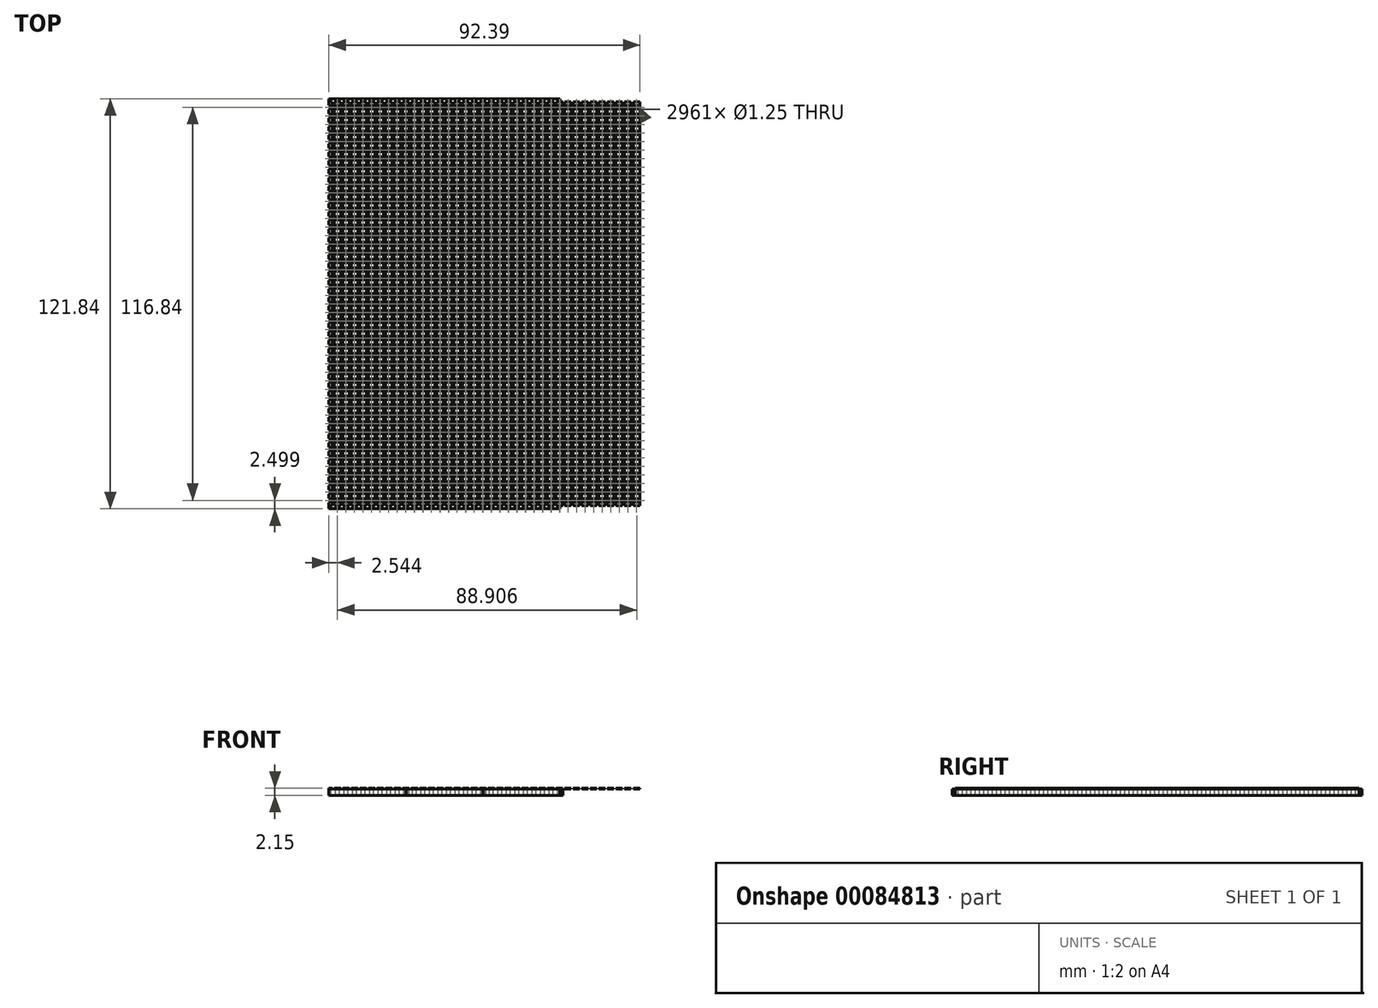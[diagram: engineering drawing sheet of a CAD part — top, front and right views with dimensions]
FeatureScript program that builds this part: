
annotation { "Feature Type Name" : "Feature", "Feature Type Description" : "" }
export const myFeature = defineFeature(function(context is Context, id is Id, definition is map)
    precondition{}
    {
        {
            var Q0;
            Q0=qCreatedBy(makeId("Top.planeOp"),FACE);
            var sketch = newSketch(context, id + "F0", { "sketchPlane" : qUnion([Q0])});
            skCircle(sketch, "E0", {"center": v(-51.8, -35.65) * mm, "radius": 0.63 * mm});
            skCircle(sketch, "E1.1.0.0", {"center": v(-49.26, -35.65) * mm, "radius": 0.63 * mm});
            skCircle(sketch, "E1.2.0.0", {"center": v(-46.72, -35.65) * mm, "radius": 0.63 * mm});
            skCircle(sketch, "E1.3.0.0", {"center": v(-44.18, -35.65) * mm, "radius": 0.63 * mm});
            skCircle(sketch, "E1.4.0.0", {"center": v(-41.64, -35.65) * mm, "radius": 0.63 * mm});
            skCircle(sketch, "E1.5.0.0", {"center": v(-39.1, -35.65) * mm, "radius": 0.63 * mm});
            skCircle(sketch, "E1.6.0.0", {"center": v(-36.56, -35.65) * mm, "radius": 0.63 * mm});
            skCircle(sketch, "E1.7.0.0", {"center": v(-34.02, -35.65) * mm, "radius": 0.63 * mm});
            skCircle(sketch, "E1.8.0.0", {"center": v(-31.48, -35.65) * mm, "radius": 0.63 * mm});
            skCircle(sketch, "E1.9.0.0", {"center": v(-28.94, -35.65) * mm, "radius": 0.63 * mm});
            skLineSegment(sketch, "E1.direction1", {"start": v(-51.8, -35.65) * mm, "end": v(-49.26, -35.65) * mm, "construction": true});
            skLineSegment(sketch, "E2.1.0.0", {"start": v(-51.8, -38.2) * mm, "end": v(-49.26, -38.2) * mm, "construction": true});
            skCircle(sketch, "E2.1.0.1", {"center": v(-28.94, -38.2) * mm, "radius": 0.63 * mm});
            skCircle(sketch, "E2.1.0.2", {"center": v(-31.48, -38.2) * mm, "radius": 0.63 * mm});
            skCircle(sketch, "E2.1.0.3", {"center": v(-34.02, -38.2) * mm, "radius": 0.63 * mm});
            skCircle(sketch, "E2.1.0.4", {"center": v(-36.56, -38.2) * mm, "radius": 0.63 * mm});
            skCircle(sketch, "E2.1.0.5", {"center": v(-39.1, -38.2) * mm, "radius": 0.63 * mm});
            skCircle(sketch, "E2.1.0.6", {"center": v(-41.64, -38.2) * mm, "radius": 0.63 * mm});
            skCircle(sketch, "E2.1.0.7", {"center": v(-44.18, -38.2) * mm, "radius": 0.63 * mm});
            skCircle(sketch, "E2.1.0.8", {"center": v(-46.72, -38.2) * mm, "radius": 0.63 * mm});
            skCircle(sketch, "E2.1.0.9", {"center": v(-49.26, -38.2) * mm, "radius": 0.63 * mm});
            skCircle(sketch, "E2.1.0.10", {"center": v(-51.8, -38.2) * mm, "radius": 0.63 * mm});
            skLineSegment(sketch, "E2.2.0.0", {"start": v(-51.8, -40.73) * mm, "end": v(-49.26, -40.73) * mm, "construction": true});
            skCircle(sketch, "E2.2.0.1", {"center": v(-28.94, -40.73) * mm, "radius": 0.63 * mm});
            skCircle(sketch, "E2.2.0.2", {"center": v(-31.48, -40.73) * mm, "radius": 0.63 * mm});
            skCircle(sketch, "E2.2.0.3", {"center": v(-34.02, -40.73) * mm, "radius": 0.63 * mm});
            skCircle(sketch, "E2.2.0.4", {"center": v(-36.56, -40.73) * mm, "radius": 0.63 * mm});
            skCircle(sketch, "E2.2.0.5", {"center": v(-39.1, -40.73) * mm, "radius": 0.63 * mm});
            skCircle(sketch, "E2.2.0.6", {"center": v(-41.64, -40.73) * mm, "radius": 0.63 * mm});
            skCircle(sketch, "E2.2.0.7", {"center": v(-44.18, -40.73) * mm, "radius": 0.63 * mm});
            skCircle(sketch, "E2.2.0.8", {"center": v(-46.72, -40.73) * mm, "radius": 0.63 * mm});
            skCircle(sketch, "E2.2.0.9", {"center": v(-49.26, -40.73) * mm, "radius": 0.63 * mm});
            skCircle(sketch, "E2.2.0.10", {"center": v(-51.8, -40.73) * mm, "radius": 0.63 * mm});
            skLineSegment(sketch, "E2.3.0.0", {"start": v(-51.8, -43.27) * mm, "end": v(-49.26, -43.27) * mm, "construction": true});
            skCircle(sketch, "E2.3.0.1", {"center": v(-28.94, -43.27) * mm, "radius": 0.63 * mm});
            skCircle(sketch, "E2.3.0.2", {"center": v(-31.48, -43.27) * mm, "radius": 0.63 * mm});
            skCircle(sketch, "E2.3.0.3", {"center": v(-34.02, -43.27) * mm, "radius": 0.63 * mm});
            skCircle(sketch, "E2.3.0.4", {"center": v(-36.56, -43.27) * mm, "radius": 0.63 * mm});
            skCircle(sketch, "E2.3.0.5", {"center": v(-39.1, -43.27) * mm, "radius": 0.63 * mm});
            skCircle(sketch, "E2.3.0.6", {"center": v(-41.64, -43.27) * mm, "radius": 0.63 * mm});
            skCircle(sketch, "E2.3.0.7", {"center": v(-44.18, -43.27) * mm, "radius": 0.63 * mm});
            skCircle(sketch, "E2.3.0.8", {"center": v(-46.72, -43.27) * mm, "radius": 0.63 * mm});
            skCircle(sketch, "E2.3.0.9", {"center": v(-49.26, -43.27) * mm, "radius": 0.63 * mm});
            skCircle(sketch, "E2.3.0.10", {"center": v(-51.8, -43.27) * mm, "radius": 0.63 * mm});
            skLineSegment(sketch, "E2.4.0.0", {"start": v(-51.8, -45.81) * mm, "end": v(-49.26, -45.81) * mm, "construction": true});
            skCircle(sketch, "E2.4.0.1", {"center": v(-28.94, -45.81) * mm, "radius": 0.63 * mm});
            skCircle(sketch, "E2.4.0.2", {"center": v(-31.48, -45.81) * mm, "radius": 0.63 * mm});
            skCircle(sketch, "E2.4.0.3", {"center": v(-34.02, -45.81) * mm, "radius": 0.63 * mm});
            skCircle(sketch, "E2.4.0.4", {"center": v(-36.56, -45.81) * mm, "radius": 0.63 * mm});
            skCircle(sketch, "E2.4.0.5", {"center": v(-39.1, -45.81) * mm, "radius": 0.63 * mm});
            skCircle(sketch, "E2.4.0.6", {"center": v(-41.64, -45.81) * mm, "radius": 0.63 * mm});
            skCircle(sketch, "E2.4.0.7", {"center": v(-44.18, -45.81) * mm, "radius": 0.63 * mm});
            skCircle(sketch, "E2.4.0.8", {"center": v(-46.72, -45.81) * mm, "radius": 0.63 * mm});
            skCircle(sketch, "E2.4.0.9", {"center": v(-49.26, -45.81) * mm, "radius": 0.63 * mm});
            skCircle(sketch, "E2.4.0.10", {"center": v(-51.8, -45.81) * mm, "radius": 0.63 * mm});
            skLineSegment(sketch, "E2.5.0.0", {"start": v(-51.8, -48.35) * mm, "end": v(-49.26, -48.35) * mm, "construction": true});
            skCircle(sketch, "E2.5.0.1", {"center": v(-28.94, -48.35) * mm, "radius": 0.63 * mm});
            skCircle(sketch, "E2.5.0.2", {"center": v(-31.48, -48.35) * mm, "radius": 0.63 * mm});
            skCircle(sketch, "E2.5.0.3", {"center": v(-34.02, -48.35) * mm, "radius": 0.63 * mm});
            skCircle(sketch, "E2.5.0.4", {"center": v(-36.56, -48.35) * mm, "radius": 0.63 * mm});
            skCircle(sketch, "E2.5.0.5", {"center": v(-39.1, -48.35) * mm, "radius": 0.63 * mm});
            skCircle(sketch, "E2.5.0.6", {"center": v(-41.64, -48.35) * mm, "radius": 0.63 * mm});
            skCircle(sketch, "E2.5.0.7", {"center": v(-44.18, -48.35) * mm, "radius": 0.63 * mm});
            skCircle(sketch, "E2.5.0.8", {"center": v(-46.72, -48.35) * mm, "radius": 0.63 * mm});
            skCircle(sketch, "E2.5.0.9", {"center": v(-49.26, -48.35) * mm, "radius": 0.63 * mm});
            skCircle(sketch, "E2.5.0.10", {"center": v(-51.8, -48.35) * mm, "radius": 0.63 * mm});
            skLineSegment(sketch, "E2.6.0.0", {"start": v(-51.8, -50.9) * mm, "end": v(-49.26, -50.9) * mm, "construction": true});
            skCircle(sketch, "E2.6.0.1", {"center": v(-28.94, -50.9) * mm, "radius": 0.63 * mm});
            skCircle(sketch, "E2.6.0.2", {"center": v(-31.48, -50.9) * mm, "radius": 0.63 * mm});
            skCircle(sketch, "E2.6.0.3", {"center": v(-34.02, -50.9) * mm, "radius": 0.63 * mm});
            skCircle(sketch, "E2.6.0.4", {"center": v(-36.56, -50.9) * mm, "radius": 0.63 * mm});
            skCircle(sketch, "E2.6.0.5", {"center": v(-39.1, -50.9) * mm, "radius": 0.63 * mm});
            skCircle(sketch, "E2.6.0.6", {"center": v(-41.64, -50.9) * mm, "radius": 0.63 * mm});
            skCircle(sketch, "E2.6.0.7", {"center": v(-44.18, -50.9) * mm, "radius": 0.63 * mm});
            skCircle(sketch, "E2.6.0.8", {"center": v(-46.72, -50.9) * mm, "radius": 0.63 * mm});
            skCircle(sketch, "E2.6.0.9", {"center": v(-49.26, -50.9) * mm, "radius": 0.63 * mm});
            skCircle(sketch, "E2.6.0.10", {"center": v(-51.8, -50.9) * mm, "radius": 0.63 * mm});
            skLineSegment(sketch, "E2.7.0.0", {"start": v(-51.8, -53.43) * mm, "end": v(-49.26, -53.43) * mm, "construction": true});
            skCircle(sketch, "E2.7.0.1", {"center": v(-28.94, -53.43) * mm, "radius": 0.63 * mm});
            skCircle(sketch, "E2.7.0.2", {"center": v(-31.48, -53.43) * mm, "radius": 0.63 * mm});
            skCircle(sketch, "E2.7.0.3", {"center": v(-34.02, -53.43) * mm, "radius": 0.63 * mm});
            skCircle(sketch, "E2.7.0.4", {"center": v(-36.56, -53.43) * mm, "radius": 0.63 * mm});
            skCircle(sketch, "E2.7.0.5", {"center": v(-39.1, -53.43) * mm, "radius": 0.63 * mm});
            skCircle(sketch, "E2.7.0.6", {"center": v(-41.64, -53.43) * mm, "radius": 0.63 * mm});
            skCircle(sketch, "E2.7.0.7", {"center": v(-44.18, -53.43) * mm, "radius": 0.63 * mm});
            skCircle(sketch, "E2.7.0.8", {"center": v(-46.72, -53.43) * mm, "radius": 0.63 * mm});
            skCircle(sketch, "E2.7.0.9", {"center": v(-49.26, -53.43) * mm, "radius": 0.63 * mm});
            skCircle(sketch, "E2.7.0.10", {"center": v(-51.8, -53.43) * mm, "radius": 0.63 * mm});
            skLineSegment(sketch, "E2.8.0.0", {"start": v(-51.8, -55.97) * mm, "end": v(-49.26, -55.97) * mm, "construction": true});
            skCircle(sketch, "E2.8.0.1", {"center": v(-28.94, -55.97) * mm, "radius": 0.63 * mm});
            skCircle(sketch, "E2.8.0.2", {"center": v(-31.48, -55.97) * mm, "radius": 0.63 * mm});
            skCircle(sketch, "E2.8.0.3", {"center": v(-34.02, -55.97) * mm, "radius": 0.63 * mm});
            skCircle(sketch, "E2.8.0.4", {"center": v(-36.56, -55.97) * mm, "radius": 0.63 * mm});
            skCircle(sketch, "E2.8.0.5", {"center": v(-39.1, -55.97) * mm, "radius": 0.63 * mm});
            skCircle(sketch, "E2.8.0.6", {"center": v(-41.64, -55.97) * mm, "radius": 0.63 * mm});
            skCircle(sketch, "E2.8.0.7", {"center": v(-44.18, -55.97) * mm, "radius": 0.63 * mm});
            skCircle(sketch, "E2.8.0.8", {"center": v(-46.72, -55.97) * mm, "radius": 0.63 * mm});
            skCircle(sketch, "E2.8.0.9", {"center": v(-49.26, -55.97) * mm, "radius": 0.63 * mm});
            skCircle(sketch, "E2.8.0.10", {"center": v(-51.8, -55.97) * mm, "radius": 0.63 * mm});
            skLineSegment(sketch, "E2.9.0.0", {"start": v(-51.8, -58.51) * mm, "end": v(-49.26, -58.51) * mm, "construction": true});
            skCircle(sketch, "E2.9.0.1", {"center": v(-28.94, -58.51) * mm, "radius": 0.63 * mm});
            skCircle(sketch, "E2.9.0.2", {"center": v(-31.48, -58.51) * mm, "radius": 0.63 * mm});
            skCircle(sketch, "E2.9.0.3", {"center": v(-34.02, -58.51) * mm, "radius": 0.63 * mm});
            skCircle(sketch, "E2.9.0.4", {"center": v(-36.56, -58.51) * mm, "radius": 0.63 * mm});
            skCircle(sketch, "E2.9.0.5", {"center": v(-39.1, -58.51) * mm, "radius": 0.63 * mm});
            skCircle(sketch, "E2.9.0.6", {"center": v(-41.64, -58.51) * mm, "radius": 0.63 * mm});
            skCircle(sketch, "E2.9.0.7", {"center": v(-44.18, -58.51) * mm, "radius": 0.63 * mm});
            skCircle(sketch, "E2.9.0.8", {"center": v(-46.72, -58.51) * mm, "radius": 0.63 * mm});
            skCircle(sketch, "E2.9.0.9", {"center": v(-49.26, -58.51) * mm, "radius": 0.63 * mm});
            skCircle(sketch, "E2.9.0.10", {"center": v(-51.8, -58.51) * mm, "radius": 0.63 * mm});
            skLineSegment(sketch, "E2.10.0.0", {"start": v(-51.8, -61.05) * mm, "end": v(-49.26, -61.05) * mm, "construction": true});
            skCircle(sketch, "E2.10.0.1", {"center": v(-28.94, -61.05) * mm, "radius": 0.63 * mm});
            skCircle(sketch, "E2.10.0.2", {"center": v(-31.48, -61.05) * mm, "radius": 0.63 * mm});
            skCircle(sketch, "E2.10.0.3", {"center": v(-34.02, -61.05) * mm, "radius": 0.63 * mm});
            skCircle(sketch, "E2.10.0.4", {"center": v(-36.56, -61.05) * mm, "radius": 0.63 * mm});
            skCircle(sketch, "E2.10.0.5", {"center": v(-39.1, -61.05) * mm, "radius": 0.63 * mm});
            skCircle(sketch, "E2.10.0.6", {"center": v(-41.64, -61.05) * mm, "radius": 0.63 * mm});
            skCircle(sketch, "E2.10.0.7", {"center": v(-44.18, -61.05) * mm, "radius": 0.63 * mm});
            skCircle(sketch, "E2.10.0.8", {"center": v(-46.72, -61.05) * mm, "radius": 0.63 * mm});
            skCircle(sketch, "E2.10.0.9", {"center": v(-49.26, -61.05) * mm, "radius": 0.63 * mm});
            skCircle(sketch, "E2.10.0.10", {"center": v(-51.8, -61.05) * mm, "radius": 0.63 * mm});
            skLineSegment(sketch, "E2.11.0.0", {"start": v(-51.8, -63.6) * mm, "end": v(-49.26, -63.6) * mm, "construction": true});
            skCircle(sketch, "E2.11.0.1", {"center": v(-28.94, -63.6) * mm, "radius": 0.63 * mm});
            skCircle(sketch, "E2.11.0.2", {"center": v(-31.48, -63.6) * mm, "radius": 0.63 * mm});
            skCircle(sketch, "E2.11.0.3", {"center": v(-34.02, -63.6) * mm, "radius": 0.63 * mm});
            skCircle(sketch, "E2.11.0.4", {"center": v(-36.56, -63.6) * mm, "radius": 0.63 * mm});
            skCircle(sketch, "E2.11.0.5", {"center": v(-39.1, -63.6) * mm, "radius": 0.63 * mm});
            skCircle(sketch, "E2.11.0.6", {"center": v(-41.64, -63.6) * mm, "radius": 0.63 * mm});
            skCircle(sketch, "E2.11.0.7", {"center": v(-44.18, -63.6) * mm, "radius": 0.63 * mm});
            skCircle(sketch, "E2.11.0.8", {"center": v(-46.72, -63.6) * mm, "radius": 0.63 * mm});
            skCircle(sketch, "E2.11.0.9", {"center": v(-49.26, -63.6) * mm, "radius": 0.63 * mm});
            skCircle(sketch, "E2.11.0.10", {"center": v(-51.8, -63.6) * mm, "radius": 0.63 * mm});
            skLineSegment(sketch, "E2.12.0.0", {"start": v(-51.8, -66.13) * mm, "end": v(-49.26, -66.13) * mm, "construction": true});
            skCircle(sketch, "E2.12.0.1", {"center": v(-28.94, -66.13) * mm, "radius": 0.63 * mm});
            skCircle(sketch, "E2.12.0.2", {"center": v(-31.48, -66.13) * mm, "radius": 0.63 * mm});
            skCircle(sketch, "E2.12.0.3", {"center": v(-34.02, -66.13) * mm, "radius": 0.63 * mm});
            skCircle(sketch, "E2.12.0.4", {"center": v(-36.56, -66.13) * mm, "radius": 0.63 * mm});
            skCircle(sketch, "E2.12.0.5", {"center": v(-39.1, -66.13) * mm, "radius": 0.63 * mm});
            skCircle(sketch, "E2.12.0.6", {"center": v(-41.64, -66.13) * mm, "radius": 0.63 * mm});
            skCircle(sketch, "E2.12.0.7", {"center": v(-44.18, -66.13) * mm, "radius": 0.63 * mm});
            skCircle(sketch, "E2.12.0.8", {"center": v(-46.72, -66.13) * mm, "radius": 0.63 * mm});
            skCircle(sketch, "E2.12.0.9", {"center": v(-49.26, -66.13) * mm, "radius": 0.63 * mm});
            skCircle(sketch, "E2.12.0.10", {"center": v(-51.8, -66.13) * mm, "radius": 0.63 * mm});
            skLineSegment(sketch, "E2.13.0.0", {"start": v(-51.8, -68.67) * mm, "end": v(-49.26, -68.67) * mm, "construction": true});
            skCircle(sketch, "E2.13.0.1", {"center": v(-28.94, -68.67) * mm, "radius": 0.63 * mm});
            skCircle(sketch, "E2.13.0.2", {"center": v(-31.48, -68.67) * mm, "radius": 0.63 * mm});
            skCircle(sketch, "E2.13.0.3", {"center": v(-34.02, -68.67) * mm, "radius": 0.63 * mm});
            skCircle(sketch, "E2.13.0.4", {"center": v(-36.56, -68.67) * mm, "radius": 0.63 * mm});
            skCircle(sketch, "E2.13.0.5", {"center": v(-39.1, -68.67) * mm, "radius": 0.63 * mm});
            skCircle(sketch, "E2.13.0.6", {"center": v(-41.64, -68.67) * mm, "radius": 0.63 * mm});
            skCircle(sketch, "E2.13.0.7", {"center": v(-44.18, -68.67) * mm, "radius": 0.63 * mm});
            skCircle(sketch, "E2.13.0.8", {"center": v(-46.72, -68.67) * mm, "radius": 0.63 * mm});
            skCircle(sketch, "E2.13.0.9", {"center": v(-49.26, -68.67) * mm, "radius": 0.63 * mm});
            skCircle(sketch, "E2.13.0.10", {"center": v(-51.8, -68.67) * mm, "radius": 0.63 * mm});
            skLineSegment(sketch, "E2.14.0.0", {"start": v(-51.8, -71.21) * mm, "end": v(-49.26, -71.21) * mm, "construction": true});
            skCircle(sketch, "E2.14.0.1", {"center": v(-28.94, -71.21) * mm, "radius": 0.63 * mm});
            skCircle(sketch, "E2.14.0.2", {"center": v(-31.48, -71.21) * mm, "radius": 0.63 * mm});
            skCircle(sketch, "E2.14.0.3", {"center": v(-34.02, -71.21) * mm, "radius": 0.63 * mm});
            skCircle(sketch, "E2.14.0.4", {"center": v(-36.56, -71.21) * mm, "radius": 0.63 * mm});
            skCircle(sketch, "E2.14.0.5", {"center": v(-39.1, -71.21) * mm, "radius": 0.63 * mm});
            skCircle(sketch, "E2.14.0.6", {"center": v(-41.64, -71.21) * mm, "radius": 0.63 * mm});
            skCircle(sketch, "E2.14.0.7", {"center": v(-44.18, -71.21) * mm, "radius": 0.63 * mm});
            skCircle(sketch, "E2.14.0.8", {"center": v(-46.72, -71.21) * mm, "radius": 0.63 * mm});
            skCircle(sketch, "E2.14.0.9", {"center": v(-49.26, -71.21) * mm, "radius": 0.63 * mm});
            skCircle(sketch, "E2.14.0.10", {"center": v(-51.8, -71.21) * mm, "radius": 0.63 * mm});
            skLineSegment(sketch, "E2.15.0.0", {"start": v(-51.8, -73.75) * mm, "end": v(-49.26, -73.75) * mm, "construction": true});
            skCircle(sketch, "E2.15.0.1", {"center": v(-28.94, -73.75) * mm, "radius": 0.63 * mm});
            skCircle(sketch, "E2.15.0.2", {"center": v(-31.48, -73.75) * mm, "radius": 0.63 * mm});
            skCircle(sketch, "E2.15.0.3", {"center": v(-34.02, -73.75) * mm, "radius": 0.63 * mm});
            skCircle(sketch, "E2.15.0.4", {"center": v(-36.56, -73.75) * mm, "radius": 0.63 * mm});
            skCircle(sketch, "E2.15.0.5", {"center": v(-39.1, -73.75) * mm, "radius": 0.63 * mm});
            skCircle(sketch, "E2.15.0.6", {"center": v(-41.64, -73.75) * mm, "radius": 0.63 * mm});
            skCircle(sketch, "E2.15.0.7", {"center": v(-44.18, -73.75) * mm, "radius": 0.63 * mm});
            skCircle(sketch, "E2.15.0.8", {"center": v(-46.72, -73.75) * mm, "radius": 0.63 * mm});
            skCircle(sketch, "E2.15.0.9", {"center": v(-49.26, -73.75) * mm, "radius": 0.63 * mm});
            skCircle(sketch, "E2.15.0.10", {"center": v(-51.8, -73.75) * mm, "radius": 0.63 * mm});
            skLineSegment(sketch, "E2.16.0.0", {"start": v(-51.8, -76.3) * mm, "end": v(-49.26, -76.3) * mm, "construction": true});
            skCircle(sketch, "E2.16.0.1", {"center": v(-28.94, -76.3) * mm, "radius": 0.63 * mm});
            skCircle(sketch, "E2.16.0.2", {"center": v(-31.48, -76.3) * mm, "radius": 0.63 * mm});
            skCircle(sketch, "E2.16.0.3", {"center": v(-34.02, -76.3) * mm, "radius": 0.63 * mm});
            skCircle(sketch, "E2.16.0.4", {"center": v(-36.56, -76.3) * mm, "radius": 0.63 * mm});
            skCircle(sketch, "E2.16.0.5", {"center": v(-39.1, -76.3) * mm, "radius": 0.63 * mm});
            skCircle(sketch, "E2.16.0.6", {"center": v(-41.64, -76.3) * mm, "radius": 0.63 * mm});
            skCircle(sketch, "E2.16.0.7", {"center": v(-44.18, -76.3) * mm, "radius": 0.63 * mm});
            skCircle(sketch, "E2.16.0.8", {"center": v(-46.72, -76.3) * mm, "radius": 0.63 * mm});
            skCircle(sketch, "E2.16.0.9", {"center": v(-49.26, -76.3) * mm, "radius": 0.63 * mm});
            skCircle(sketch, "E2.16.0.10", {"center": v(-51.8, -76.3) * mm, "radius": 0.63 * mm});
            skLineSegment(sketch, "E2.17.0.0", {"start": v(-51.8, -78.83) * mm, "end": v(-49.26, -78.83) * mm, "construction": true});
            skCircle(sketch, "E2.17.0.1", {"center": v(-28.94, -78.83) * mm, "radius": 0.63 * mm});
            skCircle(sketch, "E2.17.0.2", {"center": v(-31.48, -78.83) * mm, "radius": 0.63 * mm});
            skCircle(sketch, "E2.17.0.3", {"center": v(-34.02, -78.83) * mm, "radius": 0.63 * mm});
            skCircle(sketch, "E2.17.0.4", {"center": v(-36.56, -78.83) * mm, "radius": 0.63 * mm});
            skCircle(sketch, "E2.17.0.5", {"center": v(-39.1, -78.83) * mm, "radius": 0.63 * mm});
            skCircle(sketch, "E2.17.0.6", {"center": v(-41.64, -78.83) * mm, "radius": 0.63 * mm});
            skCircle(sketch, "E2.17.0.7", {"center": v(-44.18, -78.83) * mm, "radius": 0.63 * mm});
            skCircle(sketch, "E2.17.0.8", {"center": v(-46.72, -78.83) * mm, "radius": 0.63 * mm});
            skCircle(sketch, "E2.17.0.9", {"center": v(-49.26, -78.83) * mm, "radius": 0.63 * mm});
            skCircle(sketch, "E2.17.0.10", {"center": v(-51.8, -78.83) * mm, "radius": 0.63 * mm});
            skLineSegment(sketch, "E2.18.0.0", {"start": v(-51.8, -81.37) * mm, "end": v(-49.26, -81.37) * mm, "construction": true});
            skCircle(sketch, "E2.18.0.1", {"center": v(-28.94, -81.37) * mm, "radius": 0.63 * mm});
            skCircle(sketch, "E2.18.0.2", {"center": v(-31.48, -81.37) * mm, "radius": 0.63 * mm});
            skCircle(sketch, "E2.18.0.3", {"center": v(-34.02, -81.37) * mm, "radius": 0.63 * mm});
            skCircle(sketch, "E2.18.0.4", {"center": v(-36.56, -81.37) * mm, "radius": 0.63 * mm});
            skCircle(sketch, "E2.18.0.5", {"center": v(-39.1, -81.37) * mm, "radius": 0.63 * mm});
            skCircle(sketch, "E2.18.0.6", {"center": v(-41.64, -81.37) * mm, "radius": 0.63 * mm});
            skCircle(sketch, "E2.18.0.7", {"center": v(-44.18, -81.37) * mm, "radius": 0.63 * mm});
            skCircle(sketch, "E2.18.0.8", {"center": v(-46.72, -81.37) * mm, "radius": 0.63 * mm});
            skCircle(sketch, "E2.18.0.9", {"center": v(-49.26, -81.37) * mm, "radius": 0.63 * mm});
            skCircle(sketch, "E2.18.0.10", {"center": v(-51.8, -81.37) * mm, "radius": 0.63 * mm});
            skLineSegment(sketch, "E2.19.0.0", {"start": v(-51.8, -83.91) * mm, "end": v(-49.26, -83.91) * mm, "construction": true});
            skCircle(sketch, "E2.19.0.1", {"center": v(-28.94, -83.91) * mm, "radius": 0.63 * mm});
            skCircle(sketch, "E2.19.0.2", {"center": v(-31.48, -83.91) * mm, "radius": 0.63 * mm});
            skCircle(sketch, "E2.19.0.3", {"center": v(-34.02, -83.91) * mm, "radius": 0.63 * mm});
            skCircle(sketch, "E2.19.0.4", {"center": v(-36.56, -83.91) * mm, "radius": 0.63 * mm});
            skCircle(sketch, "E2.19.0.5", {"center": v(-39.1, -83.91) * mm, "radius": 0.63 * mm});
            skCircle(sketch, "E2.19.0.6", {"center": v(-41.64, -83.91) * mm, "radius": 0.63 * mm});
            skCircle(sketch, "E2.19.0.7", {"center": v(-44.18, -83.91) * mm, "radius": 0.63 * mm});
            skCircle(sketch, "E2.19.0.8", {"center": v(-46.72, -83.91) * mm, "radius": 0.63 * mm});
            skCircle(sketch, "E2.19.0.9", {"center": v(-49.26, -83.91) * mm, "radius": 0.63 * mm});
            skCircle(sketch, "E2.19.0.10", {"center": v(-51.8, -83.91) * mm, "radius": 0.63 * mm});
            skLineSegment(sketch, "E2.20.0.0", {"start": v(-51.8, -86.45) * mm, "end": v(-49.26, -86.45) * mm, "construction": true});
            skCircle(sketch, "E2.20.0.1", {"center": v(-28.94, -86.45) * mm, "radius": 0.63 * mm});
            skCircle(sketch, "E2.20.0.2", {"center": v(-31.48, -86.45) * mm, "radius": 0.63 * mm});
            skCircle(sketch, "E2.20.0.3", {"center": v(-34.02, -86.45) * mm, "radius": 0.63 * mm});
            skCircle(sketch, "E2.20.0.4", {"center": v(-36.56, -86.45) * mm, "radius": 0.63 * mm});
            skCircle(sketch, "E2.20.0.5", {"center": v(-39.1, -86.45) * mm, "radius": 0.63 * mm});
            skCircle(sketch, "E2.20.0.6", {"center": v(-41.64, -86.45) * mm, "radius": 0.63 * mm});
            skCircle(sketch, "E2.20.0.7", {"center": v(-44.18, -86.45) * mm, "radius": 0.63 * mm});
            skCircle(sketch, "E2.20.0.8", {"center": v(-46.72, -86.45) * mm, "radius": 0.63 * mm});
            skCircle(sketch, "E2.20.0.9", {"center": v(-49.26, -86.45) * mm, "radius": 0.63 * mm});
            skCircle(sketch, "E2.20.0.10", {"center": v(-51.8, -86.45) * mm, "radius": 0.63 * mm});
            skLineSegment(sketch, "E2.21.0.0", {"start": v(-51.8, -89) * mm, "end": v(-49.26, -89) * mm, "construction": true});
            skCircle(sketch, "E2.21.0.1", {"center": v(-28.94, -89) * mm, "radius": 0.63 * mm});
            skCircle(sketch, "E2.21.0.2", {"center": v(-31.48, -89) * mm, "radius": 0.63 * mm});
            skCircle(sketch, "E2.21.0.3", {"center": v(-34.02, -89) * mm, "radius": 0.63 * mm});
            skCircle(sketch, "E2.21.0.4", {"center": v(-36.56, -89) * mm, "radius": 0.63 * mm});
            skCircle(sketch, "E2.21.0.5", {"center": v(-39.1, -89) * mm, "radius": 0.63 * mm});
            skCircle(sketch, "E2.21.0.6", {"center": v(-41.64, -89) * mm, "radius": 0.63 * mm});
            skCircle(sketch, "E2.21.0.7", {"center": v(-44.18, -89) * mm, "radius": 0.63 * mm});
            skCircle(sketch, "E2.21.0.8", {"center": v(-46.72, -89) * mm, "radius": 0.63 * mm});
            skCircle(sketch, "E2.21.0.9", {"center": v(-49.26, -89) * mm, "radius": 0.63 * mm});
            skCircle(sketch, "E2.21.0.10", {"center": v(-51.8, -89) * mm, "radius": 0.63 * mm});
            skLineSegment(sketch, "E2.22.0.0", {"start": v(-51.8, -91.53) * mm, "end": v(-49.26, -91.53) * mm, "construction": true});
            skCircle(sketch, "E2.22.0.1", {"center": v(-28.94, -91.53) * mm, "radius": 0.63 * mm});
            skCircle(sketch, "E2.22.0.2", {"center": v(-31.48, -91.53) * mm, "radius": 0.63 * mm});
            skCircle(sketch, "E2.22.0.3", {"center": v(-34.02, -91.53) * mm, "radius": 0.63 * mm});
            skCircle(sketch, "E2.22.0.4", {"center": v(-36.56, -91.53) * mm, "radius": 0.63 * mm});
            skCircle(sketch, "E2.22.0.5", {"center": v(-39.1, -91.53) * mm, "radius": 0.63 * mm});
            skCircle(sketch, "E2.22.0.6", {"center": v(-41.64, -91.53) * mm, "radius": 0.63 * mm});
            skCircle(sketch, "E2.22.0.7", {"center": v(-44.18, -91.53) * mm, "radius": 0.63 * mm});
            skCircle(sketch, "E2.22.0.8", {"center": v(-46.72, -91.53) * mm, "radius": 0.63 * mm});
            skCircle(sketch, "E2.22.0.9", {"center": v(-49.26, -91.53) * mm, "radius": 0.63 * mm});
            skCircle(sketch, "E2.22.0.10", {"center": v(-51.8, -91.53) * mm, "radius": 0.63 * mm});
            skLineSegment(sketch, "E2.23.0.0", {"start": v(-51.8, -94.07) * mm, "end": v(-49.26, -94.07) * mm, "construction": true});
            skCircle(sketch, "E2.23.0.1", {"center": v(-28.94, -94.07) * mm, "radius": 0.63 * mm});
            skCircle(sketch, "E2.23.0.2", {"center": v(-31.48, -94.07) * mm, "radius": 0.63 * mm});
            skCircle(sketch, "E2.23.0.3", {"center": v(-34.02, -94.07) * mm, "radius": 0.63 * mm});
            skCircle(sketch, "E2.23.0.4", {"center": v(-36.56, -94.07) * mm, "radius": 0.63 * mm});
            skCircle(sketch, "E2.23.0.5", {"center": v(-39.1, -94.07) * mm, "radius": 0.63 * mm});
            skCircle(sketch, "E2.23.0.6", {"center": v(-41.64, -94.07) * mm, "radius": 0.63 * mm});
            skCircle(sketch, "E2.23.0.7", {"center": v(-44.18, -94.07) * mm, "radius": 0.63 * mm});
            skCircle(sketch, "E2.23.0.8", {"center": v(-46.72, -94.07) * mm, "radius": 0.63 * mm});
            skCircle(sketch, "E2.23.0.9", {"center": v(-49.26, -94.07) * mm, "radius": 0.63 * mm});
            skCircle(sketch, "E2.23.0.10", {"center": v(-51.8, -94.07) * mm, "radius": 0.63 * mm});
            skLineSegment(sketch, "E2.24.0.0", {"start": v(-51.8, -96.61) * mm, "end": v(-49.26, -96.61) * mm, "construction": true});
            skCircle(sketch, "E2.24.0.1", {"center": v(-28.94, -96.61) * mm, "radius": 0.63 * mm});
            skCircle(sketch, "E2.24.0.2", {"center": v(-31.48, -96.61) * mm, "radius": 0.63 * mm});
            skCircle(sketch, "E2.24.0.3", {"center": v(-34.02, -96.61) * mm, "radius": 0.63 * mm});
            skCircle(sketch, "E2.24.0.4", {"center": v(-36.56, -96.61) * mm, "radius": 0.63 * mm});
            skCircle(sketch, "E2.24.0.5", {"center": v(-39.1, -96.61) * mm, "radius": 0.63 * mm});
            skCircle(sketch, "E2.24.0.6", {"center": v(-41.64, -96.61) * mm, "radius": 0.63 * mm});
            skCircle(sketch, "E2.24.0.7", {"center": v(-44.18, -96.61) * mm, "radius": 0.63 * mm});
            skCircle(sketch, "E2.24.0.8", {"center": v(-46.72, -96.61) * mm, "radius": 0.63 * mm});
            skCircle(sketch, "E2.24.0.9", {"center": v(-49.26, -96.61) * mm, "radius": 0.63 * mm});
            skCircle(sketch, "E2.24.0.10", {"center": v(-51.8, -96.61) * mm, "radius": 0.63 * mm});
            skLineSegment(sketch, "E2.25.0.0", {"start": v(-51.8, -99.15) * mm, "end": v(-49.26, -99.15) * mm, "construction": true});
            skCircle(sketch, "E2.25.0.1", {"center": v(-28.94, -99.15) * mm, "radius": 0.63 * mm});
            skCircle(sketch, "E2.25.0.2", {"center": v(-31.48, -99.15) * mm, "radius": 0.63 * mm});
            skCircle(sketch, "E2.25.0.3", {"center": v(-34.02, -99.15) * mm, "radius": 0.63 * mm});
            skCircle(sketch, "E2.25.0.4", {"center": v(-36.56, -99.15) * mm, "radius": 0.63 * mm});
            skCircle(sketch, "E2.25.0.5", {"center": v(-39.1, -99.15) * mm, "radius": 0.63 * mm});
            skCircle(sketch, "E2.25.0.6", {"center": v(-41.64, -99.15) * mm, "radius": 0.63 * mm});
            skCircle(sketch, "E2.25.0.7", {"center": v(-44.18, -99.15) * mm, "radius": 0.63 * mm});
            skCircle(sketch, "E2.25.0.8", {"center": v(-46.72, -99.15) * mm, "radius": 0.63 * mm});
            skCircle(sketch, "E2.25.0.9", {"center": v(-49.26, -99.15) * mm, "radius": 0.63 * mm});
            skCircle(sketch, "E2.25.0.10", {"center": v(-51.8, -99.15) * mm, "radius": 0.63 * mm});
            skLineSegment(sketch, "E2.26.0.0", {"start": v(-51.8, -101.7) * mm, "end": v(-49.26, -101.7) * mm, "construction": true});
            skCircle(sketch, "E2.26.0.1", {"center": v(-28.94, -101.7) * mm, "radius": 0.63 * mm});
            skCircle(sketch, "E2.26.0.2", {"center": v(-31.48, -101.7) * mm, "radius": 0.63 * mm});
            skCircle(sketch, "E2.26.0.3", {"center": v(-34.02, -101.7) * mm, "radius": 0.63 * mm});
            skCircle(sketch, "E2.26.0.4", {"center": v(-36.56, -101.7) * mm, "radius": 0.63 * mm});
            skCircle(sketch, "E2.26.0.5", {"center": v(-39.1, -101.7) * mm, "radius": 0.63 * mm});
            skCircle(sketch, "E2.26.0.6", {"center": v(-41.64, -101.7) * mm, "radius": 0.63 * mm});
            skCircle(sketch, "E2.26.0.7", {"center": v(-44.18, -101.7) * mm, "radius": 0.63 * mm});
            skCircle(sketch, "E2.26.0.8", {"center": v(-46.72, -101.7) * mm, "radius": 0.63 * mm});
            skCircle(sketch, "E2.26.0.9", {"center": v(-49.26, -101.7) * mm, "radius": 0.63 * mm});
            skCircle(sketch, "E2.26.0.10", {"center": v(-51.8, -101.7) * mm, "radius": 0.63 * mm});
            skLineSegment(sketch, "E2.27.0.0", {"start": v(-51.8, -104.23) * mm, "end": v(-49.26, -104.23) * mm, "construction": true});
            skCircle(sketch, "E2.27.0.1", {"center": v(-28.94, -104.23) * mm, "radius": 0.63 * mm});
            skCircle(sketch, "E2.27.0.2", {"center": v(-31.48, -104.23) * mm, "radius": 0.63 * mm});
            skCircle(sketch, "E2.27.0.3", {"center": v(-34.02, -104.23) * mm, "radius": 0.63 * mm});
            skCircle(sketch, "E2.27.0.4", {"center": v(-36.56, -104.23) * mm, "radius": 0.63 * mm});
            skCircle(sketch, "E2.27.0.5", {"center": v(-39.1, -104.23) * mm, "radius": 0.63 * mm});
            skCircle(sketch, "E2.27.0.6", {"center": v(-41.64, -104.23) * mm, "radius": 0.63 * mm});
            skCircle(sketch, "E2.27.0.7", {"center": v(-44.18, -104.23) * mm, "radius": 0.63 * mm});
            skCircle(sketch, "E2.27.0.8", {"center": v(-46.72, -104.23) * mm, "radius": 0.63 * mm});
            skCircle(sketch, "E2.27.0.9", {"center": v(-49.26, -104.23) * mm, "radius": 0.63 * mm});
            skCircle(sketch, "E2.27.0.10", {"center": v(-51.8, -104.23) * mm, "radius": 0.63 * mm});
            skLineSegment(sketch, "E2.28.0.0", {"start": v(-51.8, -106.77) * mm, "end": v(-49.26, -106.77) * mm, "construction": true});
            skCircle(sketch, "E2.28.0.1", {"center": v(-28.94, -106.77) * mm, "radius": 0.63 * mm});
            skCircle(sketch, "E2.28.0.2", {"center": v(-31.48, -106.77) * mm, "radius": 0.63 * mm});
            skCircle(sketch, "E2.28.0.3", {"center": v(-34.02, -106.77) * mm, "radius": 0.63 * mm});
            skCircle(sketch, "E2.28.0.4", {"center": v(-36.56, -106.77) * mm, "radius": 0.63 * mm});
            skCircle(sketch, "E2.28.0.5", {"center": v(-39.1, -106.77) * mm, "radius": 0.63 * mm});
            skCircle(sketch, "E2.28.0.6", {"center": v(-41.64, -106.77) * mm, "radius": 0.63 * mm});
            skCircle(sketch, "E2.28.0.7", {"center": v(-44.18, -106.77) * mm, "radius": 0.63 * mm});
            skCircle(sketch, "E2.28.0.8", {"center": v(-46.72, -106.77) * mm, "radius": 0.63 * mm});
            skCircle(sketch, "E2.28.0.9", {"center": v(-49.26, -106.77) * mm, "radius": 0.63 * mm});
            skCircle(sketch, "E2.28.0.10", {"center": v(-51.8, -106.77) * mm, "radius": 0.63 * mm});
            skLineSegment(sketch, "E2.29.0.0", {"start": v(-51.8, -109.31) * mm, "end": v(-49.26, -109.31) * mm, "construction": true});
            skCircle(sketch, "E2.29.0.1", {"center": v(-28.94, -109.31) * mm, "radius": 0.63 * mm});
            skCircle(sketch, "E2.29.0.2", {"center": v(-31.48, -109.31) * mm, "radius": 0.63 * mm});
            skCircle(sketch, "E2.29.0.3", {"center": v(-34.02, -109.31) * mm, "radius": 0.63 * mm});
            skCircle(sketch, "E2.29.0.4", {"center": v(-36.56, -109.31) * mm, "radius": 0.63 * mm});
            skCircle(sketch, "E2.29.0.5", {"center": v(-39.1, -109.31) * mm, "radius": 0.63 * mm});
            skCircle(sketch, "E2.29.0.6", {"center": v(-41.64, -109.31) * mm, "radius": 0.63 * mm});
            skCircle(sketch, "E2.29.0.7", {"center": v(-44.18, -109.31) * mm, "radius": 0.63 * mm});
            skCircle(sketch, "E2.29.0.8", {"center": v(-46.72, -109.31) * mm, "radius": 0.63 * mm});
            skCircle(sketch, "E2.29.0.9", {"center": v(-49.26, -109.31) * mm, "radius": 0.63 * mm});
            skCircle(sketch, "E2.29.0.10", {"center": v(-51.8, -109.31) * mm, "radius": 0.63 * mm});
            skLineSegment(sketch, "E2.direction1", {"start": v(-51.8, -35.65) * mm, "end": v(-51.8, -38.2) * mm, "construction": true});
            skLineSegment(sketch, "E3", {"start": v(-51.8, -35.65) * mm, "end": v(-51.8, -61.4) * mm});
            skLineSegment(sketch, "E4", {"start": v(-28.93, -33.15) * mm, "end": v(-51.8, -33.15) * mm});
            skLineSegment(sketch, "E5", {"start": v(-28.93, -61.4) * mm, "end": v(-28.93, -152.5) * mm});
            skLineSegment(sketch, "E6", {"start": v(-28.93, -152.5) * mm, "end": v(-51.8, -152.5) * mm});
            skLineSegment(sketch, "E7", {"start": v(-51.8, -152.5) * mm, "end": v(-51.8, -61.4) * mm});
            skLineSegment(sketch, "E8", {"start": v(-51.8, -35.65) * mm, "end": v(-51.8, -33.15) * mm});
            skCircle(sketch, "E9.5.30.0", {"center": v(-31.48, -111.85) * mm, "radius": 0.63 * mm});
            skCircle(sketch, "E9.7.30.0", {"center": v(-34.02, -111.85) * mm, "radius": 0.63 * mm});
            skCircle(sketch, "E9.9.30.0", {"center": v(-36.56, -111.85) * mm, "radius": 0.63 * mm});
            skCircle(sketch, "E9.11.30.0", {"center": v(-39.1, -111.85) * mm, "radius": 0.63 * mm});
            skCircle(sketch, "E9.13.30.0", {"center": v(-41.64, -111.85) * mm, "radius": 0.63 * mm});
            skCircle(sketch, "E9.15.30.0", {"center": v(-44.18, -111.85) * mm, "radius": 0.63 * mm});
            skCircle(sketch, "E9.17.30.0", {"center": v(-46.72, -111.85) * mm, "radius": 0.63 * mm});
            skCircle(sketch, "E9.19.30.0", {"center": v(-49.26, -111.85) * mm, "radius": 0.63 * mm});
            skCircle(sketch, "E9.21.30.0", {"center": v(-51.8, -111.85) * mm, "radius": 0.63 * mm});
            skLineSegment(sketch, "E9.0.31.0", {"start": v(-51.8, -114.4) * mm, "end": v(-49.26, -114.4) * mm, "construction": true});
            skCircle(sketch, "E9.3.31.0", {"center": v(-28.94, -114.4) * mm, "radius": 0.63 * mm});
            skCircle(sketch, "E9.5.31.0", {"center": v(-31.48, -114.4) * mm, "radius": 0.63 * mm});
            skCircle(sketch, "E9.7.31.0", {"center": v(-34.02, -114.4) * mm, "radius": 0.63 * mm});
            skCircle(sketch, "E9.9.31.0", {"center": v(-36.56, -114.4) * mm, "radius": 0.63 * mm});
            skCircle(sketch, "E9.11.31.0", {"center": v(-39.1, -114.4) * mm, "radius": 0.63 * mm});
            skCircle(sketch, "E9.13.31.0", {"center": v(-41.64, -114.4) * mm, "radius": 0.63 * mm});
            skCircle(sketch, "E9.15.31.0", {"center": v(-44.18, -114.4) * mm, "radius": 0.63 * mm});
            skCircle(sketch, "E9.17.31.0", {"center": v(-46.72, -114.4) * mm, "radius": 0.63 * mm});
            skCircle(sketch, "E9.19.31.0", {"center": v(-49.26, -114.4) * mm, "radius": 0.63 * mm});
            skCircle(sketch, "E9.21.31.0", {"center": v(-51.8, -114.4) * mm, "radius": 0.63 * mm});
            skLineSegment(sketch, "E9.0.32.0", {"start": v(-51.8, -116.93) * mm, "end": v(-49.26, -116.93) * mm, "construction": true});
            skCircle(sketch, "E9.3.32.0", {"center": v(-28.94, -116.93) * mm, "radius": 0.63 * mm});
            skCircle(sketch, "E9.5.32.0", {"center": v(-31.48, -116.93) * mm, "radius": 0.63 * mm});
            skCircle(sketch, "E9.7.32.0", {"center": v(-34.02, -116.93) * mm, "radius": 0.63 * mm});
            skCircle(sketch, "E9.9.32.0", {"center": v(-36.56, -116.93) * mm, "radius": 0.63 * mm});
            skCircle(sketch, "E9.11.32.0", {"center": v(-39.1, -116.93) * mm, "radius": 0.63 * mm});
            skCircle(sketch, "E9.13.32.0", {"center": v(-41.64, -116.93) * mm, "radius": 0.63 * mm});
            skCircle(sketch, "E9.15.32.0", {"center": v(-44.18, -116.93) * mm, "radius": 0.63 * mm});
            skCircle(sketch, "E9.17.32.0", {"center": v(-46.72, -116.93) * mm, "radius": 0.63 * mm});
            skCircle(sketch, "E9.19.32.0", {"center": v(-49.26, -116.93) * mm, "radius": 0.63 * mm});
            skCircle(sketch, "E9.21.32.0", {"center": v(-51.8, -116.93) * mm, "radius": 0.63 * mm});
            skLineSegment(sketch, "E9.0.33.0", {"start": v(-51.8, -119.47) * mm, "end": v(-49.26, -119.47) * mm, "construction": true});
            skCircle(sketch, "E9.3.33.0", {"center": v(-28.94, -119.47) * mm, "radius": 0.63 * mm});
            skCircle(sketch, "E9.5.33.0", {"center": v(-31.48, -119.47) * mm, "radius": 0.63 * mm});
            skCircle(sketch, "E9.7.33.0", {"center": v(-34.02, -119.47) * mm, "radius": 0.63 * mm});
            skCircle(sketch, "E9.9.33.0", {"center": v(-36.56, -119.47) * mm, "radius": 0.63 * mm});
            skCircle(sketch, "E9.11.33.0", {"center": v(-39.1, -119.47) * mm, "radius": 0.63 * mm});
            skCircle(sketch, "E9.13.33.0", {"center": v(-41.64, -119.47) * mm, "radius": 0.63 * mm});
            skCircle(sketch, "E9.15.33.0", {"center": v(-44.18, -119.47) * mm, "radius": 0.63 * mm});
            skCircle(sketch, "E9.17.33.0", {"center": v(-46.72, -119.47) * mm, "radius": 0.63 * mm});
            skCircle(sketch, "E9.19.33.0", {"center": v(-49.26, -119.47) * mm, "radius": 0.63 * mm});
            skCircle(sketch, "E9.21.33.0", {"center": v(-51.8, -119.47) * mm, "radius": 0.63 * mm});
            skLineSegment(sketch, "E9.0.34.0", {"start": v(-51.8, -122.01) * mm, "end": v(-49.26, -122.01) * mm, "construction": true});
            skCircle(sketch, "E9.3.34.0", {"center": v(-28.94, -122.01) * mm, "radius": 0.63 * mm});
            skCircle(sketch, "E9.5.34.0", {"center": v(-31.48, -122.01) * mm, "radius": 0.63 * mm});
            skCircle(sketch, "E9.7.34.0", {"center": v(-34.02, -122.01) * mm, "radius": 0.63 * mm});
            skCircle(sketch, "E9.9.34.0", {"center": v(-36.56, -122.01) * mm, "radius": 0.63 * mm});
            skCircle(sketch, "E9.11.34.0", {"center": v(-39.1, -122.01) * mm, "radius": 0.63 * mm});
            skCircle(sketch, "E9.13.34.0", {"center": v(-41.64, -122.01) * mm, "radius": 0.63 * mm});
            skCircle(sketch, "E9.15.34.0", {"center": v(-44.18, -122.01) * mm, "radius": 0.63 * mm});
            skCircle(sketch, "E9.17.34.0", {"center": v(-46.72, -122.01) * mm, "radius": 0.63 * mm});
            skCircle(sketch, "E9.19.34.0", {"center": v(-49.26, -122.01) * mm, "radius": 0.63 * mm});
            skCircle(sketch, "E9.21.34.0", {"center": v(-51.8, -122.01) * mm, "radius": 0.63 * mm});
            skLineSegment(sketch, "E9.0.35.0", {"start": v(-51.8, -124.55) * mm, "end": v(-49.26, -124.55) * mm, "construction": true});
            skCircle(sketch, "E9.3.35.0", {"center": v(-28.94, -124.55) * mm, "radius": 0.63 * mm});
            skCircle(sketch, "E9.5.35.0", {"center": v(-31.48, -124.55) * mm, "radius": 0.63 * mm});
            skCircle(sketch, "E9.7.35.0", {"center": v(-34.02, -124.55) * mm, "radius": 0.63 * mm});
            skCircle(sketch, "E9.9.35.0", {"center": v(-36.56, -124.55) * mm, "radius": 0.63 * mm});
            skCircle(sketch, "E9.11.35.0", {"center": v(-39.1, -124.55) * mm, "radius": 0.63 * mm});
            skCircle(sketch, "E9.13.35.0", {"center": v(-41.64, -124.55) * mm, "radius": 0.63 * mm});
            skCircle(sketch, "E9.15.35.0", {"center": v(-44.18, -124.55) * mm, "radius": 0.63 * mm});
            skCircle(sketch, "E9.17.35.0", {"center": v(-46.72, -124.55) * mm, "radius": 0.63 * mm});
            skCircle(sketch, "E9.19.35.0", {"center": v(-49.26, -124.55) * mm, "radius": 0.63 * mm});
            skCircle(sketch, "E9.21.35.0", {"center": v(-51.8, -124.55) * mm, "radius": 0.63 * mm});
            skLineSegment(sketch, "E9.0.36.0", {"start": v(-51.8, -127.1) * mm, "end": v(-49.26, -127.1) * mm, "construction": true});
            skCircle(sketch, "E9.3.36.0", {"center": v(-28.94, -127.1) * mm, "radius": 0.63 * mm});
            skCircle(sketch, "E9.5.36.0", {"center": v(-31.48, -127.1) * mm, "radius": 0.63 * mm});
            skCircle(sketch, "E9.7.36.0", {"center": v(-34.02, -127.1) * mm, "radius": 0.63 * mm});
            skCircle(sketch, "E9.9.36.0", {"center": v(-36.56, -127.1) * mm, "radius": 0.63 * mm});
            skCircle(sketch, "E9.11.36.0", {"center": v(-39.1, -127.1) * mm, "radius": 0.63 * mm});
            skCircle(sketch, "E9.13.36.0", {"center": v(-41.64, -127.1) * mm, "radius": 0.63 * mm});
            skCircle(sketch, "E9.15.36.0", {"center": v(-44.18, -127.1) * mm, "radius": 0.63 * mm});
            skCircle(sketch, "E9.17.36.0", {"center": v(-46.72, -127.1) * mm, "radius": 0.63 * mm});
            skCircle(sketch, "E9.19.36.0", {"center": v(-49.26, -127.1) * mm, "radius": 0.63 * mm});
            skCircle(sketch, "E9.21.36.0", {"center": v(-51.8, -127.1) * mm, "radius": 0.63 * mm});
            skLineSegment(sketch, "E9.0.37.0", {"start": v(-51.8, -129.63) * mm, "end": v(-49.26, -129.63) * mm, "construction": true});
            skCircle(sketch, "E9.3.37.0", {"center": v(-28.94, -129.63) * mm, "radius": 0.63 * mm});
            skCircle(sketch, "E9.5.37.0", {"center": v(-31.48, -129.63) * mm, "radius": 0.63 * mm});
            skCircle(sketch, "E9.7.37.0", {"center": v(-34.02, -129.63) * mm, "radius": 0.63 * mm});
            skCircle(sketch, "E9.9.37.0", {"center": v(-36.56, -129.63) * mm, "radius": 0.63 * mm});
            skCircle(sketch, "E9.11.37.0", {"center": v(-39.1, -129.63) * mm, "radius": 0.63 * mm});
            skCircle(sketch, "E9.13.37.0", {"center": v(-41.64, -129.63) * mm, "radius": 0.63 * mm});
            skCircle(sketch, "E9.15.37.0", {"center": v(-44.18, -129.63) * mm, "radius": 0.63 * mm});
            skCircle(sketch, "E9.17.37.0", {"center": v(-46.72, -129.63) * mm, "radius": 0.63 * mm});
            skCircle(sketch, "E9.19.37.0", {"center": v(-49.26, -129.63) * mm, "radius": 0.63 * mm});
            skCircle(sketch, "E9.21.37.0", {"center": v(-51.8, -129.63) * mm, "radius": 0.63 * mm});
            skLineSegment(sketch, "E9.0.38.0", {"start": v(-51.8, -132.17) * mm, "end": v(-49.26, -132.17) * mm, "construction": true});
            skCircle(sketch, "E9.3.38.0", {"center": v(-28.94, -132.17) * mm, "radius": 0.63 * mm});
            skCircle(sketch, "E9.5.38.0", {"center": v(-31.48, -132.17) * mm, "radius": 0.63 * mm});
            skCircle(sketch, "E9.7.38.0", {"center": v(-34.02, -132.17) * mm, "radius": 0.63 * mm});
            skCircle(sketch, "E9.9.38.0", {"center": v(-36.56, -132.17) * mm, "radius": 0.63 * mm});
            skCircle(sketch, "E9.11.38.0", {"center": v(-39.1, -132.17) * mm, "radius": 0.63 * mm});
            skCircle(sketch, "E9.13.38.0", {"center": v(-41.64, -132.17) * mm, "radius": 0.63 * mm});
            skCircle(sketch, "E9.15.38.0", {"center": v(-44.18, -132.17) * mm, "radius": 0.63 * mm});
            skCircle(sketch, "E9.17.38.0", {"center": v(-46.72, -132.17) * mm, "radius": 0.63 * mm});
            skCircle(sketch, "E9.19.38.0", {"center": v(-49.26, -132.17) * mm, "radius": 0.63 * mm});
            skCircle(sketch, "E9.21.38.0", {"center": v(-51.8, -132.17) * mm, "radius": 0.63 * mm});
            skLineSegment(sketch, "E9.0.39.0", {"start": v(-51.8, -134.71) * mm, "end": v(-49.26, -134.71) * mm, "construction": true});
            skCircle(sketch, "E9.3.39.0", {"center": v(-28.94, -134.71) * mm, "radius": 0.63 * mm});
            skCircle(sketch, "E9.5.39.0", {"center": v(-31.48, -134.71) * mm, "radius": 0.63 * mm});
            skCircle(sketch, "E9.7.39.0", {"center": v(-34.02, -134.71) * mm, "radius": 0.63 * mm});
            skCircle(sketch, "E9.9.39.0", {"center": v(-36.56, -134.71) * mm, "radius": 0.63 * mm});
            skCircle(sketch, "E9.11.39.0", {"center": v(-39.1, -134.71) * mm, "radius": 0.63 * mm});
            skCircle(sketch, "E9.13.39.0", {"center": v(-41.64, -134.71) * mm, "radius": 0.63 * mm});
            skCircle(sketch, "E9.15.39.0", {"center": v(-44.18, -134.71) * mm, "radius": 0.63 * mm});
            skCircle(sketch, "E9.17.39.0", {"center": v(-46.72, -134.71) * mm, "radius": 0.63 * mm});
            skCircle(sketch, "E9.19.39.0", {"center": v(-49.26, -134.71) * mm, "radius": 0.63 * mm});
            skCircle(sketch, "E9.21.39.0", {"center": v(-51.8, -134.71) * mm, "radius": 0.63 * mm});
            skLineSegment(sketch, "E9.0.40.0", {"start": v(-51.8, -137.25) * mm, "end": v(-49.26, -137.25) * mm, "construction": true});
            skCircle(sketch, "E9.3.40.0", {"center": v(-28.94, -137.25) * mm, "radius": 0.63 * mm});
            skCircle(sketch, "E9.5.40.0", {"center": v(-31.48, -137.25) * mm, "radius": 0.63 * mm});
            skCircle(sketch, "E9.7.40.0", {"center": v(-34.02, -137.25) * mm, "radius": 0.63 * mm});
            skCircle(sketch, "E9.9.40.0", {"center": v(-36.56, -137.25) * mm, "radius": 0.63 * mm});
            skCircle(sketch, "E9.11.40.0", {"center": v(-39.1, -137.25) * mm, "radius": 0.63 * mm});
            skCircle(sketch, "E9.13.40.0", {"center": v(-41.64, -137.25) * mm, "radius": 0.63 * mm});
            skCircle(sketch, "E9.15.40.0", {"center": v(-44.18, -137.25) * mm, "radius": 0.63 * mm});
            skCircle(sketch, "E9.17.40.0", {"center": v(-46.72, -137.25) * mm, "radius": 0.63 * mm});
            skCircle(sketch, "E9.19.40.0", {"center": v(-49.26, -137.25) * mm, "radius": 0.63 * mm});
            skCircle(sketch, "E9.21.40.0", {"center": v(-51.8, -137.25) * mm, "radius": 0.63 * mm});
            skLineSegment(sketch, "E9.0.41.0", {"start": v(-51.8, -139.8) * mm, "end": v(-49.26, -139.8) * mm, "construction": true});
            skCircle(sketch, "E9.3.41.0", {"center": v(-28.94, -139.8) * mm, "radius": 0.63 * mm});
            skCircle(sketch, "E9.5.41.0", {"center": v(-31.48, -139.8) * mm, "radius": 0.63 * mm});
            skCircle(sketch, "E9.7.41.0", {"center": v(-34.02, -139.8) * mm, "radius": 0.63 * mm});
            skCircle(sketch, "E9.9.41.0", {"center": v(-36.56, -139.8) * mm, "radius": 0.63 * mm});
            skCircle(sketch, "E9.11.41.0", {"center": v(-39.1, -139.8) * mm, "radius": 0.63 * mm});
            skCircle(sketch, "E9.13.41.0", {"center": v(-41.64, -139.8) * mm, "radius": 0.63 * mm});
            skCircle(sketch, "E9.15.41.0", {"center": v(-44.18, -139.8) * mm, "radius": 0.63 * mm});
            skCircle(sketch, "E9.17.41.0", {"center": v(-46.72, -139.8) * mm, "radius": 0.63 * mm});
            skCircle(sketch, "E9.19.41.0", {"center": v(-49.26, -139.8) * mm, "radius": 0.63 * mm});
            skCircle(sketch, "E9.21.41.0", {"center": v(-51.8, -139.8) * mm, "radius": 0.63 * mm});
            skLineSegment(sketch, "E9.0.42.0", {"start": v(-51.8, -142.33) * mm, "end": v(-49.26, -142.33) * mm, "construction": true});
            skCircle(sketch, "E9.3.42.0", {"center": v(-28.94, -142.33) * mm, "radius": 0.63 * mm});
            skCircle(sketch, "E9.5.42.0", {"center": v(-31.48, -142.33) * mm, "radius": 0.63 * mm});
            skCircle(sketch, "E9.7.42.0", {"center": v(-34.02, -142.33) * mm, "radius": 0.63 * mm});
            skCircle(sketch, "E9.9.42.0", {"center": v(-36.56, -142.33) * mm, "radius": 0.63 * mm});
            skCircle(sketch, "E9.11.42.0", {"center": v(-39.1, -142.33) * mm, "radius": 0.63 * mm});
            skCircle(sketch, "E9.13.42.0", {"center": v(-41.64, -142.33) * mm, "radius": 0.63 * mm});
            skCircle(sketch, "E9.15.42.0", {"center": v(-44.18, -142.33) * mm, "radius": 0.63 * mm});
            skCircle(sketch, "E9.17.42.0", {"center": v(-46.72, -142.33) * mm, "radius": 0.63 * mm});
            skCircle(sketch, "E9.19.42.0", {"center": v(-49.26, -142.33) * mm, "radius": 0.63 * mm});
            skCircle(sketch, "E9.21.42.0", {"center": v(-51.8, -142.33) * mm, "radius": 0.63 * mm});
            skLineSegment(sketch, "E9.0.43.0", {"start": v(-51.8, -144.87) * mm, "end": v(-49.26, -144.87) * mm, "construction": true});
            skCircle(sketch, "E9.3.43.0", {"center": v(-28.94, -144.87) * mm, "radius": 0.63 * mm});
            skCircle(sketch, "E9.5.43.0", {"center": v(-31.48, -144.87) * mm, "radius": 0.63 * mm});
            skCircle(sketch, "E9.7.43.0", {"center": v(-34.02, -144.87) * mm, "radius": 0.63 * mm});
            skCircle(sketch, "E9.9.43.0", {"center": v(-36.56, -144.87) * mm, "radius": 0.63 * mm});
            skCircle(sketch, "E9.11.43.0", {"center": v(-39.1, -144.87) * mm, "radius": 0.63 * mm});
            skCircle(sketch, "E9.13.43.0", {"center": v(-41.64, -144.87) * mm, "radius": 0.63 * mm});
            skCircle(sketch, "E9.15.43.0", {"center": v(-44.18, -144.87) * mm, "radius": 0.63 * mm});
            skCircle(sketch, "E9.17.43.0", {"center": v(-46.72, -144.87) * mm, "radius": 0.63 * mm});
            skCircle(sketch, "E9.19.43.0", {"center": v(-49.26, -144.87) * mm, "radius": 0.63 * mm});
            skCircle(sketch, "E9.21.43.0", {"center": v(-51.8, -144.87) * mm, "radius": 0.63 * mm});
            skLineSegment(sketch, "E9.0.44.0", {"start": v(-51.8, -147.41) * mm, "end": v(-49.26, -147.41) * mm, "construction": true});
            skCircle(sketch, "E9.3.44.0", {"center": v(-28.94, -147.41) * mm, "radius": 0.63 * mm});
            skCircle(sketch, "E9.5.44.0", {"center": v(-31.48, -147.41) * mm, "radius": 0.63 * mm});
            skCircle(sketch, "E9.7.44.0", {"center": v(-34.02, -147.41) * mm, "radius": 0.63 * mm});
            skCircle(sketch, "E9.9.44.0", {"center": v(-36.56, -147.41) * mm, "radius": 0.63 * mm});
            skCircle(sketch, "E9.11.44.0", {"center": v(-39.1, -147.41) * mm, "radius": 0.63 * mm});
            skCircle(sketch, "E9.13.44.0", {"center": v(-41.64, -147.41) * mm, "radius": 0.63 * mm});
            skCircle(sketch, "E9.15.44.0", {"center": v(-44.18, -147.41) * mm, "radius": 0.63 * mm});
            skCircle(sketch, "E9.17.44.0", {"center": v(-46.72, -147.41) * mm, "radius": 0.63 * mm});
            skCircle(sketch, "E9.19.44.0", {"center": v(-49.26, -147.41) * mm, "radius": 0.63 * mm});
            skCircle(sketch, "E9.21.44.0", {"center": v(-51.8, -147.41) * mm, "radius": 0.63 * mm});
            skLineSegment(sketch, "E9.0.45.0", {"start": v(-51.8, -149.95) * mm, "end": v(-49.26, -149.95) * mm, "construction": true});
            skCircle(sketch, "E9.3.45.0", {"center": v(-28.94, -149.95) * mm, "radius": 0.63 * mm});
            skCircle(sketch, "E9.5.45.0", {"center": v(-31.48, -149.95) * mm, "radius": 0.63 * mm});
            skCircle(sketch, "E9.7.45.0", {"center": v(-34.02, -149.95) * mm, "radius": 0.63 * mm});
            skCircle(sketch, "E9.9.45.0", {"center": v(-36.56, -149.95) * mm, "radius": 0.63 * mm});
            skCircle(sketch, "E9.11.45.0", {"center": v(-39.1, -149.95) * mm, "radius": 0.63 * mm});
            skCircle(sketch, "E9.13.45.0", {"center": v(-41.64, -149.95) * mm, "radius": 0.63 * mm});
            skCircle(sketch, "E9.15.45.0", {"center": v(-44.18, -149.95) * mm, "radius": 0.63 * mm});
            skCircle(sketch, "E9.17.45.0", {"center": v(-46.72, -149.95) * mm, "radius": 0.63 * mm});
            skCircle(sketch, "E9.19.45.0", {"center": v(-49.26, -149.95) * mm, "radius": 0.63 * mm});
            skCircle(sketch, "E9.21.45.0", {"center": v(-51.8, -149.95) * mm, "radius": 0.63 * mm});
            skLineSegment(sketch, "E9.0.46.0", {"start": v(-51.8, -152.5) * mm, "end": v(-49.26, -152.5) * mm, "construction": true});
            skCircle(sketch, "E9.3.46.0", {"center": v(-28.94, -152.5) * mm, "radius": 0.63 * mm});
            skCircle(sketch, "E9.5.46.0", {"center": v(-31.48, -152.5) * mm, "radius": 0.63 * mm});
            skCircle(sketch, "E9.7.46.0", {"center": v(-34.02, -152.5) * mm, "radius": 0.63 * mm});
            skCircle(sketch, "E9.9.46.0", {"center": v(-36.56, -152.5) * mm, "radius": 0.63 * mm});
            skCircle(sketch, "E9.11.46.0", {"center": v(-39.1, -152.5) * mm, "radius": 0.63 * mm});
            skCircle(sketch, "E9.13.46.0", {"center": v(-41.64, -152.5) * mm, "radius": 0.63 * mm});
            skCircle(sketch, "E9.15.46.0", {"center": v(-44.18, -152.5) * mm, "radius": 0.63 * mm});
            skCircle(sketch, "E9.17.46.0", {"center": v(-46.72, -152.5) * mm, "radius": 0.63 * mm});
            skCircle(sketch, "E9.19.46.0", {"center": v(-49.26, -152.5) * mm, "radius": 0.63 * mm});
            skCircle(sketch, "E9.21.46.0", {"center": v(-51.8, -152.5) * mm, "radius": 0.63 * mm});
            skLineSegment(sketch, "E10", {"start": v(-41.64, -94.07) * mm, "end": v(-58.57, -94.07) * mm, "construction": true});
            skLineSegment(sketch, "E11.rect.bottom", {"start": v(-52.75, -154.07) * mm, "end": v(-50.85, -154.07) * mm});
            skLineSegment(sketch, "E11.rect.top", {"start": v(-52.75, -34.07) * mm, "end": v(-50.85, -34.07) * mm});
            skLineSegment(sketch, "E11.rect.left", {"start": v(-52.75, -154.07) * mm, "end": v(-52.75, -34.07) * mm});
            skLineSegment(sketch, "E11.rect.right", {"start": v(-50.85, -154.07) * mm, "end": v(-50.85, -34.07) * mm});
            skLineSegment(sketch, "E12.rect.bottom", {"start": v(-50.2, -154.07) * mm, "end": v(-48.3, -154.07) * mm});
            skLineSegment(sketch, "E12.rect.top", {"start": v(-50.2, -34.07) * mm, "end": v(-48.3, -34.07) * mm});
            skLineSegment(sketch, "E12.rect.left", {"start": v(-50.2, -154.07) * mm, "end": v(-50.2, -34.07) * mm});
            skLineSegment(sketch, "E12.rect.right", {"start": v(-48.3, -154.07) * mm, "end": v(-48.3, -34.07) * mm});
            skLineSegment(sketch, "E13.rect.bottom", {"start": v(-47.67, -154.07) * mm, "end": v(-45.77, -154.07) * mm});
            skLineSegment(sketch, "E13.rect.top", {"start": v(-47.67, -34.07) * mm, "end": v(-45.77, -34.07) * mm});
            skLineSegment(sketch, "E13.rect.left", {"start": v(-47.67, -154.07) * mm, "end": v(-47.67, -34.07) * mm});
            skLineSegment(sketch, "E13.rect.right", {"start": v(-45.77, -154.07) * mm, "end": v(-45.77, -34.07) * mm});
            skLineSegment(sketch, "E14.rect.bottom", {"start": v(-45.13, -154.07) * mm, "end": v(-43.23, -154.07) * mm});
            skLineSegment(sketch, "E14.rect.top", {"start": v(-45.13, -34.07) * mm, "end": v(-43.23, -34.07) * mm});
            skLineSegment(sketch, "E14.rect.left", {"start": v(-45.13, -154.07) * mm, "end": v(-45.13, -34.07) * mm});
            skLineSegment(sketch, "E14.rect.right", {"start": v(-43.23, -154.07) * mm, "end": v(-43.23, -34.07) * mm});
            skLineSegment(sketch, "E15.rect.bottom", {"start": v(-42.59, -154.07) * mm, "end": v(-40.69, -154.07) * mm});
            skLineSegment(sketch, "E15.rect.top", {"start": v(-42.59, -34.07) * mm, "end": v(-40.69, -34.07) * mm});
            skLineSegment(sketch, "E15.rect.left", {"start": v(-42.59, -154.07) * mm, "end": v(-42.59, -34.07) * mm});
            skLineSegment(sketch, "E15.rect.right", {"start": v(-40.69, -154.07) * mm, "end": v(-40.69, -34.07) * mm});
            skLineSegment(sketch, "E16.rect.bottom", {"start": v(-40.05, -154.07) * mm, "end": v(-38.15, -154.07) * mm});
            skLineSegment(sketch, "E16.rect.top", {"start": v(-40.05, -34.07) * mm, "end": v(-38.15, -34.07) * mm});
            skLineSegment(sketch, "E16.rect.left", {"start": v(-40.05, -154.07) * mm, "end": v(-40.05, -34.07) * mm});
            skLineSegment(sketch, "E16.rect.right", {"start": v(-38.15, -154.07) * mm, "end": v(-38.15, -34.07) * mm});
            skLineSegment(sketch, "E17.rect.bottom", {"start": v(-37.5, -154.07) * mm, "end": v(-35.6, -154.07) * mm});
            skLineSegment(sketch, "E17.rect.top", {"start": v(-37.5, -34.07) * mm, "end": v(-35.6, -34.07) * mm});
            skLineSegment(sketch, "E17.rect.left", {"start": v(-37.5, -154.07) * mm, "end": v(-37.5, -34.07) * mm});
            skLineSegment(sketch, "E17.rect.right", {"start": v(-35.6, -154.07) * mm, "end": v(-35.6, -34.07) * mm});
            skLineSegment(sketch, "E18.rect.bottom", {"start": v(-34.97, -154.07) * mm, "end": v(-33.07, -154.07) * mm});
            skLineSegment(sketch, "E18.rect.top", {"start": v(-34.97, -34.07) * mm, "end": v(-33.07, -34.07) * mm});
            skLineSegment(sketch, "E18.rect.left", {"start": v(-34.97, -154.07) * mm, "end": v(-34.97, -34.07) * mm});
            skLineSegment(sketch, "E18.rect.right", {"start": v(-33.07, -154.07) * mm, "end": v(-33.07, -34.07) * mm});
            skLineSegment(sketch, "E19.rect.bottom", {"start": v(-32.43, -154.07) * mm, "end": v(-30.53, -154.07) * mm});
            skLineSegment(sketch, "E19.rect.top", {"start": v(-32.43, -34.07) * mm, "end": v(-30.53, -34.07) * mm});
            skLineSegment(sketch, "E19.rect.left", {"start": v(-32.43, -154.07) * mm, "end": v(-32.43, -34.07) * mm});
            skLineSegment(sketch, "E19.rect.right", {"start": v(-30.53, -154.07) * mm, "end": v(-30.53, -34.07) * mm});
            skLineSegment(sketch, "E20.rect.bottom", {"start": v(-29.89, -154.07) * mm, "end": v(-27.99, -154.07) * mm});
            skLineSegment(sketch, "E20.rect.top", {"start": v(-29.89, -34.07) * mm, "end": v(-27.99, -34.07) * mm});
            skLineSegment(sketch, "E20.rect.left", {"start": v(-29.89, -154.07) * mm, "end": v(-29.89, -34.07) * mm});
            skLineSegment(sketch, "E20.rect.right", {"start": v(-27.99, -154.07) * mm, "end": v(-27.99, -34.07) * mm});
            skCircle(sketch, "E21.5.30.0", {"center": v(-28.93, -111.85) * mm, "radius": 0.63 * mm});
            skLineSegment(sketch, "E22", {"start": v(-52.75, -154.07) * mm, "end": v(-27.99, -154.07) * mm});
            skLineSegment(sketch, "E23", {"start": v(-51.8, -152.5) * mm, "end": v(-51.8, -155) * mm});
            skLineSegment(sketch, "E24", {"start": v(-51.8, -155) * mm, "end": v(-28.93, -155) * mm});
            skLineSegment(sketch, "E25", {"start": v(-28.93, -155) * mm, "end": v(-28.93, -152.5) * mm});
            skLineSegment(sketch, "E26", {"start": v(-28.93, -61.4) * mm, "end": v(-28.93, -33.15) * mm});
            skSolve(sketch);
        }
        {
            var Q0;
            {var subQ14=sQuery(id+"F0.wireOp",EDGE,"E24");Q0=makeQuery(id+"F0.imprint","IMPRINT",FACE,{"disambiguationData":[TD([[makeQuery(id+"F0.imprint","IMPRINT",EDGE,{"derivedFrom":subQ14}),1.0]])]});}
            var Q1;
            {var subQ1=sQuery(id+"F0.wireOp",EDGE,"E11.rect.right");var subQ5=sQuery(id+"F0.wireOp",EDGE,"E6");var subQ6=makeQuery(id+"F0.imprint","INTERSECT",VERTEX,{"derivedFrom":[subQ5,subQ1]});Q1=makeQuery(id+"F0.imprint","IMPRINT",FACE,{"disambiguationData":[TD([[makeQuery(id+"F0.imprint","IMPRINT",EDGE,{"disambiguationData":[TD([[subQ6,-1.0]])],"derivedFrom":subQ5}),1.0]])]});}
            var Q2;
            {var subQ33=sQuery(id+"F0.wireOp",EDGE,"E0");var subQ39=sQuery(id+"F0.wireOp",EDGE,"E3");var subQ77=makeQuery(id+"F0.imprint","INTERSECT",VERTEX,{"derivedFrom":[subQ33,subQ39]});Q2=makeQuery(id+"F0.imprint","IMPRINT",FACE,{"disambiguationData":[TD([[makeQuery(id+"F0.imprint","IMPRINT",EDGE,{"disambiguationData":[TD([[subQ77,-1.0]])],"derivedFrom":subQ33}),-1.0]])]});}
            var Q3;
            {var subQ0=sQuery(id+"F0.wireOp",EDGE,"E12.rect.left");var subQ1=sQuery(id+"F0.wireOp",EDGE,"E6");var subQ2=makeQuery(id+"F0.imprint","INTERSECT",VERTEX,{"derivedFrom":[subQ1,subQ0]});Q3=makeQuery(id+"F0.imprint","IMPRINT",FACE,{"disambiguationData":[TD([[makeQuery(id+"F0.imprint","IMPRINT",EDGE,{"disambiguationData":[TD([[subQ2,-1.0]])],"derivedFrom":subQ1}),1.0]])]});}
            var Q4;
            {var subQ20=sQuery(id+"F0.wireOp",EDGE,"E4");Q4=makeQuery(id+"F0.imprint","IMPRINT",FACE,{"disambiguationData":[TD([[makeQuery(id+"F0.imprint","IMPRINT",EDGE,{"derivedFrom":subQ20}),1.0]])]});}
            var Q5;
            {var subQ3=sQuery(id+"F0.wireOp",EDGE,"E6");var subQ5=sQuery(id+"F0.wireOp",EDGE,"E12.rect.right");var subQ10=makeQuery(id+"F0.imprint","INTERSECT",VERTEX,{"derivedFrom":[subQ3,subQ5]});Q5=makeQuery(id+"F0.imprint","IMPRINT",FACE,{"disambiguationData":[TD([[makeQuery(id+"F0.imprint","IMPRINT",EDGE,{"disambiguationData":[TD([[subQ10,-1.0]])],"derivedFrom":subQ3}),1.0]])]});}
            var Q6;
            Q6=makeQuery(id+"F0.imprint","IMPRINT",FACE,{"disambiguationData":[TD([[makeQuery(id+"F0.imprint","IMPRINT",EDGE,{"derivedFrom":sQuery(id+"F0.wireOp",EDGE,"E1.1.0.0")}),-1.0]])]});
            var Q7;
            {var subQ0=sQuery(id+"F0.wireOp",EDGE,"E13.rect.left");var subQ1=sQuery(id+"F0.wireOp",EDGE,"E6");var subQ2=makeQuery(id+"F0.imprint","INTERSECT",VERTEX,{"derivedFrom":[subQ1,subQ0]});Q7=makeQuery(id+"F0.imprint","IMPRINT",FACE,{"disambiguationData":[TD([[makeQuery(id+"F0.imprint","IMPRINT",EDGE,{"disambiguationData":[TD([[subQ2,-1.0]])],"derivedFrom":subQ1}),1.0]])]});}
            var Q8;
            {var subQ3=sQuery(id+"F0.wireOp",EDGE,"E6");var subQ8=sQuery(id+"F0.wireOp",EDGE,"E13.rect.right");var subQ10=makeQuery(id+"F0.imprint","INTERSECT",VERTEX,{"derivedFrom":[subQ3,subQ8]});Q8=makeQuery(id+"F0.imprint","IMPRINT",FACE,{"disambiguationData":[TD([[makeQuery(id+"F0.imprint","IMPRINT",EDGE,{"disambiguationData":[TD([[subQ10,-1.0]])],"derivedFrom":subQ3}),1.0]])]});}
            var Q9;
            Q9=makeQuery(id+"F0.imprint","IMPRINT",FACE,{"disambiguationData":[TD([[makeQuery(id+"F0.imprint","IMPRINT",EDGE,{"derivedFrom":sQuery(id+"F0.wireOp",EDGE,"E1.2.0.0")}),-1.0]])]});
            var Q10;
            {var subQ0=sQuery(id+"F0.wireOp",EDGE,"E14.rect.left");var subQ1=sQuery(id+"F0.wireOp",EDGE,"E6");var subQ2=makeQuery(id+"F0.imprint","INTERSECT",VERTEX,{"derivedFrom":[subQ1,subQ0]});Q10=makeQuery(id+"F0.imprint","IMPRINT",FACE,{"disambiguationData":[TD([[makeQuery(id+"F0.imprint","IMPRINT",EDGE,{"disambiguationData":[TD([[subQ2,-1.0]])],"derivedFrom":subQ1}),1.0]])]});}
            var Q11;
            {var subQ3=sQuery(id+"F0.wireOp",EDGE,"E6");var subQ8=sQuery(id+"F0.wireOp",EDGE,"E14.rect.right");var subQ9=makeQuery(id+"F0.imprint","INTERSECT",VERTEX,{"derivedFrom":[subQ3,subQ8]});Q11=makeQuery(id+"F0.imprint","IMPRINT",FACE,{"disambiguationData":[TD([[makeQuery(id+"F0.imprint","IMPRINT",EDGE,{"disambiguationData":[TD([[subQ9,-1.0]])],"derivedFrom":subQ3}),1.0]])]});}
            var Q12;
            Q12=makeQuery(id+"F0.imprint","IMPRINT",FACE,{"disambiguationData":[TD([[makeQuery(id+"F0.imprint","IMPRINT",EDGE,{"derivedFrom":sQuery(id+"F0.wireOp",EDGE,"E1.3.0.0")}),-1.0]])]});
            var Q13;
            {var subQ0=sQuery(id+"F0.wireOp",EDGE,"E15.rect.left");var subQ1=sQuery(id+"F0.wireOp",EDGE,"E6");var subQ2=makeQuery(id+"F0.imprint","INTERSECT",VERTEX,{"derivedFrom":[subQ1,subQ0]});Q13=makeQuery(id+"F0.imprint","IMPRINT",FACE,{"disambiguationData":[TD([[makeQuery(id+"F0.imprint","IMPRINT",EDGE,{"disambiguationData":[TD([[subQ2,-1.0]])],"derivedFrom":subQ1}),1.0]])]});}
            var Q14;
            {var subQ3=sQuery(id+"F0.wireOp",EDGE,"E6");var subQ8=sQuery(id+"F0.wireOp",EDGE,"E15.rect.right");var subQ9=makeQuery(id+"F0.imprint","INTERSECT",VERTEX,{"derivedFrom":[subQ3,subQ8]});Q14=makeQuery(id+"F0.imprint","IMPRINT",FACE,{"disambiguationData":[TD([[makeQuery(id+"F0.imprint","IMPRINT",EDGE,{"disambiguationData":[TD([[subQ9,-1.0]])],"derivedFrom":subQ3}),1.0]])]});}
            var Q15;
            Q15=makeQuery(id+"F0.imprint","IMPRINT",FACE,{"disambiguationData":[TD([[makeQuery(id+"F0.imprint","IMPRINT",EDGE,{"derivedFrom":sQuery(id+"F0.wireOp",EDGE,"E1.4.0.0")}),-1.0]])]});
            var Q16;
            {var subQ0=sQuery(id+"F0.wireOp",EDGE,"E16.rect.left");var subQ1=sQuery(id+"F0.wireOp",EDGE,"E6");var subQ2=makeQuery(id+"F0.imprint","INTERSECT",VERTEX,{"derivedFrom":[subQ1,subQ0]});Q16=makeQuery(id+"F0.imprint","IMPRINT",FACE,{"disambiguationData":[TD([[makeQuery(id+"F0.imprint","IMPRINT",EDGE,{"disambiguationData":[TD([[subQ2,-1.0]])],"derivedFrom":subQ1}),1.0]])]});}
            var Q17;
            {var subQ0=sQuery(id+"F0.wireOp",EDGE,"E17.rect.left");var subQ1=sQuery(id+"F0.wireOp",EDGE,"E6");var subQ2=makeQuery(id+"F0.imprint","INTERSECT",VERTEX,{"derivedFrom":[subQ1,subQ0]});Q17=makeQuery(id+"F0.imprint","IMPRINT",FACE,{"disambiguationData":[TD([[makeQuery(id+"F0.imprint","IMPRINT",EDGE,{"disambiguationData":[TD([[subQ2,-1.0]])],"derivedFrom":subQ1}),1.0]])]});}
            var Q18;
            {var subQ3=sQuery(id+"F0.wireOp",EDGE,"E6");var subQ8=sQuery(id+"F0.wireOp",EDGE,"E16.rect.right");var subQ9=makeQuery(id+"F0.imprint","INTERSECT",VERTEX,{"derivedFrom":[subQ3,subQ8]});Q18=makeQuery(id+"F0.imprint","IMPRINT",FACE,{"disambiguationData":[TD([[makeQuery(id+"F0.imprint","IMPRINT",EDGE,{"disambiguationData":[TD([[subQ9,-1.0]])],"derivedFrom":subQ3}),1.0]])]});}
            var Q19;
            Q19=makeQuery(id+"F0.imprint","IMPRINT",FACE,{"disambiguationData":[TD([[makeQuery(id+"F0.imprint","IMPRINT",EDGE,{"derivedFrom":sQuery(id+"F0.wireOp",EDGE,"E1.5.0.0")}),-1.0]])]});
            var Q20;
            {var subQ3=sQuery(id+"F0.wireOp",EDGE,"E6");var subQ8=sQuery(id+"F0.wireOp",EDGE,"E17.rect.right");var subQ9=makeQuery(id+"F0.imprint","INTERSECT",VERTEX,{"derivedFrom":[subQ3,subQ8]});Q20=makeQuery(id+"F0.imprint","IMPRINT",FACE,{"disambiguationData":[TD([[makeQuery(id+"F0.imprint","IMPRINT",EDGE,{"disambiguationData":[TD([[subQ9,-1.0]])],"derivedFrom":subQ3}),1.0]])]});}
            var Q21;
            Q21=makeQuery(id+"F0.imprint","IMPRINT",FACE,{"disambiguationData":[TD([[makeQuery(id+"F0.imprint","IMPRINT",EDGE,{"derivedFrom":sQuery(id+"F0.wireOp",EDGE,"E1.6.0.0")}),-1.0]])]});
            var Q22;
            {var subQ0=sQuery(id+"F0.wireOp",EDGE,"E18.rect.left");var subQ1=sQuery(id+"F0.wireOp",EDGE,"E6");var subQ2=makeQuery(id+"F0.imprint","INTERSECT",VERTEX,{"derivedFrom":[subQ1,subQ0]});Q22=makeQuery(id+"F0.imprint","IMPRINT",FACE,{"disambiguationData":[TD([[makeQuery(id+"F0.imprint","IMPRINT",EDGE,{"disambiguationData":[TD([[subQ2,-1.0]])],"derivedFrom":subQ1}),1.0]])]});}
            var Q23;
            {var subQ3=sQuery(id+"F0.wireOp",EDGE,"E6");var subQ8=sQuery(id+"F0.wireOp",EDGE,"E18.rect.right");var subQ10=makeQuery(id+"F0.imprint","INTERSECT",VERTEX,{"derivedFrom":[subQ3,subQ8]});Q23=makeQuery(id+"F0.imprint","IMPRINT",FACE,{"disambiguationData":[TD([[makeQuery(id+"F0.imprint","IMPRINT",EDGE,{"disambiguationData":[TD([[subQ10,-1.0]])],"derivedFrom":subQ3}),1.0]])]});}
            var Q24;
            Q24=makeQuery(id+"F0.imprint","IMPRINT",FACE,{"disambiguationData":[TD([[makeQuery(id+"F0.imprint","IMPRINT",EDGE,{"derivedFrom":sQuery(id+"F0.wireOp",EDGE,"E1.7.0.0")}),-1.0]])]});
            var Q25;
            {var subQ3=sQuery(id+"F0.wireOp",EDGE,"E6");var subQ8=sQuery(id+"F0.wireOp",EDGE,"E19.rect.right");var subQ9=makeQuery(id+"F0.imprint","INTERSECT",VERTEX,{"derivedFrom":[subQ3,subQ8]});Q25=makeQuery(id+"F0.imprint","IMPRINT",FACE,{"disambiguationData":[TD([[makeQuery(id+"F0.imprint","IMPRINT",EDGE,{"disambiguationData":[TD([[subQ9,-1.0]])],"derivedFrom":subQ3}),1.0]])]});}
            var Q26;
            Q26=makeQuery(id+"F0.imprint","IMPRINT",FACE,{"disambiguationData":[TD([[makeQuery(id+"F0.imprint","IMPRINT",EDGE,{"derivedFrom":sQuery(id+"F0.wireOp",EDGE,"E1.8.0.0")}),-1.0]])]});
            var Q27;
            {var subQ0=sQuery(id+"F0.wireOp",EDGE,"E20.rect.left");var subQ1=sQuery(id+"F0.wireOp",EDGE,"E6");var subQ2=makeQuery(id+"F0.imprint","INTERSECT",VERTEX,{"derivedFrom":[subQ1,subQ0]});Q27=makeQuery(id+"F0.imprint","IMPRINT",FACE,{"disambiguationData":[TD([[makeQuery(id+"F0.imprint","IMPRINT",EDGE,{"disambiguationData":[TD([[subQ2,-1.0]])],"derivedFrom":subQ1}),1.0]])]});}
            var Q28;
            {var subQ5=sQuery(id+"F0.wireOp",EDGE,"E6");var subQ7=sQuery(id+"F0.wireOp",EDGE,"E9.3.46.0");var subQ9=makeQuery(id+"F0.imprint","INTERSECT",VERTEX,{"derivedFrom":[subQ5,subQ7]});Q28=makeQuery(id+"F0.imprint","IMPRINT",FACE,{"disambiguationData":[TD([[makeQuery(id+"F0.imprint","IMPRINT",EDGE,{"disambiguationData":[TD([[subQ9,-1.0]])],"derivedFrom":subQ5}),1.0]])]});}
            var Q29;
            {var subQ39=sQuery(id+"F0.wireOp",EDGE,"JgwjaH20-m7XH-zVhQ-8Puc-2S3nrI6lC1iW");var subQ53=sQuery(id+"F0.wireOp",EDGE,"E1.9.0.0");var subQ54=makeQuery(id+"F0.imprint","INTERSECT",VERTEX,{"derivedFrom":[subQ53,subQ39]});Q29=makeQuery(id+"F0.imprint","IMPRINT",FACE,{"disambiguationData":[TD([[makeQuery(id+"F0.imprint","IMPRINT",EDGE,{"disambiguationData":[TD([[subQ54,1.0]])],"derivedFrom":subQ53}),-1.0]])]});}
            var Q30;
            {var subQ0=sQuery(id+"F0.wireOp",EDGE,"E19.rect.left");var subQ1=sQuery(id+"F0.wireOp",EDGE,"E6");var subQ2=makeQuery(id+"F0.imprint","INTERSECT",VERTEX,{"derivedFrom":[subQ1,subQ0]});Q30=makeQuery(id+"F0.imprint","IMPRINT",FACE,{"disambiguationData":[TD([[makeQuery(id+"F0.imprint","IMPRINT",EDGE,{"disambiguationData":[TD([[subQ2,-1.0]])],"derivedFrom":subQ1}),1.0]])]});}
            extrude(context, id + "F1", {"entities" : qUnion([Q0, Q1, Q2, Q3, Q4, Q5, Q6, Q7, Q8, Q9, Q10, Q11, Q12, Q13, Q14, Q15, Q16, Q17, Q18, Q19, Q20, Q21, Q22, Q23, Q24, Q25, Q26, Q27, Q28, Q29, Q30]), "oppositeDirection" : true, "depth" : 1.9 * mm});
        }
        {
            var Q0;
            Q0=makeQuery(id+"F0.imprint","IMPRINT",FACE,{"disambiguationData":[TD([[makeQuery(id+"F0.imprint","IMPRINT",EDGE,{"derivedFrom":sQuery(id+"F0.wireOp",EDGE,"E1.1.0.0")}),-1.0]])]});
            var Q1;
            {var subQ33=sQuery(id+"F0.wireOp",EDGE,"E0");var subQ39=sQuery(id+"F0.wireOp",EDGE,"E3");var subQ77=makeQuery(id+"F0.imprint","INTERSECT",VERTEX,{"derivedFrom":[subQ33,subQ39]});Q1=makeQuery(id+"F0.imprint","IMPRINT",FACE,{"disambiguationData":[TD([[makeQuery(id+"F0.imprint","IMPRINT",EDGE,{"disambiguationData":[TD([[subQ77,-1.0]])],"derivedFrom":subQ33}),-1.0]])]});}
            var Q2;
            Q2=makeQuery(id+"F0.imprint","IMPRINT",FACE,{"disambiguationData":[TD([[makeQuery(id+"F0.imprint","IMPRINT",EDGE,{"derivedFrom":sQuery(id+"F0.wireOp",EDGE,"E1.2.0.0")}),-1.0]])]});
            var Q3;
            Q3=makeQuery(id+"F0.imprint","IMPRINT",FACE,{"disambiguationData":[TD([[makeQuery(id+"F0.imprint","IMPRINT",EDGE,{"derivedFrom":sQuery(id+"F0.wireOp",EDGE,"E1.3.0.0")}),-1.0]])]});
            var Q4;
            Q4=makeQuery(id+"F0.imprint","IMPRINT",FACE,{"disambiguationData":[TD([[makeQuery(id+"F0.imprint","IMPRINT",EDGE,{"derivedFrom":sQuery(id+"F0.wireOp",EDGE,"E1.4.0.0")}),-1.0]])]});
            var Q5;
            Q5=makeQuery(id+"F0.imprint","IMPRINT",FACE,{"disambiguationData":[TD([[makeQuery(id+"F0.imprint","IMPRINT",EDGE,{"derivedFrom":sQuery(id+"F0.wireOp",EDGE,"E1.5.0.0")}),-1.0]])]});
            var Q6;
            Q6=makeQuery(id+"F0.imprint","IMPRINT",FACE,{"disambiguationData":[TD([[makeQuery(id+"F0.imprint","IMPRINT",EDGE,{"derivedFrom":sQuery(id+"F0.wireOp",EDGE,"E1.6.0.0")}),-1.0]])]});
            var Q7;
            Q7=makeQuery(id+"F0.imprint","IMPRINT",FACE,{"disambiguationData":[TD([[makeQuery(id+"F0.imprint","IMPRINT",EDGE,{"derivedFrom":sQuery(id+"F0.wireOp",EDGE,"E1.7.0.0")}),-1.0]])]});
            var Q8;
            Q8=makeQuery(id+"F0.imprint","IMPRINT",FACE,{"disambiguationData":[TD([[makeQuery(id+"F0.imprint","IMPRINT",EDGE,{"derivedFrom":sQuery(id+"F0.wireOp",EDGE,"E1.8.0.0")}),-1.0]])]});
            var Q9;
            {var subQ39=sQuery(id+"F0.wireOp",EDGE,"JgwjaH20-m7XH-zVhQ-8Puc-2S3nrI6lC1iW");var subQ53=sQuery(id+"F0.wireOp",EDGE,"E1.9.0.0");var subQ54=makeQuery(id+"F0.imprint","INTERSECT",VERTEX,{"derivedFrom":[subQ53,subQ39]});Q9=makeQuery(id+"F0.imprint","IMPRINT",FACE,{"disambiguationData":[TD([[makeQuery(id+"F0.imprint","IMPRINT",EDGE,{"disambiguationData":[TD([[subQ54,1.0]])],"derivedFrom":subQ53}),-1.0]])]});}
            var Q10;
            {var subQ1=sQuery(id+"F0.wireOp",EDGE,"E11.rect.right");var subQ5=sQuery(id+"F0.wireOp",EDGE,"E6");var subQ6=makeQuery(id+"F0.imprint","INTERSECT",VERTEX,{"derivedFrom":[subQ5,subQ1]});Q10=makeQuery(id+"F0.imprint","IMPRINT",FACE,{"disambiguationData":[TD([[makeQuery(id+"F0.imprint","IMPRINT",EDGE,{"disambiguationData":[TD([[subQ6,-1.0]])],"derivedFrom":subQ5}),1.0]])]});}
            var Q11;
            {var subQ3=sQuery(id+"F0.wireOp",EDGE,"E6");var subQ5=sQuery(id+"F0.wireOp",EDGE,"E12.rect.right");var subQ10=makeQuery(id+"F0.imprint","INTERSECT",VERTEX,{"derivedFrom":[subQ3,subQ5]});Q11=makeQuery(id+"F0.imprint","IMPRINT",FACE,{"disambiguationData":[TD([[makeQuery(id+"F0.imprint","IMPRINT",EDGE,{"disambiguationData":[TD([[subQ10,-1.0]])],"derivedFrom":subQ3}),1.0]])]});}
            var Q12;
            {var subQ3=sQuery(id+"F0.wireOp",EDGE,"E6");var subQ8=sQuery(id+"F0.wireOp",EDGE,"E13.rect.right");var subQ10=makeQuery(id+"F0.imprint","INTERSECT",VERTEX,{"derivedFrom":[subQ3,subQ8]});Q12=makeQuery(id+"F0.imprint","IMPRINT",FACE,{"disambiguationData":[TD([[makeQuery(id+"F0.imprint","IMPRINT",EDGE,{"disambiguationData":[TD([[subQ10,-1.0]])],"derivedFrom":subQ3}),1.0]])]});}
            var Q13;
            {var subQ3=sQuery(id+"F0.wireOp",EDGE,"E6");var subQ8=sQuery(id+"F0.wireOp",EDGE,"E14.rect.right");var subQ9=makeQuery(id+"F0.imprint","INTERSECT",VERTEX,{"derivedFrom":[subQ3,subQ8]});Q13=makeQuery(id+"F0.imprint","IMPRINT",FACE,{"disambiguationData":[TD([[makeQuery(id+"F0.imprint","IMPRINT",EDGE,{"disambiguationData":[TD([[subQ9,-1.0]])],"derivedFrom":subQ3}),1.0]])]});}
            var Q14;
            {var subQ3=sQuery(id+"F0.wireOp",EDGE,"E6");var subQ8=sQuery(id+"F0.wireOp",EDGE,"E15.rect.right");var subQ9=makeQuery(id+"F0.imprint","INTERSECT",VERTEX,{"derivedFrom":[subQ3,subQ8]});Q14=makeQuery(id+"F0.imprint","IMPRINT",FACE,{"disambiguationData":[TD([[makeQuery(id+"F0.imprint","IMPRINT",EDGE,{"disambiguationData":[TD([[subQ9,-1.0]])],"derivedFrom":subQ3}),1.0]])]});}
            var Q15;
            {var subQ3=sQuery(id+"F0.wireOp",EDGE,"E6");var subQ8=sQuery(id+"F0.wireOp",EDGE,"E16.rect.right");var subQ9=makeQuery(id+"F0.imprint","INTERSECT",VERTEX,{"derivedFrom":[subQ3,subQ8]});Q15=makeQuery(id+"F0.imprint","IMPRINT",FACE,{"disambiguationData":[TD([[makeQuery(id+"F0.imprint","IMPRINT",EDGE,{"disambiguationData":[TD([[subQ9,-1.0]])],"derivedFrom":subQ3}),1.0]])]});}
            var Q16;
            {var subQ3=sQuery(id+"F0.wireOp",EDGE,"E6");var subQ8=sQuery(id+"F0.wireOp",EDGE,"E17.rect.right");var subQ9=makeQuery(id+"F0.imprint","INTERSECT",VERTEX,{"derivedFrom":[subQ3,subQ8]});Q16=makeQuery(id+"F0.imprint","IMPRINT",FACE,{"disambiguationData":[TD([[makeQuery(id+"F0.imprint","IMPRINT",EDGE,{"disambiguationData":[TD([[subQ9,-1.0]])],"derivedFrom":subQ3}),1.0]])]});}
            var Q17;
            {var subQ3=sQuery(id+"F0.wireOp",EDGE,"E6");var subQ8=sQuery(id+"F0.wireOp",EDGE,"E18.rect.right");var subQ10=makeQuery(id+"F0.imprint","INTERSECT",VERTEX,{"derivedFrom":[subQ3,subQ8]});Q17=makeQuery(id+"F0.imprint","IMPRINT",FACE,{"disambiguationData":[TD([[makeQuery(id+"F0.imprint","IMPRINT",EDGE,{"disambiguationData":[TD([[subQ10,-1.0]])],"derivedFrom":subQ3}),1.0]])]});}
            var Q18;
            {var subQ3=sQuery(id+"F0.wireOp",EDGE,"E6");var subQ8=sQuery(id+"F0.wireOp",EDGE,"E19.rect.right");var subQ9=makeQuery(id+"F0.imprint","INTERSECT",VERTEX,{"derivedFrom":[subQ3,subQ8]});Q18=makeQuery(id+"F0.imprint","IMPRINT",FACE,{"disambiguationData":[TD([[makeQuery(id+"F0.imprint","IMPRINT",EDGE,{"disambiguationData":[TD([[subQ9,-1.0]])],"derivedFrom":subQ3}),1.0]])]});}
            var Q19;
            {var subQ5=sQuery(id+"F0.wireOp",EDGE,"E6");var subQ7=sQuery(id+"F0.wireOp",EDGE,"E9.3.46.0");var subQ9=makeQuery(id+"F0.imprint","INTERSECT",VERTEX,{"derivedFrom":[subQ5,subQ7]});Q19=makeQuery(id+"F0.imprint","IMPRINT",FACE,{"disambiguationData":[TD([[makeQuery(id+"F0.imprint","IMPRINT",EDGE,{"disambiguationData":[TD([[subQ9,-1.0]])],"derivedFrom":subQ5}),1.0]])]});}
            extrude(context, id + "F2", {"entities" : qUnion([Q0, Q1, Q2, Q3, Q4, Q5, Q6, Q7, Q8, Q9, Q10, Q11, Q12, Q13, Q14, Q15, Q16, Q17, Q18, Q19]), "depth" : 0.25 * mm});
        }
        {
            var Q0;
            Q0=makeQuery(id+"F1.opExtrude","SWEPT_BODY",BODY,{"disambiguationData":[OSD([sQuery(id+"F0.wireOp",EDGE,"E0"),sQuery(id+"F0.wireOp",EDGE,"E1.1.0.0"),sQuery(id+"F0.wireOp",EDGE,"E1.2.0.0"),sQuery(id+"F0.wireOp",EDGE,"E1.3.0.0"),sQuery(id+"F0.wireOp",EDGE,"E1.4.0.0"),sQuery(id+"F0.wireOp",EDGE,"E1.5.0.0"),sQuery(id+"F0.wireOp",EDGE,"E1.6.0.0"),sQuery(id+"F0.wireOp",EDGE,"E1.7.0.0"),sQuery(id+"F0.wireOp",EDGE,"E1.8.0.0"),sQuery(id+"F0.wireOp",EDGE,"E1.9.0.0"),sQuery(id+"F0.wireOp",EDGE,"E2.1.0.1"),sQuery(id+"F0.wireOp",EDGE,"E2.1.0.2"),sQuery(id+"F0.wireOp",EDGE,"E2.1.0.3"),sQuery(id+"F0.wireOp",EDGE,"E2.1.0.4"),sQuery(id+"F0.wireOp",EDGE,"E2.1.0.5"),sQuery(id+"F0.wireOp",EDGE,"E2.1.0.6"),sQuery(id+"F0.wireOp",EDGE,"E2.1.0.7"),sQuery(id+"F0.wireOp",EDGE,"E2.1.0.8"),sQuery(id+"F0.wireOp",EDGE,"E2.1.0.9"),sQuery(id+"F0.wireOp",EDGE,"E2.1.0.10"),sQuery(id+"F0.wireOp",EDGE,"E2.2.0.1"),sQuery(id+"F0.wireOp",EDGE,"E2.2.0.2"),sQuery(id+"F0.wireOp",EDGE,"E2.2.0.3"),sQuery(id+"F0.wireOp",EDGE,"E2.2.0.4"),sQuery(id+"F0.wireOp",EDGE,"E2.2.0.5"),sQuery(id+"F0.wireOp",EDGE,"E2.2.0.6"),sQuery(id+"F0.wireOp",EDGE,"E2.2.0.7"),sQuery(id+"F0.wireOp",EDGE,"E2.2.0.8"),sQuery(id+"F0.wireOp",EDGE,"E2.2.0.9"),sQuery(id+"F0.wireOp",EDGE,"E2.2.0.10"),sQuery(id+"F0.wireOp",EDGE,"E2.3.0.1"),sQuery(id+"F0.wireOp",EDGE,"E2.3.0.2"),sQuery(id+"F0.wireOp",EDGE,"E2.3.0.3"),sQuery(id+"F0.wireOp",EDGE,"E2.3.0.4"),sQuery(id+"F0.wireOp",EDGE,"E2.3.0.5"),sQuery(id+"F0.wireOp",EDGE,"E2.3.0.6"),sQuery(id+"F0.wireOp",EDGE,"E2.3.0.7"),sQuery(id+"F0.wireOp",EDGE,"E2.3.0.8"),sQuery(id+"F0.wireOp",EDGE,"E2.3.0.9"),sQuery(id+"F0.wireOp",EDGE,"E2.3.0.10"),sQuery(id+"F0.wireOp",EDGE,"E2.4.0.1"),sQuery(id+"F0.wireOp",EDGE,"E2.4.0.2"),sQuery(id+"F0.wireOp",EDGE,"E2.4.0.3"),sQuery(id+"F0.wireOp",EDGE,"E2.4.0.4"),sQuery(id+"F0.wireOp",EDGE,"E2.4.0.5"),sQuery(id+"F0.wireOp",EDGE,"E2.4.0.6"),sQuery(id+"F0.wireOp",EDGE,"E2.4.0.7"),sQuery(id+"F0.wireOp",EDGE,"E2.4.0.8"),sQuery(id+"F0.wireOp",EDGE,"E2.4.0.9"),sQuery(id+"F0.wireOp",EDGE,"E2.4.0.10"),sQuery(id+"F0.wireOp",EDGE,"E2.5.0.1"),sQuery(id+"F0.wireOp",EDGE,"E2.5.0.2"),sQuery(id+"F0.wireOp",EDGE,"E2.5.0.3"),sQuery(id+"F0.wireOp",EDGE,"E2.5.0.4"),sQuery(id+"F0.wireOp",EDGE,"E2.5.0.5"),sQuery(id+"F0.wireOp",EDGE,"E2.5.0.6"),sQuery(id+"F0.wireOp",EDGE,"E2.5.0.7"),sQuery(id+"F0.wireOp",EDGE,"E2.5.0.8"),sQuery(id+"F0.wireOp",EDGE,"E2.5.0.9"),sQuery(id+"F0.wireOp",EDGE,"E2.5.0.10"),sQuery(id+"F0.wireOp",EDGE,"E2.6.0.1"),sQuery(id+"F0.wireOp",EDGE,"E2.6.0.2"),sQuery(id+"F0.wireOp",EDGE,"E2.6.0.3"),sQuery(id+"F0.wireOp",EDGE,"E2.6.0.4"),sQuery(id+"F0.wireOp",EDGE,"E2.6.0.5"),sQuery(id+"F0.wireOp",EDGE,"E2.6.0.6"),sQuery(id+"F0.wireOp",EDGE,"E2.6.0.7"),sQuery(id+"F0.wireOp",EDGE,"E2.6.0.8"),sQuery(id+"F0.wireOp",EDGE,"E2.6.0.9"),sQuery(id+"F0.wireOp",EDGE,"E2.6.0.10"),sQuery(id+"F0.wireOp",EDGE,"E2.7.0.1"),sQuery(id+"F0.wireOp",EDGE,"E2.7.0.2"),sQuery(id+"F0.wireOp",EDGE,"E2.7.0.3"),sQuery(id+"F0.wireOp",EDGE,"E2.7.0.4"),sQuery(id+"F0.wireOp",EDGE,"E2.7.0.5"),sQuery(id+"F0.wireOp",EDGE,"E2.7.0.6"),sQuery(id+"F0.wireOp",EDGE,"E2.7.0.7"),sQuery(id+"F0.wireOp",EDGE,"E2.7.0.8"),sQuery(id+"F0.wireOp",EDGE,"E2.7.0.9"),sQuery(id+"F0.wireOp",EDGE,"E2.7.0.10"),sQuery(id+"F0.wireOp",EDGE,"E2.8.0.1"),sQuery(id+"F0.wireOp",EDGE,"E2.8.0.2"),sQuery(id+"F0.wireOp",EDGE,"E2.8.0.3"),sQuery(id+"F0.wireOp",EDGE,"E2.8.0.4"),sQuery(id+"F0.wireOp",EDGE,"E2.8.0.5"),sQuery(id+"F0.wireOp",EDGE,"E2.8.0.6"),sQuery(id+"F0.wireOp",EDGE,"E2.8.0.7"),sQuery(id+"F0.wireOp",EDGE,"E2.8.0.8"),sQuery(id+"F0.wireOp",EDGE,"E2.8.0.9"),sQuery(id+"F0.wireOp",EDGE,"E2.8.0.10"),sQuery(id+"F0.wireOp",EDGE,"E2.9.0.1"),sQuery(id+"F0.wireOp",EDGE,"E2.9.0.2"),sQuery(id+"F0.wireOp",EDGE,"E2.9.0.3"),sQuery(id+"F0.wireOp",EDGE,"E2.9.0.4"),sQuery(id+"F0.wireOp",EDGE,"E2.9.0.5"),sQuery(id+"F0.wireOp",EDGE,"E2.9.0.6"),sQuery(id+"F0.wireOp",EDGE,"E2.9.0.7"),sQuery(id+"F0.wireOp",EDGE,"E2.9.0.8"),sQuery(id+"F0.wireOp",EDGE,"E2.9.0.9"),sQuery(id+"F0.wireOp",EDGE,"E2.9.0.10"),sQuery(id+"F0.wireOp",EDGE,"E2.10.0.1"),sQuery(id+"F0.wireOp",EDGE,"E2.10.0.2"),sQuery(id+"F0.wireOp",EDGE,"E2.10.0.3"),sQuery(id+"F0.wireOp",EDGE,"E2.10.0.4"),sQuery(id+"F0.wireOp",EDGE,"E2.10.0.5"),sQuery(id+"F0.wireOp",EDGE,"E2.10.0.6"),sQuery(id+"F0.wireOp",EDGE,"E2.10.0.7"),sQuery(id+"F0.wireOp",EDGE,"E2.10.0.8"),sQuery(id+"F0.wireOp",EDGE,"E2.10.0.9"),sQuery(id+"F0.wireOp",EDGE,"E2.10.0.10"),sQuery(id+"F0.wireOp",EDGE,"E2.11.0.1"),sQuery(id+"F0.wireOp",EDGE,"E2.11.0.2"),sQuery(id+"F0.wireOp",EDGE,"E2.11.0.3"),sQuery(id+"F0.wireOp",EDGE,"E2.11.0.4"),sQuery(id+"F0.wireOp",EDGE,"E2.11.0.5"),sQuery(id+"F0.wireOp",EDGE,"E2.11.0.6"),sQuery(id+"F0.wireOp",EDGE,"E2.11.0.7"),sQuery(id+"F0.wireOp",EDGE,"E2.11.0.8"),sQuery(id+"F0.wireOp",EDGE,"E2.11.0.9"),sQuery(id+"F0.wireOp",EDGE,"E2.11.0.10"),sQuery(id+"F0.wireOp",EDGE,"E2.12.0.1"),sQuery(id+"F0.wireOp",EDGE,"E2.12.0.2"),sQuery(id+"F0.wireOp",EDGE,"E2.12.0.3"),sQuery(id+"F0.wireOp",EDGE,"E2.12.0.4"),sQuery(id+"F0.wireOp",EDGE,"E2.12.0.5"),sQuery(id+"F0.wireOp",EDGE,"E2.12.0.6"),sQuery(id+"F0.wireOp",EDGE,"E2.12.0.7"),sQuery(id+"F0.wireOp",EDGE,"E2.12.0.8"),sQuery(id+"F0.wireOp",EDGE,"E2.12.0.9"),sQuery(id+"F0.wireOp",EDGE,"E2.12.0.10"),sQuery(id+"F0.wireOp",EDGE,"E2.13.0.1"),sQuery(id+"F0.wireOp",EDGE,"E2.13.0.2"),sQuery(id+"F0.wireOp",EDGE,"E2.13.0.3"),sQuery(id+"F0.wireOp",EDGE,"E2.13.0.4"),sQuery(id+"F0.wireOp",EDGE,"E2.13.0.5"),sQuery(id+"F0.wireOp",EDGE,"E2.13.0.6"),sQuery(id+"F0.wireOp",EDGE,"E2.13.0.7"),sQuery(id+"F0.wireOp",EDGE,"E2.13.0.8"),sQuery(id+"F0.wireOp",EDGE,"E2.13.0.9"),sQuery(id+"F0.wireOp",EDGE,"E2.13.0.10"),sQuery(id+"F0.wireOp",EDGE,"E2.14.0.1"),sQuery(id+"F0.wireOp",EDGE,"E2.14.0.2"),sQuery(id+"F0.wireOp",EDGE,"E2.14.0.3"),sQuery(id+"F0.wireOp",EDGE,"E2.14.0.4"),sQuery(id+"F0.wireOp",EDGE,"E2.14.0.5"),sQuery(id+"F0.wireOp",EDGE,"E2.14.0.6"),sQuery(id+"F0.wireOp",EDGE,"E2.14.0.7"),sQuery(id+"F0.wireOp",EDGE,"E2.14.0.8"),sQuery(id+"F0.wireOp",EDGE,"E2.14.0.9"),sQuery(id+"F0.wireOp",EDGE,"E2.14.0.10"),sQuery(id+"F0.wireOp",EDGE,"E2.15.0.1"),sQuery(id+"F0.wireOp",EDGE,"E2.15.0.2"),sQuery(id+"F0.wireOp",EDGE,"E2.15.0.3"),sQuery(id+"F0.wireOp",EDGE,"E2.15.0.4"),sQuery(id+"F0.wireOp",EDGE,"E2.15.0.5"),sQuery(id+"F0.wireOp",EDGE,"E2.15.0.6"),sQuery(id+"F0.wireOp",EDGE,"E2.15.0.7"),sQuery(id+"F0.wireOp",EDGE,"E2.15.0.8"),sQuery(id+"F0.wireOp",EDGE,"E2.15.0.9"),sQuery(id+"F0.wireOp",EDGE,"E2.15.0.10"),sQuery(id+"F0.wireOp",EDGE,"E2.16.0.1"),sQuery(id+"F0.wireOp",EDGE,"E2.16.0.2"),sQuery(id+"F0.wireOp",EDGE,"E2.16.0.3"),sQuery(id+"F0.wireOp",EDGE,"E2.16.0.4"),sQuery(id+"F0.wireOp",EDGE,"E2.16.0.5"),sQuery(id+"F0.wireOp",EDGE,"E2.16.0.6"),sQuery(id+"F0.wireOp",EDGE,"E2.16.0.7"),sQuery(id+"F0.wireOp",EDGE,"E2.16.0.8"),sQuery(id+"F0.wireOp",EDGE,"E2.16.0.9"),sQuery(id+"F0.wireOp",EDGE,"E2.16.0.10"),sQuery(id+"F0.wireOp",EDGE,"E2.17.0.1"),sQuery(id+"F0.wireOp",EDGE,"E2.17.0.2"),sQuery(id+"F0.wireOp",EDGE,"E2.17.0.3"),sQuery(id+"F0.wireOp",EDGE,"E2.17.0.4"),sQuery(id+"F0.wireOp",EDGE,"E2.17.0.5"),sQuery(id+"F0.wireOp",EDGE,"E2.17.0.6"),sQuery(id+"F0.wireOp",EDGE,"E2.17.0.7"),sQuery(id+"F0.wireOp",EDGE,"E2.17.0.8"),sQuery(id+"F0.wireOp",EDGE,"E2.17.0.9"),sQuery(id+"F0.wireOp",EDGE,"E2.17.0.10"),sQuery(id+"F0.wireOp",EDGE,"E2.18.0.1"),sQuery(id+"F0.wireOp",EDGE,"E2.18.0.2"),sQuery(id+"F0.wireOp",EDGE,"E2.18.0.3"),sQuery(id+"F0.wireOp",EDGE,"E2.18.0.4"),sQuery(id+"F0.wireOp",EDGE,"E2.18.0.5"),sQuery(id+"F0.wireOp",EDGE,"E2.18.0.6"),sQuery(id+"F0.wireOp",EDGE,"E2.18.0.7"),sQuery(id+"F0.wireOp",EDGE,"E2.18.0.8"),sQuery(id+"F0.wireOp",EDGE,"E2.18.0.9"),sQuery(id+"F0.wireOp",EDGE,"E2.18.0.10"),sQuery(id+"F0.wireOp",EDGE,"E2.19.0.1"),sQuery(id+"F0.wireOp",EDGE,"E2.19.0.2"),sQuery(id+"F0.wireOp",EDGE,"E2.19.0.3"),sQuery(id+"F0.wireOp",EDGE,"E2.19.0.4"),sQuery(id+"F0.wireOp",EDGE,"E2.19.0.5"),sQuery(id+"F0.wireOp",EDGE,"E2.19.0.6"),sQuery(id+"F0.wireOp",EDGE,"E2.19.0.7"),sQuery(id+"F0.wireOp",EDGE,"E2.19.0.8"),sQuery(id+"F0.wireOp",EDGE,"E2.19.0.9"),sQuery(id+"F0.wireOp",EDGE,"E2.19.0.10"),sQuery(id+"F0.wireOp",EDGE,"E2.20.0.1"),sQuery(id+"F0.wireOp",EDGE,"E2.20.0.2"),sQuery(id+"F0.wireOp",EDGE,"E2.20.0.3"),sQuery(id+"F0.wireOp",EDGE,"E2.20.0.4"),sQuery(id+"F0.wireOp",EDGE,"E2.20.0.5"),sQuery(id+"F0.wireOp",EDGE,"E2.20.0.6"),sQuery(id+"F0.wireOp",EDGE,"E2.20.0.7"),sQuery(id+"F0.wireOp",EDGE,"E2.20.0.8"),sQuery(id+"F0.wireOp",EDGE,"E2.20.0.9"),sQuery(id+"F0.wireOp",EDGE,"E2.20.0.10"),sQuery(id+"F0.wireOp",EDGE,"E2.21.0.1"),sQuery(id+"F0.wireOp",EDGE,"E2.21.0.2"),sQuery(id+"F0.wireOp",EDGE,"E2.21.0.3"),sQuery(id+"F0.wireOp",EDGE,"E2.21.0.4"),sQuery(id+"F0.wireOp",EDGE,"E2.21.0.5"),sQuery(id+"F0.wireOp",EDGE,"E2.21.0.6"),sQuery(id+"F0.wireOp",EDGE,"E2.21.0.7"),sQuery(id+"F0.wireOp",EDGE,"E2.21.0.8"),sQuery(id+"F0.wireOp",EDGE,"E2.21.0.9"),sQuery(id+"F0.wireOp",EDGE,"E2.21.0.10"),sQuery(id+"F0.wireOp",EDGE,"E2.22.0.1"),sQuery(id+"F0.wireOp",EDGE,"E2.22.0.2"),sQuery(id+"F0.wireOp",EDGE,"E2.22.0.3"),sQuery(id+"F0.wireOp",EDGE,"E2.22.0.4"),sQuery(id+"F0.wireOp",EDGE,"E2.22.0.5"),sQuery(id+"F0.wireOp",EDGE,"E2.22.0.6"),sQuery(id+"F0.wireOp",EDGE,"E2.22.0.7"),sQuery(id+"F0.wireOp",EDGE,"E2.22.0.8"),sQuery(id+"F0.wireOp",EDGE,"E2.22.0.9"),sQuery(id+"F0.wireOp",EDGE,"E2.22.0.10"),sQuery(id+"F0.wireOp",EDGE,"E2.23.0.1"),sQuery(id+"F0.wireOp",EDGE,"E2.23.0.2"),sQuery(id+"F0.wireOp",EDGE,"E2.23.0.3"),sQuery(id+"F0.wireOp",EDGE,"E2.23.0.4"),sQuery(id+"F0.wireOp",EDGE,"E2.23.0.5"),sQuery(id+"F0.wireOp",EDGE,"E2.23.0.6"),sQuery(id+"F0.wireOp",EDGE,"E2.23.0.7"),sQuery(id+"F0.wireOp",EDGE,"E2.23.0.8"),sQuery(id+"F0.wireOp",EDGE,"E2.23.0.9"),sQuery(id+"F0.wireOp",EDGE,"E2.23.0.10"),sQuery(id+"F0.wireOp",EDGE,"E2.24.0.1"),sQuery(id+"F0.wireOp",EDGE,"E2.24.0.2"),sQuery(id+"F0.wireOp",EDGE,"E2.24.0.3"),sQuery(id+"F0.wireOp",EDGE,"E2.24.0.4"),sQuery(id+"F0.wireOp",EDGE,"E2.24.0.5"),sQuery(id+"F0.wireOp",EDGE,"E2.24.0.6"),sQuery(id+"F0.wireOp",EDGE,"E2.24.0.7"),sQuery(id+"F0.wireOp",EDGE,"E2.24.0.8"),sQuery(id+"F0.wireOp",EDGE,"E2.24.0.9"),sQuery(id+"F0.wireOp",EDGE,"E2.24.0.10"),sQuery(id+"F0.wireOp",EDGE,"E2.25.0.1"),sQuery(id+"F0.wireOp",EDGE,"E2.25.0.2"),sQuery(id+"F0.wireOp",EDGE,"E2.25.0.3"),sQuery(id+"F0.wireOp",EDGE,"E2.25.0.4"),sQuery(id+"F0.wireOp",EDGE,"E2.25.0.5"),sQuery(id+"F0.wireOp",EDGE,"E2.25.0.6"),sQuery(id+"F0.wireOp",EDGE,"E2.25.0.7"),sQuery(id+"F0.wireOp",EDGE,"E2.25.0.8"),sQuery(id+"F0.wireOp",EDGE,"E2.25.0.9"),sQuery(id+"F0.wireOp",EDGE,"E2.25.0.10"),sQuery(id+"F0.wireOp",EDGE,"E2.26.0.1"),sQuery(id+"F0.wireOp",EDGE,"E2.26.0.2"),sQuery(id+"F0.wireOp",EDGE,"E2.26.0.3"),sQuery(id+"F0.wireOp",EDGE,"E2.26.0.4"),sQuery(id+"F0.wireOp",EDGE,"E2.26.0.5"),sQuery(id+"F0.wireOp",EDGE,"E2.26.0.6"),sQuery(id+"F0.wireOp",EDGE,"E2.26.0.7"),sQuery(id+"F0.wireOp",EDGE,"E2.26.0.8"),sQuery(id+"F0.wireOp",EDGE,"E2.26.0.9"),sQuery(id+"F0.wireOp",EDGE,"E2.26.0.10"),sQuery(id+"F0.wireOp",EDGE,"E2.27.0.1"),sQuery(id+"F0.wireOp",EDGE,"E2.27.0.2"),sQuery(id+"F0.wireOp",EDGE,"E2.27.0.3"),sQuery(id+"F0.wireOp",EDGE,"E2.27.0.4"),sQuery(id+"F0.wireOp",EDGE,"E2.27.0.5"),sQuery(id+"F0.wireOp",EDGE,"E2.27.0.6"),sQuery(id+"F0.wireOp",EDGE,"E2.27.0.7"),sQuery(id+"F0.wireOp",EDGE,"E2.27.0.8"),sQuery(id+"F0.wireOp",EDGE,"E2.27.0.9"),sQuery(id+"F0.wireOp",EDGE,"E2.27.0.10"),sQuery(id+"F0.wireOp",EDGE,"E2.28.0.1"),sQuery(id+"F0.wireOp",EDGE,"E2.28.0.2"),sQuery(id+"F0.wireOp",EDGE,"E2.28.0.3"),sQuery(id+"F0.wireOp",EDGE,"E2.28.0.4"),sQuery(id+"F0.wireOp",EDGE,"E2.28.0.5"),sQuery(id+"F0.wireOp",EDGE,"E2.28.0.6"),sQuery(id+"F0.wireOp",EDGE,"E2.28.0.7"),sQuery(id+"F0.wireOp",EDGE,"E2.28.0.8"),sQuery(id+"F0.wireOp",EDGE,"E2.28.0.9"),sQuery(id+"F0.wireOp",EDGE,"E2.28.0.10"),sQuery(id+"F0.wireOp",EDGE,"E2.29.0.1"),sQuery(id+"F0.wireOp",EDGE,"E2.29.0.2"),sQuery(id+"F0.wireOp",EDGE,"E2.29.0.3"),sQuery(id+"F0.wireOp",EDGE,"E2.29.0.4"),sQuery(id+"F0.wireOp",EDGE,"E2.29.0.5"),sQuery(id+"F0.wireOp",EDGE,"E2.29.0.6"),sQuery(id+"F0.wireOp",EDGE,"E2.29.0.7"),sQuery(id+"F0.wireOp",EDGE,"E2.29.0.8"),sQuery(id+"F0.wireOp",EDGE,"E2.29.0.9"),sQuery(id+"F0.wireOp",EDGE,"E2.29.0.10"),sQuery(id+"F0.wireOp",EDGE,"E3"),sQuery(id+"F0.wireOp",EDGE,"JgwjaH20-m7XH-zVhQ-8Puc-2S3nrI6lC1iW"),sQuery(id+"F0.wireOp",EDGE,"JdY1tTwT-KZEY-idyO-tq4H-qNwGPPCa9yZ1"),sQuery(id+"F0.wireOp",EDGE,"E4"),sQuery(id+"F0.wireOp",EDGE,"E5"),sQuery(id+"F0.wireOp",EDGE,"E7"),sQuery(id+"F0.wireOp",EDGE,"E8"),sQuery(id+"F0.wireOp",EDGE,"E9.5.30.0"),sQuery(id+"F0.wireOp",EDGE,"E9.7.30.0"),sQuery(id+"F0.wireOp",EDGE,"E9.9.30.0"),sQuery(id+"F0.wireOp",EDGE,"E9.11.30.0"),sQuery(id+"F0.wireOp",EDGE,"E9.13.30.0"),sQuery(id+"F0.wireOp",EDGE,"E9.15.30.0"),sQuery(id+"F0.wireOp",EDGE,"E9.17.30.0"),sQuery(id+"F0.wireOp",EDGE,"E9.19.30.0"),sQuery(id+"F0.wireOp",EDGE,"E9.21.30.0"),sQuery(id+"F0.wireOp",EDGE,"E9.3.31.0"),sQuery(id+"F0.wireOp",EDGE,"E9.5.31.0"),sQuery(id+"F0.wireOp",EDGE,"E9.7.31.0"),sQuery(id+"F0.wireOp",EDGE,"E9.9.31.0"),sQuery(id+"F0.wireOp",EDGE,"E9.11.31.0"),sQuery(id+"F0.wireOp",EDGE,"E9.13.31.0"),sQuery(id+"F0.wireOp",EDGE,"E9.15.31.0"),sQuery(id+"F0.wireOp",EDGE,"E9.17.31.0"),sQuery(id+"F0.wireOp",EDGE,"E9.19.31.0"),sQuery(id+"F0.wireOp",EDGE,"E9.21.31.0"),sQuery(id+"F0.wireOp",EDGE,"E9.3.32.0"),sQuery(id+"F0.wireOp",EDGE,"E9.5.32.0"),sQuery(id+"F0.wireOp",EDGE,"E9.7.32.0"),sQuery(id+"F0.wireOp",EDGE,"E9.9.32.0"),sQuery(id+"F0.wireOp",EDGE,"E9.11.32.0"),sQuery(id+"F0.wireOp",EDGE,"E9.13.32.0"),sQuery(id+"F0.wireOp",EDGE,"E9.15.32.0"),sQuery(id+"F0.wireOp",EDGE,"E9.17.32.0"),sQuery(id+"F0.wireOp",EDGE,"E9.19.32.0"),sQuery(id+"F0.wireOp",EDGE,"E9.21.32.0"),sQuery(id+"F0.wireOp",EDGE,"E9.3.33.0"),sQuery(id+"F0.wireOp",EDGE,"E9.5.33.0"),sQuery(id+"F0.wireOp",EDGE,"E9.7.33.0"),sQuery(id+"F0.wireOp",EDGE,"E9.9.33.0"),sQuery(id+"F0.wireOp",EDGE,"E9.11.33.0"),sQuery(id+"F0.wireOp",EDGE,"E9.13.33.0"),sQuery(id+"F0.wireOp",EDGE,"E9.15.33.0"),sQuery(id+"F0.wireOp",EDGE,"E9.17.33.0"),sQuery(id+"F0.wireOp",EDGE,"E9.19.33.0"),sQuery(id+"F0.wireOp",EDGE,"E9.21.33.0"),sQuery(id+"F0.wireOp",EDGE,"E9.3.34.0"),sQuery(id+"F0.wireOp",EDGE,"E9.5.34.0"),sQuery(id+"F0.wireOp",EDGE,"E9.7.34.0"),sQuery(id+"F0.wireOp",EDGE,"E9.9.34.0"),sQuery(id+"F0.wireOp",EDGE,"E9.11.34.0"),sQuery(id+"F0.wireOp",EDGE,"E9.13.34.0"),sQuery(id+"F0.wireOp",EDGE,"E9.15.34.0"),sQuery(id+"F0.wireOp",EDGE,"E9.17.34.0"),sQuery(id+"F0.wireOp",EDGE,"E9.19.34.0"),sQuery(id+"F0.wireOp",EDGE,"E9.21.34.0"),sQuery(id+"F0.wireOp",EDGE,"E9.3.35.0"),sQuery(id+"F0.wireOp",EDGE,"E9.5.35.0"),sQuery(id+"F0.wireOp",EDGE,"E9.7.35.0"),sQuery(id+"F0.wireOp",EDGE,"E9.9.35.0"),sQuery(id+"F0.wireOp",EDGE,"E9.11.35.0"),sQuery(id+"F0.wireOp",EDGE,"E9.13.35.0"),sQuery(id+"F0.wireOp",EDGE,"E9.15.35.0"),sQuery(id+"F0.wireOp",EDGE,"E9.17.35.0"),sQuery(id+"F0.wireOp",EDGE,"E9.19.35.0"),sQuery(id+"F0.wireOp",EDGE,"E9.21.35.0"),sQuery(id+"F0.wireOp",EDGE,"E9.3.36.0"),sQuery(id+"F0.wireOp",EDGE,"E9.5.36.0"),sQuery(id+"F0.wireOp",EDGE,"E9.7.36.0"),sQuery(id+"F0.wireOp",EDGE,"E9.9.36.0"),sQuery(id+"F0.wireOp",EDGE,"E9.11.36.0"),sQuery(id+"F0.wireOp",EDGE,"E9.13.36.0"),sQuery(id+"F0.wireOp",EDGE,"E9.15.36.0"),sQuery(id+"F0.wireOp",EDGE,"E9.17.36.0"),sQuery(id+"F0.wireOp",EDGE,"E9.19.36.0"),sQuery(id+"F0.wireOp",EDGE,"E9.21.36.0"),sQuery(id+"F0.wireOp",EDGE,"E9.3.37.0"),sQuery(id+"F0.wireOp",EDGE,"E9.5.37.0"),sQuery(id+"F0.wireOp",EDGE,"E9.7.37.0"),sQuery(id+"F0.wireOp",EDGE,"E9.9.37.0"),sQuery(id+"F0.wireOp",EDGE,"E9.11.37.0"),sQuery(id+"F0.wireOp",EDGE,"E9.13.37.0"),sQuery(id+"F0.wireOp",EDGE,"E9.15.37.0"),sQuery(id+"F0.wireOp",EDGE,"E9.17.37.0"),sQuery(id+"F0.wireOp",EDGE,"E9.19.37.0"),sQuery(id+"F0.wireOp",EDGE,"E9.21.37.0"),sQuery(id+"F0.wireOp",EDGE,"E9.3.38.0"),sQuery(id+"F0.wireOp",EDGE,"E9.5.38.0"),sQuery(id+"F0.wireOp",EDGE,"E9.7.38.0"),sQuery(id+"F0.wireOp",EDGE,"E9.9.38.0"),sQuery(id+"F0.wireOp",EDGE,"E9.11.38.0"),sQuery(id+"F0.wireOp",EDGE,"E9.13.38.0"),sQuery(id+"F0.wireOp",EDGE,"E9.15.38.0"),sQuery(id+"F0.wireOp",EDGE,"E9.17.38.0"),sQuery(id+"F0.wireOp",EDGE,"E9.19.38.0"),sQuery(id+"F0.wireOp",EDGE,"E9.21.38.0"),sQuery(id+"F0.wireOp",EDGE,"E9.3.39.0"),sQuery(id+"F0.wireOp",EDGE,"E9.5.39.0"),sQuery(id+"F0.wireOp",EDGE,"E9.7.39.0"),sQuery(id+"F0.wireOp",EDGE,"E9.9.39.0"),sQuery(id+"F0.wireOp",EDGE,"E9.11.39.0"),sQuery(id+"F0.wireOp",EDGE,"E9.13.39.0"),sQuery(id+"F0.wireOp",EDGE,"E9.15.39.0"),sQuery(id+"F0.wireOp",EDGE,"E9.17.39.0"),sQuery(id+"F0.wireOp",EDGE,"E9.19.39.0"),sQuery(id+"F0.wireOp",EDGE,"E9.21.39.0"),sQuery(id+"F0.wireOp",EDGE,"E9.3.40.0"),sQuery(id+"F0.wireOp",EDGE,"E9.5.40.0"),sQuery(id+"F0.wireOp",EDGE,"E9.7.40.0"),sQuery(id+"F0.wireOp",EDGE,"E9.9.40.0"),sQuery(id+"F0.wireOp",EDGE,"E9.11.40.0"),sQuery(id+"F0.wireOp",EDGE,"E9.13.40.0"),sQuery(id+"F0.wireOp",EDGE,"E9.15.40.0"),sQuery(id+"F0.wireOp",EDGE,"E9.17.40.0"),sQuery(id+"F0.wireOp",EDGE,"E9.19.40.0"),sQuery(id+"F0.wireOp",EDGE,"E9.21.40.0"),sQuery(id+"F0.wireOp",EDGE,"E9.3.41.0"),sQuery(id+"F0.wireOp",EDGE,"E9.5.41.0"),sQuery(id+"F0.wireOp",EDGE,"E9.7.41.0"),sQuery(id+"F0.wireOp",EDGE,"E9.9.41.0"),sQuery(id+"F0.wireOp",EDGE,"E9.11.41.0"),sQuery(id+"F0.wireOp",EDGE,"E9.13.41.0"),sQuery(id+"F0.wireOp",EDGE,"E9.15.41.0"),sQuery(id+"F0.wireOp",EDGE,"E9.17.41.0"),sQuery(id+"F0.wireOp",EDGE,"E9.19.41.0"),sQuery(id+"F0.wireOp",EDGE,"E9.21.41.0"),sQuery(id+"F0.wireOp",EDGE,"E9.3.42.0"),sQuery(id+"F0.wireOp",EDGE,"E9.5.42.0"),sQuery(id+"F0.wireOp",EDGE,"E9.7.42.0"),sQuery(id+"F0.wireOp",EDGE,"E9.9.42.0"),sQuery(id+"F0.wireOp",EDGE,"E9.11.42.0"),sQuery(id+"F0.wireOp",EDGE,"E9.13.42.0"),sQuery(id+"F0.wireOp",EDGE,"E9.15.42.0"),sQuery(id+"F0.wireOp",EDGE,"E9.17.42.0"),sQuery(id+"F0.wireOp",EDGE,"E9.19.42.0"),sQuery(id+"F0.wireOp",EDGE,"E9.21.42.0"),sQuery(id+"F0.wireOp",EDGE,"E9.3.43.0"),sQuery(id+"F0.wireOp",EDGE,"E9.5.43.0"),sQuery(id+"F0.wireOp",EDGE,"E9.7.43.0"),sQuery(id+"F0.wireOp",EDGE,"E9.9.43.0"),sQuery(id+"F0.wireOp",EDGE,"E9.11.43.0"),sQuery(id+"F0.wireOp",EDGE,"E9.13.43.0"),sQuery(id+"F0.wireOp",EDGE,"E9.15.43.0"),sQuery(id+"F0.wireOp",EDGE,"E9.17.43.0"),sQuery(id+"F0.wireOp",EDGE,"E9.19.43.0"),sQuery(id+"F0.wireOp",EDGE,"E9.21.43.0"),sQuery(id+"F0.wireOp",EDGE,"E9.3.44.0"),sQuery(id+"F0.wireOp",EDGE,"E9.5.44.0"),sQuery(id+"F0.wireOp",EDGE,"E9.7.44.0"),sQuery(id+"F0.wireOp",EDGE,"E9.9.44.0"),sQuery(id+"F0.wireOp",EDGE,"E9.11.44.0"),sQuery(id+"F0.wireOp",EDGE,"E9.13.44.0"),sQuery(id+"F0.wireOp",EDGE,"E9.15.44.0"),sQuery(id+"F0.wireOp",EDGE,"E9.17.44.0"),sQuery(id+"F0.wireOp",EDGE,"E9.19.44.0"),sQuery(id+"F0.wireOp",EDGE,"E9.21.44.0"),sQuery(id+"F0.wireOp",EDGE,"E9.3.45.0"),sQuery(id+"F0.wireOp",EDGE,"E9.5.45.0"),sQuery(id+"F0.wireOp",EDGE,"E9.7.45.0"),sQuery(id+"F0.wireOp",EDGE,"E9.9.45.0"),sQuery(id+"F0.wireOp",EDGE,"E9.11.45.0"),sQuery(id+"F0.wireOp",EDGE,"E9.13.45.0"),sQuery(id+"F0.wireOp",EDGE,"E9.15.45.0"),sQuery(id+"F0.wireOp",EDGE,"E9.17.45.0"),sQuery(id+"F0.wireOp",EDGE,"E9.19.45.0"),sQuery(id+"F0.wireOp",EDGE,"E9.21.45.0"),sQuery(id+"F0.wireOp",EDGE,"E9.3.46.0"),sQuery(id+"F0.wireOp",EDGE,"E9.5.46.0"),sQuery(id+"F0.wireOp",EDGE,"E9.7.46.0"),sQuery(id+"F0.wireOp",EDGE,"E9.9.46.0"),sQuery(id+"F0.wireOp",EDGE,"E9.11.46.0"),sQuery(id+"F0.wireOp",EDGE,"E9.13.46.0"),sQuery(id+"F0.wireOp",EDGE,"E9.15.46.0"),sQuery(id+"F0.wireOp",EDGE,"E9.17.46.0"),sQuery(id+"F0.wireOp",EDGE,"E9.19.46.0"),sQuery(id+"F0.wireOp",EDGE,"E9.21.46.0"),sQuery(id+"F0.wireOp",EDGE,"E21.5.30.0"),sQuery(id+"F0.wireOp",EDGE,"E23"),sQuery(id+"F0.wireOp",EDGE,"E24"),sQuery(id+"F0.wireOp",EDGE,"E25")])]});
            transform(context, id + "F3", {"entities" : qUnion([Q0]), "transformType" : TransformType.TRANSLATION_3D, "dx" : 22.87 * mm, "dy" : 0 * mm, "dz" : 0 * mm, "makeCopy" : true});
        }
        {
            var Q0;
            Q0=makeQuery(id+"F1.opExtrude","SWEPT_BODY",BODY,{"disambiguationData":[OSD([sQuery(id+"F0.wireOp",EDGE,"E0"),sQuery(id+"F0.wireOp",EDGE,"E1.1.0.0"),sQuery(id+"F0.wireOp",EDGE,"E1.2.0.0"),sQuery(id+"F0.wireOp",EDGE,"E1.3.0.0"),sQuery(id+"F0.wireOp",EDGE,"E1.4.0.0"),sQuery(id+"F0.wireOp",EDGE,"E1.5.0.0"),sQuery(id+"F0.wireOp",EDGE,"E1.6.0.0"),sQuery(id+"F0.wireOp",EDGE,"E1.7.0.0"),sQuery(id+"F0.wireOp",EDGE,"E1.8.0.0"),sQuery(id+"F0.wireOp",EDGE,"E1.9.0.0"),sQuery(id+"F0.wireOp",EDGE,"E2.1.0.1"),sQuery(id+"F0.wireOp",EDGE,"E2.1.0.2"),sQuery(id+"F0.wireOp",EDGE,"E2.1.0.3"),sQuery(id+"F0.wireOp",EDGE,"E2.1.0.4"),sQuery(id+"F0.wireOp",EDGE,"E2.1.0.5"),sQuery(id+"F0.wireOp",EDGE,"E2.1.0.6"),sQuery(id+"F0.wireOp",EDGE,"E2.1.0.7"),sQuery(id+"F0.wireOp",EDGE,"E2.1.0.8"),sQuery(id+"F0.wireOp",EDGE,"E2.1.0.9"),sQuery(id+"F0.wireOp",EDGE,"E2.1.0.10"),sQuery(id+"F0.wireOp",EDGE,"E2.2.0.1"),sQuery(id+"F0.wireOp",EDGE,"E2.2.0.2"),sQuery(id+"F0.wireOp",EDGE,"E2.2.0.3"),sQuery(id+"F0.wireOp",EDGE,"E2.2.0.4"),sQuery(id+"F0.wireOp",EDGE,"E2.2.0.5"),sQuery(id+"F0.wireOp",EDGE,"E2.2.0.6"),sQuery(id+"F0.wireOp",EDGE,"E2.2.0.7"),sQuery(id+"F0.wireOp",EDGE,"E2.2.0.8"),sQuery(id+"F0.wireOp",EDGE,"E2.2.0.9"),sQuery(id+"F0.wireOp",EDGE,"E2.2.0.10"),sQuery(id+"F0.wireOp",EDGE,"E2.3.0.1"),sQuery(id+"F0.wireOp",EDGE,"E2.3.0.2"),sQuery(id+"F0.wireOp",EDGE,"E2.3.0.3"),sQuery(id+"F0.wireOp",EDGE,"E2.3.0.4"),sQuery(id+"F0.wireOp",EDGE,"E2.3.0.5"),sQuery(id+"F0.wireOp",EDGE,"E2.3.0.6"),sQuery(id+"F0.wireOp",EDGE,"E2.3.0.7"),sQuery(id+"F0.wireOp",EDGE,"E2.3.0.8"),sQuery(id+"F0.wireOp",EDGE,"E2.3.0.9"),sQuery(id+"F0.wireOp",EDGE,"E2.3.0.10"),sQuery(id+"F0.wireOp",EDGE,"E2.4.0.1"),sQuery(id+"F0.wireOp",EDGE,"E2.4.0.2"),sQuery(id+"F0.wireOp",EDGE,"E2.4.0.3"),sQuery(id+"F0.wireOp",EDGE,"E2.4.0.4"),sQuery(id+"F0.wireOp",EDGE,"E2.4.0.5"),sQuery(id+"F0.wireOp",EDGE,"E2.4.0.6"),sQuery(id+"F0.wireOp",EDGE,"E2.4.0.7"),sQuery(id+"F0.wireOp",EDGE,"E2.4.0.8"),sQuery(id+"F0.wireOp",EDGE,"E2.4.0.9"),sQuery(id+"F0.wireOp",EDGE,"E2.4.0.10"),sQuery(id+"F0.wireOp",EDGE,"E2.5.0.1"),sQuery(id+"F0.wireOp",EDGE,"E2.5.0.2"),sQuery(id+"F0.wireOp",EDGE,"E2.5.0.3"),sQuery(id+"F0.wireOp",EDGE,"E2.5.0.4"),sQuery(id+"F0.wireOp",EDGE,"E2.5.0.5"),sQuery(id+"F0.wireOp",EDGE,"E2.5.0.6"),sQuery(id+"F0.wireOp",EDGE,"E2.5.0.7"),sQuery(id+"F0.wireOp",EDGE,"E2.5.0.8"),sQuery(id+"F0.wireOp",EDGE,"E2.5.0.9"),sQuery(id+"F0.wireOp",EDGE,"E2.5.0.10"),sQuery(id+"F0.wireOp",EDGE,"E2.6.0.1"),sQuery(id+"F0.wireOp",EDGE,"E2.6.0.2"),sQuery(id+"F0.wireOp",EDGE,"E2.6.0.3"),sQuery(id+"F0.wireOp",EDGE,"E2.6.0.4"),sQuery(id+"F0.wireOp",EDGE,"E2.6.0.5"),sQuery(id+"F0.wireOp",EDGE,"E2.6.0.6"),sQuery(id+"F0.wireOp",EDGE,"E2.6.0.7"),sQuery(id+"F0.wireOp",EDGE,"E2.6.0.8"),sQuery(id+"F0.wireOp",EDGE,"E2.6.0.9"),sQuery(id+"F0.wireOp",EDGE,"E2.6.0.10"),sQuery(id+"F0.wireOp",EDGE,"E2.7.0.1"),sQuery(id+"F0.wireOp",EDGE,"E2.7.0.2"),sQuery(id+"F0.wireOp",EDGE,"E2.7.0.3"),sQuery(id+"F0.wireOp",EDGE,"E2.7.0.4"),sQuery(id+"F0.wireOp",EDGE,"E2.7.0.5"),sQuery(id+"F0.wireOp",EDGE,"E2.7.0.6"),sQuery(id+"F0.wireOp",EDGE,"E2.7.0.7"),sQuery(id+"F0.wireOp",EDGE,"E2.7.0.8"),sQuery(id+"F0.wireOp",EDGE,"E2.7.0.9"),sQuery(id+"F0.wireOp",EDGE,"E2.7.0.10"),sQuery(id+"F0.wireOp",EDGE,"E2.8.0.1"),sQuery(id+"F0.wireOp",EDGE,"E2.8.0.2"),sQuery(id+"F0.wireOp",EDGE,"E2.8.0.3"),sQuery(id+"F0.wireOp",EDGE,"E2.8.0.4"),sQuery(id+"F0.wireOp",EDGE,"E2.8.0.5"),sQuery(id+"F0.wireOp",EDGE,"E2.8.0.6"),sQuery(id+"F0.wireOp",EDGE,"E2.8.0.7"),sQuery(id+"F0.wireOp",EDGE,"E2.8.0.8"),sQuery(id+"F0.wireOp",EDGE,"E2.8.0.9"),sQuery(id+"F0.wireOp",EDGE,"E2.8.0.10"),sQuery(id+"F0.wireOp",EDGE,"E2.9.0.1"),sQuery(id+"F0.wireOp",EDGE,"E2.9.0.2"),sQuery(id+"F0.wireOp",EDGE,"E2.9.0.3"),sQuery(id+"F0.wireOp",EDGE,"E2.9.0.4"),sQuery(id+"F0.wireOp",EDGE,"E2.9.0.5"),sQuery(id+"F0.wireOp",EDGE,"E2.9.0.6"),sQuery(id+"F0.wireOp",EDGE,"E2.9.0.7"),sQuery(id+"F0.wireOp",EDGE,"E2.9.0.8"),sQuery(id+"F0.wireOp",EDGE,"E2.9.0.9"),sQuery(id+"F0.wireOp",EDGE,"E2.9.0.10"),sQuery(id+"F0.wireOp",EDGE,"E2.10.0.1"),sQuery(id+"F0.wireOp",EDGE,"E2.10.0.2"),sQuery(id+"F0.wireOp",EDGE,"E2.10.0.3"),sQuery(id+"F0.wireOp",EDGE,"E2.10.0.4"),sQuery(id+"F0.wireOp",EDGE,"E2.10.0.5"),sQuery(id+"F0.wireOp",EDGE,"E2.10.0.6"),sQuery(id+"F0.wireOp",EDGE,"E2.10.0.7"),sQuery(id+"F0.wireOp",EDGE,"E2.10.0.8"),sQuery(id+"F0.wireOp",EDGE,"E2.10.0.9"),sQuery(id+"F0.wireOp",EDGE,"E2.10.0.10"),sQuery(id+"F0.wireOp",EDGE,"E2.11.0.1"),sQuery(id+"F0.wireOp",EDGE,"E2.11.0.2"),sQuery(id+"F0.wireOp",EDGE,"E2.11.0.3"),sQuery(id+"F0.wireOp",EDGE,"E2.11.0.4"),sQuery(id+"F0.wireOp",EDGE,"E2.11.0.5"),sQuery(id+"F0.wireOp",EDGE,"E2.11.0.6"),sQuery(id+"F0.wireOp",EDGE,"E2.11.0.7"),sQuery(id+"F0.wireOp",EDGE,"E2.11.0.8"),sQuery(id+"F0.wireOp",EDGE,"E2.11.0.9"),sQuery(id+"F0.wireOp",EDGE,"E2.11.0.10"),sQuery(id+"F0.wireOp",EDGE,"E2.12.0.1"),sQuery(id+"F0.wireOp",EDGE,"E2.12.0.2"),sQuery(id+"F0.wireOp",EDGE,"E2.12.0.3"),sQuery(id+"F0.wireOp",EDGE,"E2.12.0.4"),sQuery(id+"F0.wireOp",EDGE,"E2.12.0.5"),sQuery(id+"F0.wireOp",EDGE,"E2.12.0.6"),sQuery(id+"F0.wireOp",EDGE,"E2.12.0.7"),sQuery(id+"F0.wireOp",EDGE,"E2.12.0.8"),sQuery(id+"F0.wireOp",EDGE,"E2.12.0.9"),sQuery(id+"F0.wireOp",EDGE,"E2.12.0.10"),sQuery(id+"F0.wireOp",EDGE,"E2.13.0.1"),sQuery(id+"F0.wireOp",EDGE,"E2.13.0.2"),sQuery(id+"F0.wireOp",EDGE,"E2.13.0.3"),sQuery(id+"F0.wireOp",EDGE,"E2.13.0.4"),sQuery(id+"F0.wireOp",EDGE,"E2.13.0.5"),sQuery(id+"F0.wireOp",EDGE,"E2.13.0.6"),sQuery(id+"F0.wireOp",EDGE,"E2.13.0.7"),sQuery(id+"F0.wireOp",EDGE,"E2.13.0.8"),sQuery(id+"F0.wireOp",EDGE,"E2.13.0.9"),sQuery(id+"F0.wireOp",EDGE,"E2.13.0.10"),sQuery(id+"F0.wireOp",EDGE,"E2.14.0.1"),sQuery(id+"F0.wireOp",EDGE,"E2.14.0.2"),sQuery(id+"F0.wireOp",EDGE,"E2.14.0.3"),sQuery(id+"F0.wireOp",EDGE,"E2.14.0.4"),sQuery(id+"F0.wireOp",EDGE,"E2.14.0.5"),sQuery(id+"F0.wireOp",EDGE,"E2.14.0.6"),sQuery(id+"F0.wireOp",EDGE,"E2.14.0.7"),sQuery(id+"F0.wireOp",EDGE,"E2.14.0.8"),sQuery(id+"F0.wireOp",EDGE,"E2.14.0.9"),sQuery(id+"F0.wireOp",EDGE,"E2.14.0.10"),sQuery(id+"F0.wireOp",EDGE,"E2.15.0.1"),sQuery(id+"F0.wireOp",EDGE,"E2.15.0.2"),sQuery(id+"F0.wireOp",EDGE,"E2.15.0.3"),sQuery(id+"F0.wireOp",EDGE,"E2.15.0.4"),sQuery(id+"F0.wireOp",EDGE,"E2.15.0.5"),sQuery(id+"F0.wireOp",EDGE,"E2.15.0.6"),sQuery(id+"F0.wireOp",EDGE,"E2.15.0.7"),sQuery(id+"F0.wireOp",EDGE,"E2.15.0.8"),sQuery(id+"F0.wireOp",EDGE,"E2.15.0.9"),sQuery(id+"F0.wireOp",EDGE,"E2.15.0.10"),sQuery(id+"F0.wireOp",EDGE,"E2.16.0.1"),sQuery(id+"F0.wireOp",EDGE,"E2.16.0.2"),sQuery(id+"F0.wireOp",EDGE,"E2.16.0.3"),sQuery(id+"F0.wireOp",EDGE,"E2.16.0.4"),sQuery(id+"F0.wireOp",EDGE,"E2.16.0.5"),sQuery(id+"F0.wireOp",EDGE,"E2.16.0.6"),sQuery(id+"F0.wireOp",EDGE,"E2.16.0.7"),sQuery(id+"F0.wireOp",EDGE,"E2.16.0.8"),sQuery(id+"F0.wireOp",EDGE,"E2.16.0.9"),sQuery(id+"F0.wireOp",EDGE,"E2.16.0.10"),sQuery(id+"F0.wireOp",EDGE,"E2.17.0.1"),sQuery(id+"F0.wireOp",EDGE,"E2.17.0.2"),sQuery(id+"F0.wireOp",EDGE,"E2.17.0.3"),sQuery(id+"F0.wireOp",EDGE,"E2.17.0.4"),sQuery(id+"F0.wireOp",EDGE,"E2.17.0.5"),sQuery(id+"F0.wireOp",EDGE,"E2.17.0.6"),sQuery(id+"F0.wireOp",EDGE,"E2.17.0.7"),sQuery(id+"F0.wireOp",EDGE,"E2.17.0.8"),sQuery(id+"F0.wireOp",EDGE,"E2.17.0.9"),sQuery(id+"F0.wireOp",EDGE,"E2.17.0.10"),sQuery(id+"F0.wireOp",EDGE,"E2.18.0.1"),sQuery(id+"F0.wireOp",EDGE,"E2.18.0.2"),sQuery(id+"F0.wireOp",EDGE,"E2.18.0.3"),sQuery(id+"F0.wireOp",EDGE,"E2.18.0.4"),sQuery(id+"F0.wireOp",EDGE,"E2.18.0.5"),sQuery(id+"F0.wireOp",EDGE,"E2.18.0.6"),sQuery(id+"F0.wireOp",EDGE,"E2.18.0.7"),sQuery(id+"F0.wireOp",EDGE,"E2.18.0.8"),sQuery(id+"F0.wireOp",EDGE,"E2.18.0.9"),sQuery(id+"F0.wireOp",EDGE,"E2.18.0.10"),sQuery(id+"F0.wireOp",EDGE,"E2.19.0.1"),sQuery(id+"F0.wireOp",EDGE,"E2.19.0.2"),sQuery(id+"F0.wireOp",EDGE,"E2.19.0.3"),sQuery(id+"F0.wireOp",EDGE,"E2.19.0.4"),sQuery(id+"F0.wireOp",EDGE,"E2.19.0.5"),sQuery(id+"F0.wireOp",EDGE,"E2.19.0.6"),sQuery(id+"F0.wireOp",EDGE,"E2.19.0.7"),sQuery(id+"F0.wireOp",EDGE,"E2.19.0.8"),sQuery(id+"F0.wireOp",EDGE,"E2.19.0.9"),sQuery(id+"F0.wireOp",EDGE,"E2.19.0.10"),sQuery(id+"F0.wireOp",EDGE,"E2.20.0.1"),sQuery(id+"F0.wireOp",EDGE,"E2.20.0.2"),sQuery(id+"F0.wireOp",EDGE,"E2.20.0.3"),sQuery(id+"F0.wireOp",EDGE,"E2.20.0.4"),sQuery(id+"F0.wireOp",EDGE,"E2.20.0.5"),sQuery(id+"F0.wireOp",EDGE,"E2.20.0.6"),sQuery(id+"F0.wireOp",EDGE,"E2.20.0.7"),sQuery(id+"F0.wireOp",EDGE,"E2.20.0.8"),sQuery(id+"F0.wireOp",EDGE,"E2.20.0.9"),sQuery(id+"F0.wireOp",EDGE,"E2.20.0.10"),sQuery(id+"F0.wireOp",EDGE,"E2.21.0.1"),sQuery(id+"F0.wireOp",EDGE,"E2.21.0.2"),sQuery(id+"F0.wireOp",EDGE,"E2.21.0.3"),sQuery(id+"F0.wireOp",EDGE,"E2.21.0.4"),sQuery(id+"F0.wireOp",EDGE,"E2.21.0.5"),sQuery(id+"F0.wireOp",EDGE,"E2.21.0.6"),sQuery(id+"F0.wireOp",EDGE,"E2.21.0.7"),sQuery(id+"F0.wireOp",EDGE,"E2.21.0.8"),sQuery(id+"F0.wireOp",EDGE,"E2.21.0.9"),sQuery(id+"F0.wireOp",EDGE,"E2.21.0.10"),sQuery(id+"F0.wireOp",EDGE,"E2.22.0.1"),sQuery(id+"F0.wireOp",EDGE,"E2.22.0.2"),sQuery(id+"F0.wireOp",EDGE,"E2.22.0.3"),sQuery(id+"F0.wireOp",EDGE,"E2.22.0.4"),sQuery(id+"F0.wireOp",EDGE,"E2.22.0.5"),sQuery(id+"F0.wireOp",EDGE,"E2.22.0.6"),sQuery(id+"F0.wireOp",EDGE,"E2.22.0.7"),sQuery(id+"F0.wireOp",EDGE,"E2.22.0.8"),sQuery(id+"F0.wireOp",EDGE,"E2.22.0.9"),sQuery(id+"F0.wireOp",EDGE,"E2.22.0.10"),sQuery(id+"F0.wireOp",EDGE,"E2.23.0.1"),sQuery(id+"F0.wireOp",EDGE,"E2.23.0.2"),sQuery(id+"F0.wireOp",EDGE,"E2.23.0.3"),sQuery(id+"F0.wireOp",EDGE,"E2.23.0.4"),sQuery(id+"F0.wireOp",EDGE,"E2.23.0.5"),sQuery(id+"F0.wireOp",EDGE,"E2.23.0.6"),sQuery(id+"F0.wireOp",EDGE,"E2.23.0.7"),sQuery(id+"F0.wireOp",EDGE,"E2.23.0.8"),sQuery(id+"F0.wireOp",EDGE,"E2.23.0.9"),sQuery(id+"F0.wireOp",EDGE,"E2.23.0.10"),sQuery(id+"F0.wireOp",EDGE,"E2.24.0.1"),sQuery(id+"F0.wireOp",EDGE,"E2.24.0.2"),sQuery(id+"F0.wireOp",EDGE,"E2.24.0.3"),sQuery(id+"F0.wireOp",EDGE,"E2.24.0.4"),sQuery(id+"F0.wireOp",EDGE,"E2.24.0.5"),sQuery(id+"F0.wireOp",EDGE,"E2.24.0.6"),sQuery(id+"F0.wireOp",EDGE,"E2.24.0.7"),sQuery(id+"F0.wireOp",EDGE,"E2.24.0.8"),sQuery(id+"F0.wireOp",EDGE,"E2.24.0.9"),sQuery(id+"F0.wireOp",EDGE,"E2.24.0.10"),sQuery(id+"F0.wireOp",EDGE,"E2.25.0.1"),sQuery(id+"F0.wireOp",EDGE,"E2.25.0.2"),sQuery(id+"F0.wireOp",EDGE,"E2.25.0.3"),sQuery(id+"F0.wireOp",EDGE,"E2.25.0.4"),sQuery(id+"F0.wireOp",EDGE,"E2.25.0.5"),sQuery(id+"F0.wireOp",EDGE,"E2.25.0.6"),sQuery(id+"F0.wireOp",EDGE,"E2.25.0.7"),sQuery(id+"F0.wireOp",EDGE,"E2.25.0.8"),sQuery(id+"F0.wireOp",EDGE,"E2.25.0.9"),sQuery(id+"F0.wireOp",EDGE,"E2.25.0.10"),sQuery(id+"F0.wireOp",EDGE,"E2.26.0.1"),sQuery(id+"F0.wireOp",EDGE,"E2.26.0.2"),sQuery(id+"F0.wireOp",EDGE,"E2.26.0.3"),sQuery(id+"F0.wireOp",EDGE,"E2.26.0.4"),sQuery(id+"F0.wireOp",EDGE,"E2.26.0.5"),sQuery(id+"F0.wireOp",EDGE,"E2.26.0.6"),sQuery(id+"F0.wireOp",EDGE,"E2.26.0.7"),sQuery(id+"F0.wireOp",EDGE,"E2.26.0.8"),sQuery(id+"F0.wireOp",EDGE,"E2.26.0.9"),sQuery(id+"F0.wireOp",EDGE,"E2.26.0.10"),sQuery(id+"F0.wireOp",EDGE,"E2.27.0.1"),sQuery(id+"F0.wireOp",EDGE,"E2.27.0.2"),sQuery(id+"F0.wireOp",EDGE,"E2.27.0.3"),sQuery(id+"F0.wireOp",EDGE,"E2.27.0.4"),sQuery(id+"F0.wireOp",EDGE,"E2.27.0.5"),sQuery(id+"F0.wireOp",EDGE,"E2.27.0.6"),sQuery(id+"F0.wireOp",EDGE,"E2.27.0.7"),sQuery(id+"F0.wireOp",EDGE,"E2.27.0.8"),sQuery(id+"F0.wireOp",EDGE,"E2.27.0.9"),sQuery(id+"F0.wireOp",EDGE,"E2.27.0.10"),sQuery(id+"F0.wireOp",EDGE,"E2.28.0.1"),sQuery(id+"F0.wireOp",EDGE,"E2.28.0.2"),sQuery(id+"F0.wireOp",EDGE,"E2.28.0.3"),sQuery(id+"F0.wireOp",EDGE,"E2.28.0.4"),sQuery(id+"F0.wireOp",EDGE,"E2.28.0.5"),sQuery(id+"F0.wireOp",EDGE,"E2.28.0.6"),sQuery(id+"F0.wireOp",EDGE,"E2.28.0.7"),sQuery(id+"F0.wireOp",EDGE,"E2.28.0.8"),sQuery(id+"F0.wireOp",EDGE,"E2.28.0.9"),sQuery(id+"F0.wireOp",EDGE,"E2.28.0.10"),sQuery(id+"F0.wireOp",EDGE,"E2.29.0.1"),sQuery(id+"F0.wireOp",EDGE,"E2.29.0.2"),sQuery(id+"F0.wireOp",EDGE,"E2.29.0.3"),sQuery(id+"F0.wireOp",EDGE,"E2.29.0.4"),sQuery(id+"F0.wireOp",EDGE,"E2.29.0.5"),sQuery(id+"F0.wireOp",EDGE,"E2.29.0.6"),sQuery(id+"F0.wireOp",EDGE,"E2.29.0.7"),sQuery(id+"F0.wireOp",EDGE,"E2.29.0.8"),sQuery(id+"F0.wireOp",EDGE,"E2.29.0.9"),sQuery(id+"F0.wireOp",EDGE,"E2.29.0.10"),sQuery(id+"F0.wireOp",EDGE,"E3"),sQuery(id+"F0.wireOp",EDGE,"JgwjaH20-m7XH-zVhQ-8Puc-2S3nrI6lC1iW"),sQuery(id+"F0.wireOp",EDGE,"JdY1tTwT-KZEY-idyO-tq4H-qNwGPPCa9yZ1"),sQuery(id+"F0.wireOp",EDGE,"E4"),sQuery(id+"F0.wireOp",EDGE,"E5"),sQuery(id+"F0.wireOp",EDGE,"E7"),sQuery(id+"F0.wireOp",EDGE,"E8"),sQuery(id+"F0.wireOp",EDGE,"E9.5.30.0"),sQuery(id+"F0.wireOp",EDGE,"E9.7.30.0"),sQuery(id+"F0.wireOp",EDGE,"E9.9.30.0"),sQuery(id+"F0.wireOp",EDGE,"E9.11.30.0"),sQuery(id+"F0.wireOp",EDGE,"E9.13.30.0"),sQuery(id+"F0.wireOp",EDGE,"E9.15.30.0"),sQuery(id+"F0.wireOp",EDGE,"E9.17.30.0"),sQuery(id+"F0.wireOp",EDGE,"E9.19.30.0"),sQuery(id+"F0.wireOp",EDGE,"E9.21.30.0"),sQuery(id+"F0.wireOp",EDGE,"E9.3.31.0"),sQuery(id+"F0.wireOp",EDGE,"E9.5.31.0"),sQuery(id+"F0.wireOp",EDGE,"E9.7.31.0"),sQuery(id+"F0.wireOp",EDGE,"E9.9.31.0"),sQuery(id+"F0.wireOp",EDGE,"E9.11.31.0"),sQuery(id+"F0.wireOp",EDGE,"E9.13.31.0"),sQuery(id+"F0.wireOp",EDGE,"E9.15.31.0"),sQuery(id+"F0.wireOp",EDGE,"E9.17.31.0"),sQuery(id+"F0.wireOp",EDGE,"E9.19.31.0"),sQuery(id+"F0.wireOp",EDGE,"E9.21.31.0"),sQuery(id+"F0.wireOp",EDGE,"E9.3.32.0"),sQuery(id+"F0.wireOp",EDGE,"E9.5.32.0"),sQuery(id+"F0.wireOp",EDGE,"E9.7.32.0"),sQuery(id+"F0.wireOp",EDGE,"E9.9.32.0"),sQuery(id+"F0.wireOp",EDGE,"E9.11.32.0"),sQuery(id+"F0.wireOp",EDGE,"E9.13.32.0"),sQuery(id+"F0.wireOp",EDGE,"E9.15.32.0"),sQuery(id+"F0.wireOp",EDGE,"E9.17.32.0"),sQuery(id+"F0.wireOp",EDGE,"E9.19.32.0"),sQuery(id+"F0.wireOp",EDGE,"E9.21.32.0"),sQuery(id+"F0.wireOp",EDGE,"E9.3.33.0"),sQuery(id+"F0.wireOp",EDGE,"E9.5.33.0"),sQuery(id+"F0.wireOp",EDGE,"E9.7.33.0"),sQuery(id+"F0.wireOp",EDGE,"E9.9.33.0"),sQuery(id+"F0.wireOp",EDGE,"E9.11.33.0"),sQuery(id+"F0.wireOp",EDGE,"E9.13.33.0"),sQuery(id+"F0.wireOp",EDGE,"E9.15.33.0"),sQuery(id+"F0.wireOp",EDGE,"E9.17.33.0"),sQuery(id+"F0.wireOp",EDGE,"E9.19.33.0"),sQuery(id+"F0.wireOp",EDGE,"E9.21.33.0"),sQuery(id+"F0.wireOp",EDGE,"E9.3.34.0"),sQuery(id+"F0.wireOp",EDGE,"E9.5.34.0"),sQuery(id+"F0.wireOp",EDGE,"E9.7.34.0"),sQuery(id+"F0.wireOp",EDGE,"E9.9.34.0"),sQuery(id+"F0.wireOp",EDGE,"E9.11.34.0"),sQuery(id+"F0.wireOp",EDGE,"E9.13.34.0"),sQuery(id+"F0.wireOp",EDGE,"E9.15.34.0"),sQuery(id+"F0.wireOp",EDGE,"E9.17.34.0"),sQuery(id+"F0.wireOp",EDGE,"E9.19.34.0"),sQuery(id+"F0.wireOp",EDGE,"E9.21.34.0"),sQuery(id+"F0.wireOp",EDGE,"E9.3.35.0"),sQuery(id+"F0.wireOp",EDGE,"E9.5.35.0"),sQuery(id+"F0.wireOp",EDGE,"E9.7.35.0"),sQuery(id+"F0.wireOp",EDGE,"E9.9.35.0"),sQuery(id+"F0.wireOp",EDGE,"E9.11.35.0"),sQuery(id+"F0.wireOp",EDGE,"E9.13.35.0"),sQuery(id+"F0.wireOp",EDGE,"E9.15.35.0"),sQuery(id+"F0.wireOp",EDGE,"E9.17.35.0"),sQuery(id+"F0.wireOp",EDGE,"E9.19.35.0"),sQuery(id+"F0.wireOp",EDGE,"E9.21.35.0"),sQuery(id+"F0.wireOp",EDGE,"E9.3.36.0"),sQuery(id+"F0.wireOp",EDGE,"E9.5.36.0"),sQuery(id+"F0.wireOp",EDGE,"E9.7.36.0"),sQuery(id+"F0.wireOp",EDGE,"E9.9.36.0"),sQuery(id+"F0.wireOp",EDGE,"E9.11.36.0"),sQuery(id+"F0.wireOp",EDGE,"E9.13.36.0"),sQuery(id+"F0.wireOp",EDGE,"E9.15.36.0"),sQuery(id+"F0.wireOp",EDGE,"E9.17.36.0"),sQuery(id+"F0.wireOp",EDGE,"E9.19.36.0"),sQuery(id+"F0.wireOp",EDGE,"E9.21.36.0"),sQuery(id+"F0.wireOp",EDGE,"E9.3.37.0"),sQuery(id+"F0.wireOp",EDGE,"E9.5.37.0"),sQuery(id+"F0.wireOp",EDGE,"E9.7.37.0"),sQuery(id+"F0.wireOp",EDGE,"E9.9.37.0"),sQuery(id+"F0.wireOp",EDGE,"E9.11.37.0"),sQuery(id+"F0.wireOp",EDGE,"E9.13.37.0"),sQuery(id+"F0.wireOp",EDGE,"E9.15.37.0"),sQuery(id+"F0.wireOp",EDGE,"E9.17.37.0"),sQuery(id+"F0.wireOp",EDGE,"E9.19.37.0"),sQuery(id+"F0.wireOp",EDGE,"E9.21.37.0"),sQuery(id+"F0.wireOp",EDGE,"E9.3.38.0"),sQuery(id+"F0.wireOp",EDGE,"E9.5.38.0"),sQuery(id+"F0.wireOp",EDGE,"E9.7.38.0"),sQuery(id+"F0.wireOp",EDGE,"E9.9.38.0"),sQuery(id+"F0.wireOp",EDGE,"E9.11.38.0"),sQuery(id+"F0.wireOp",EDGE,"E9.13.38.0"),sQuery(id+"F0.wireOp",EDGE,"E9.15.38.0"),sQuery(id+"F0.wireOp",EDGE,"E9.17.38.0"),sQuery(id+"F0.wireOp",EDGE,"E9.19.38.0"),sQuery(id+"F0.wireOp",EDGE,"E9.21.38.0"),sQuery(id+"F0.wireOp",EDGE,"E9.3.39.0"),sQuery(id+"F0.wireOp",EDGE,"E9.5.39.0"),sQuery(id+"F0.wireOp",EDGE,"E9.7.39.0"),sQuery(id+"F0.wireOp",EDGE,"E9.9.39.0"),sQuery(id+"F0.wireOp",EDGE,"E9.11.39.0"),sQuery(id+"F0.wireOp",EDGE,"E9.13.39.0"),sQuery(id+"F0.wireOp",EDGE,"E9.15.39.0"),sQuery(id+"F0.wireOp",EDGE,"E9.17.39.0"),sQuery(id+"F0.wireOp",EDGE,"E9.19.39.0"),sQuery(id+"F0.wireOp",EDGE,"E9.21.39.0"),sQuery(id+"F0.wireOp",EDGE,"E9.3.40.0"),sQuery(id+"F0.wireOp",EDGE,"E9.5.40.0"),sQuery(id+"F0.wireOp",EDGE,"E9.7.40.0"),sQuery(id+"F0.wireOp",EDGE,"E9.9.40.0"),sQuery(id+"F0.wireOp",EDGE,"E9.11.40.0"),sQuery(id+"F0.wireOp",EDGE,"E9.13.40.0"),sQuery(id+"F0.wireOp",EDGE,"E9.15.40.0"),sQuery(id+"F0.wireOp",EDGE,"E9.17.40.0"),sQuery(id+"F0.wireOp",EDGE,"E9.19.40.0"),sQuery(id+"F0.wireOp",EDGE,"E9.21.40.0"),sQuery(id+"F0.wireOp",EDGE,"E9.3.41.0"),sQuery(id+"F0.wireOp",EDGE,"E9.5.41.0"),sQuery(id+"F0.wireOp",EDGE,"E9.7.41.0"),sQuery(id+"F0.wireOp",EDGE,"E9.9.41.0"),sQuery(id+"F0.wireOp",EDGE,"E9.11.41.0"),sQuery(id+"F0.wireOp",EDGE,"E9.13.41.0"),sQuery(id+"F0.wireOp",EDGE,"E9.15.41.0"),sQuery(id+"F0.wireOp",EDGE,"E9.17.41.0"),sQuery(id+"F0.wireOp",EDGE,"E9.19.41.0"),sQuery(id+"F0.wireOp",EDGE,"E9.21.41.0"),sQuery(id+"F0.wireOp",EDGE,"E9.3.42.0"),sQuery(id+"F0.wireOp",EDGE,"E9.5.42.0"),sQuery(id+"F0.wireOp",EDGE,"E9.7.42.0"),sQuery(id+"F0.wireOp",EDGE,"E9.9.42.0"),sQuery(id+"F0.wireOp",EDGE,"E9.11.42.0"),sQuery(id+"F0.wireOp",EDGE,"E9.13.42.0"),sQuery(id+"F0.wireOp",EDGE,"E9.15.42.0"),sQuery(id+"F0.wireOp",EDGE,"E9.17.42.0"),sQuery(id+"F0.wireOp",EDGE,"E9.19.42.0"),sQuery(id+"F0.wireOp",EDGE,"E9.21.42.0"),sQuery(id+"F0.wireOp",EDGE,"E9.3.43.0"),sQuery(id+"F0.wireOp",EDGE,"E9.5.43.0"),sQuery(id+"F0.wireOp",EDGE,"E9.7.43.0"),sQuery(id+"F0.wireOp",EDGE,"E9.9.43.0"),sQuery(id+"F0.wireOp",EDGE,"E9.11.43.0"),sQuery(id+"F0.wireOp",EDGE,"E9.13.43.0"),sQuery(id+"F0.wireOp",EDGE,"E9.15.43.0"),sQuery(id+"F0.wireOp",EDGE,"E9.17.43.0"),sQuery(id+"F0.wireOp",EDGE,"E9.19.43.0"),sQuery(id+"F0.wireOp",EDGE,"E9.21.43.0"),sQuery(id+"F0.wireOp",EDGE,"E9.3.44.0"),sQuery(id+"F0.wireOp",EDGE,"E9.5.44.0"),sQuery(id+"F0.wireOp",EDGE,"E9.7.44.0"),sQuery(id+"F0.wireOp",EDGE,"E9.9.44.0"),sQuery(id+"F0.wireOp",EDGE,"E9.11.44.0"),sQuery(id+"F0.wireOp",EDGE,"E9.13.44.0"),sQuery(id+"F0.wireOp",EDGE,"E9.15.44.0"),sQuery(id+"F0.wireOp",EDGE,"E9.17.44.0"),sQuery(id+"F0.wireOp",EDGE,"E9.19.44.0"),sQuery(id+"F0.wireOp",EDGE,"E9.21.44.0"),sQuery(id+"F0.wireOp",EDGE,"E9.3.45.0"),sQuery(id+"F0.wireOp",EDGE,"E9.5.45.0"),sQuery(id+"F0.wireOp",EDGE,"E9.7.45.0"),sQuery(id+"F0.wireOp",EDGE,"E9.9.45.0"),sQuery(id+"F0.wireOp",EDGE,"E9.11.45.0"),sQuery(id+"F0.wireOp",EDGE,"E9.13.45.0"),sQuery(id+"F0.wireOp",EDGE,"E9.15.45.0"),sQuery(id+"F0.wireOp",EDGE,"E9.17.45.0"),sQuery(id+"F0.wireOp",EDGE,"E9.19.45.0"),sQuery(id+"F0.wireOp",EDGE,"E9.21.45.0"),sQuery(id+"F0.wireOp",EDGE,"E9.3.46.0"),sQuery(id+"F0.wireOp",EDGE,"E9.5.46.0"),sQuery(id+"F0.wireOp",EDGE,"E9.7.46.0"),sQuery(id+"F0.wireOp",EDGE,"E9.9.46.0"),sQuery(id+"F0.wireOp",EDGE,"E9.11.46.0"),sQuery(id+"F0.wireOp",EDGE,"E9.13.46.0"),sQuery(id+"F0.wireOp",EDGE,"E9.15.46.0"),sQuery(id+"F0.wireOp",EDGE,"E9.17.46.0"),sQuery(id+"F0.wireOp",EDGE,"E9.19.46.0"),sQuery(id+"F0.wireOp",EDGE,"E9.21.46.0"),sQuery(id+"F0.wireOp",EDGE,"E21.5.30.0"),sQuery(id+"F0.wireOp",EDGE,"E23"),sQuery(id+"F0.wireOp",EDGE,"E24"),sQuery(id+"F0.wireOp",EDGE,"E25")])]});
            transform(context, id + "F4", {"entities" : qUnion([Q0]), "transformType" : TransformType.TRANSLATION_3D, "dx" : (2 * 22.87) * mm, "dy" : 0 * mm, "dz" : 0 * mm, "makeCopy" : true});
        }
        {
            var Q0;
            Q0=makeQuery(id+"F2.opExtrude","SWEPT_BODY",BODY,{"disambiguationData":[OSD([sQuery(id+"F0.wireOp",EDGE,"E1.8.0.0"),sQuery(id+"F0.wireOp",EDGE,"E2.1.0.2"),sQuery(id+"F0.wireOp",EDGE,"E2.2.0.2"),sQuery(id+"F0.wireOp",EDGE,"E2.3.0.2"),sQuery(id+"F0.wireOp",EDGE,"E2.4.0.2"),sQuery(id+"F0.wireOp",EDGE,"E2.5.0.2"),sQuery(id+"F0.wireOp",EDGE,"E2.6.0.2"),sQuery(id+"F0.wireOp",EDGE,"E2.7.0.2"),sQuery(id+"F0.wireOp",EDGE,"E2.8.0.2"),sQuery(id+"F0.wireOp",EDGE,"E2.9.0.2"),sQuery(id+"F0.wireOp",EDGE,"E2.10.0.2"),sQuery(id+"F0.wireOp",EDGE,"E2.11.0.2"),sQuery(id+"F0.wireOp",EDGE,"E2.12.0.2"),sQuery(id+"F0.wireOp",EDGE,"E2.13.0.2"),sQuery(id+"F0.wireOp",EDGE,"E2.14.0.2"),sQuery(id+"F0.wireOp",EDGE,"E2.15.0.2"),sQuery(id+"F0.wireOp",EDGE,"E2.16.0.2"),sQuery(id+"F0.wireOp",EDGE,"E2.17.0.2"),sQuery(id+"F0.wireOp",EDGE,"E2.18.0.2"),sQuery(id+"F0.wireOp",EDGE,"E2.19.0.2"),sQuery(id+"F0.wireOp",EDGE,"E2.20.0.2"),sQuery(id+"F0.wireOp",EDGE,"E2.21.0.2"),sQuery(id+"F0.wireOp",EDGE,"E2.22.0.2"),sQuery(id+"F0.wireOp",EDGE,"E2.23.0.2"),sQuery(id+"F0.wireOp",EDGE,"E2.24.0.2"),sQuery(id+"F0.wireOp",EDGE,"E2.25.0.2"),sQuery(id+"F0.wireOp",EDGE,"E2.26.0.2"),sQuery(id+"F0.wireOp",EDGE,"E2.27.0.2"),sQuery(id+"F0.wireOp",EDGE,"E2.28.0.2"),sQuery(id+"F0.wireOp",EDGE,"E2.29.0.2"),sQuery(id+"F0.wireOp",EDGE,"E9.5.30.0"),sQuery(id+"F0.wireOp",EDGE,"E9.5.31.0"),sQuery(id+"F0.wireOp",EDGE,"E9.5.32.0"),sQuery(id+"F0.wireOp",EDGE,"E9.5.33.0"),sQuery(id+"F0.wireOp",EDGE,"E9.5.34.0"),sQuery(id+"F0.wireOp",EDGE,"E9.5.35.0"),sQuery(id+"F0.wireOp",EDGE,"E9.5.36.0"),sQuery(id+"F0.wireOp",EDGE,"E9.5.37.0"),sQuery(id+"F0.wireOp",EDGE,"E9.5.38.0"),sQuery(id+"F0.wireOp",EDGE,"E9.5.39.0"),sQuery(id+"F0.wireOp",EDGE,"E9.5.40.0"),sQuery(id+"F0.wireOp",EDGE,"E9.5.41.0"),sQuery(id+"F0.wireOp",EDGE,"E9.5.42.0"),sQuery(id+"F0.wireOp",EDGE,"E9.5.43.0"),sQuery(id+"F0.wireOp",EDGE,"E9.5.44.0"),sQuery(id+"F0.wireOp",EDGE,"E9.5.45.0"),sQuery(id+"F0.wireOp",EDGE,"E9.5.46.0"),sQuery(id+"F0.wireOp",EDGE,"E19.rect.top"),sQuery(id+"F0.wireOp",EDGE,"E19.rect.left"),sQuery(id+"F0.wireOp",EDGE,"E19.rect.right"),sQuery(id+"F0.wireOp",EDGE,"E22")])]});
            transform(context, id + "F5", {"entities" : qUnion([Q0]), "transformType" : TransformType.TRANSLATION_3D, "dx" : 2.54 * mm, "dy" : 0 * mm, "dz" : 0 * mm, "makeCopy" : true});
        }
        {
            var Q0;
            Q0=makeQuery(id+"F2.opExtrude","SWEPT_BODY",BODY,{"disambiguationData":[OSD([sQuery(id+"F0.wireOp",EDGE,"E1.9.0.0"),sQuery(id+"F0.wireOp",EDGE,"E2.1.0.1"),sQuery(id+"F0.wireOp",EDGE,"E2.2.0.1"),sQuery(id+"F0.wireOp",EDGE,"E2.3.0.1"),sQuery(id+"F0.wireOp",EDGE,"E2.4.0.1"),sQuery(id+"F0.wireOp",EDGE,"E2.5.0.1"),sQuery(id+"F0.wireOp",EDGE,"E2.6.0.1"),sQuery(id+"F0.wireOp",EDGE,"E2.7.0.1"),sQuery(id+"F0.wireOp",EDGE,"E2.8.0.1"),sQuery(id+"F0.wireOp",EDGE,"E2.9.0.1"),sQuery(id+"F0.wireOp",EDGE,"E2.10.0.1"),sQuery(id+"F0.wireOp",EDGE,"E2.11.0.1"),sQuery(id+"F0.wireOp",EDGE,"E2.12.0.1"),sQuery(id+"F0.wireOp",EDGE,"E2.13.0.1"),sQuery(id+"F0.wireOp",EDGE,"E2.14.0.1"),sQuery(id+"F0.wireOp",EDGE,"E2.15.0.1"),sQuery(id+"F0.wireOp",EDGE,"E2.16.0.1"),sQuery(id+"F0.wireOp",EDGE,"E2.17.0.1"),sQuery(id+"F0.wireOp",EDGE,"E2.18.0.1"),sQuery(id+"F0.wireOp",EDGE,"E2.19.0.1"),sQuery(id+"F0.wireOp",EDGE,"E2.20.0.1"),sQuery(id+"F0.wireOp",EDGE,"E2.21.0.1"),sQuery(id+"F0.wireOp",EDGE,"E2.22.0.1"),sQuery(id+"F0.wireOp",EDGE,"E2.23.0.1"),sQuery(id+"F0.wireOp",EDGE,"E2.24.0.1"),sQuery(id+"F0.wireOp",EDGE,"E2.25.0.1"),sQuery(id+"F0.wireOp",EDGE,"E2.26.0.1"),sQuery(id+"F0.wireOp",EDGE,"E2.27.0.1"),sQuery(id+"F0.wireOp",EDGE,"E2.28.0.1"),sQuery(id+"F0.wireOp",EDGE,"E2.29.0.1"),sQuery(id+"F0.wireOp",EDGE,"E5"),sQuery(id+"F0.wireOp",EDGE,"E9.3.31.0"),sQuery(id+"F0.wireOp",EDGE,"E9.3.32.0"),sQuery(id+"F0.wireOp",EDGE,"E9.3.33.0"),sQuery(id+"F0.wireOp",EDGE,"E9.3.34.0"),sQuery(id+"F0.wireOp",EDGE,"E9.3.35.0"),sQuery(id+"F0.wireOp",EDGE,"E9.3.36.0"),sQuery(id+"F0.wireOp",EDGE,"E9.3.37.0"),sQuery(id+"F0.wireOp",EDGE,"E9.3.38.0"),sQuery(id+"F0.wireOp",EDGE,"E9.3.39.0"),sQuery(id+"F0.wireOp",EDGE,"E9.3.40.0"),sQuery(id+"F0.wireOp",EDGE,"E9.3.41.0"),sQuery(id+"F0.wireOp",EDGE,"E9.3.42.0"),sQuery(id+"F0.wireOp",EDGE,"E9.3.43.0"),sQuery(id+"F0.wireOp",EDGE,"E9.3.44.0"),sQuery(id+"F0.wireOp",EDGE,"E9.3.45.0"),sQuery(id+"F0.wireOp",EDGE,"E9.3.46.0"),sQuery(id+"F0.wireOp",EDGE,"E20.rect.top"),sQuery(id+"F0.wireOp",EDGE,"E20.rect.left"),sQuery(id+"F0.wireOp",EDGE,"E21.5.30.0"),sQuery(id+"F0.wireOp",EDGE,"E22"),sQuery(id+"F0.wireOp",EDGE,"E25"),sQuery(id+"F0.wireOp",EDGE,"E26")])]});
            transform(context, id + "F6", {"entities" : qUnion([Q0]), "transformType" : TransformType.TRANSLATION_3D, "dx" : (2.54 * 27) * mm, "dy" : 0 * mm, "dz" : 0 * mm, "makeCopy" : false});
        }
        {
            var Q0;
            Q0=makeQuery(id+"F5.opPattern","COPY",BODY,{"derivedFrom":makeQuery(id+"F2.opExtrude","SWEPT_BODY",BODY,{"disambiguationData":[OSD([sQuery(id+"F0.wireOp",EDGE,"E1.8.0.0"),sQuery(id+"F0.wireOp",EDGE,"E2.1.0.2"),sQuery(id+"F0.wireOp",EDGE,"E2.2.0.2"),sQuery(id+"F0.wireOp",EDGE,"E2.3.0.2"),sQuery(id+"F0.wireOp",EDGE,"E2.4.0.2"),sQuery(id+"F0.wireOp",EDGE,"E2.5.0.2"),sQuery(id+"F0.wireOp",EDGE,"E2.6.0.2"),sQuery(id+"F0.wireOp",EDGE,"E2.7.0.2"),sQuery(id+"F0.wireOp",EDGE,"E2.8.0.2"),sQuery(id+"F0.wireOp",EDGE,"E2.9.0.2"),sQuery(id+"F0.wireOp",EDGE,"E2.10.0.2"),sQuery(id+"F0.wireOp",EDGE,"E2.11.0.2"),sQuery(id+"F0.wireOp",EDGE,"E2.12.0.2"),sQuery(id+"F0.wireOp",EDGE,"E2.13.0.2"),sQuery(id+"F0.wireOp",EDGE,"E2.14.0.2"),sQuery(id+"F0.wireOp",EDGE,"E2.15.0.2"),sQuery(id+"F0.wireOp",EDGE,"E2.16.0.2"),sQuery(id+"F0.wireOp",EDGE,"E2.17.0.2"),sQuery(id+"F0.wireOp",EDGE,"E2.18.0.2"),sQuery(id+"F0.wireOp",EDGE,"E2.19.0.2"),sQuery(id+"F0.wireOp",EDGE,"E2.20.0.2"),sQuery(id+"F0.wireOp",EDGE,"E2.21.0.2"),sQuery(id+"F0.wireOp",EDGE,"E2.22.0.2"),sQuery(id+"F0.wireOp",EDGE,"E2.23.0.2"),sQuery(id+"F0.wireOp",EDGE,"E2.24.0.2"),sQuery(id+"F0.wireOp",EDGE,"E2.25.0.2"),sQuery(id+"F0.wireOp",EDGE,"E2.26.0.2"),sQuery(id+"F0.wireOp",EDGE,"E2.27.0.2"),sQuery(id+"F0.wireOp",EDGE,"E2.28.0.2"),sQuery(id+"F0.wireOp",EDGE,"E2.29.0.2"),sQuery(id+"F0.wireOp",EDGE,"E9.5.30.0"),sQuery(id+"F0.wireOp",EDGE,"E9.5.31.0"),sQuery(id+"F0.wireOp",EDGE,"E9.5.32.0"),sQuery(id+"F0.wireOp",EDGE,"E9.5.33.0"),sQuery(id+"F0.wireOp",EDGE,"E9.5.34.0"),sQuery(id+"F0.wireOp",EDGE,"E9.5.35.0"),sQuery(id+"F0.wireOp",EDGE,"E9.5.36.0"),sQuery(id+"F0.wireOp",EDGE,"E9.5.37.0"),sQuery(id+"F0.wireOp",EDGE,"E9.5.38.0"),sQuery(id+"F0.wireOp",EDGE,"E9.5.39.0"),sQuery(id+"F0.wireOp",EDGE,"E9.5.40.0"),sQuery(id+"F0.wireOp",EDGE,"E9.5.41.0"),sQuery(id+"F0.wireOp",EDGE,"E9.5.42.0"),sQuery(id+"F0.wireOp",EDGE,"E9.5.43.0"),sQuery(id+"F0.wireOp",EDGE,"E9.5.44.0"),sQuery(id+"F0.wireOp",EDGE,"E9.5.45.0"),sQuery(id+"F0.wireOp",EDGE,"E9.5.46.0"),sQuery(id+"F0.wireOp",EDGE,"E19.rect.top"),sQuery(id+"F0.wireOp",EDGE,"E19.rect.left"),sQuery(id+"F0.wireOp",EDGE,"E19.rect.right"),sQuery(id+"F0.wireOp",EDGE,"E22")])]}),"instanceName":"1"});
            transform(context, id + "F7", {"entities" : qUnion([Q0]), "transformType" : TransformType.TRANSLATION_3D, "dx" : 2.54 * mm, "dy" : 0 * mm, "dz" : 0 * mm, "makeCopy" : true});
        }
        {
            var Q0;
            Q0=makeQuery(id+"F7.opPattern","COPY",BODY,{"derivedFrom":makeQuery(id+"F5.opPattern","COPY",BODY,{"derivedFrom":makeQuery(id+"F2.opExtrude","SWEPT_BODY",BODY,{"disambiguationData":[OSD([sQuery(id+"F0.wireOp",EDGE,"E1.8.0.0"),sQuery(id+"F0.wireOp",EDGE,"E2.1.0.2"),sQuery(id+"F0.wireOp",EDGE,"E2.2.0.2"),sQuery(id+"F0.wireOp",EDGE,"E2.3.0.2"),sQuery(id+"F0.wireOp",EDGE,"E2.4.0.2"),sQuery(id+"F0.wireOp",EDGE,"E2.5.0.2"),sQuery(id+"F0.wireOp",EDGE,"E2.6.0.2"),sQuery(id+"F0.wireOp",EDGE,"E2.7.0.2"),sQuery(id+"F0.wireOp",EDGE,"E2.8.0.2"),sQuery(id+"F0.wireOp",EDGE,"E2.9.0.2"),sQuery(id+"F0.wireOp",EDGE,"E2.10.0.2"),sQuery(id+"F0.wireOp",EDGE,"E2.11.0.2"),sQuery(id+"F0.wireOp",EDGE,"E2.12.0.2"),sQuery(id+"F0.wireOp",EDGE,"E2.13.0.2"),sQuery(id+"F0.wireOp",EDGE,"E2.14.0.2"),sQuery(id+"F0.wireOp",EDGE,"E2.15.0.2"),sQuery(id+"F0.wireOp",EDGE,"E2.16.0.2"),sQuery(id+"F0.wireOp",EDGE,"E2.17.0.2"),sQuery(id+"F0.wireOp",EDGE,"E2.18.0.2"),sQuery(id+"F0.wireOp",EDGE,"E2.19.0.2"),sQuery(id+"F0.wireOp",EDGE,"E2.20.0.2"),sQuery(id+"F0.wireOp",EDGE,"E2.21.0.2"),sQuery(id+"F0.wireOp",EDGE,"E2.22.0.2"),sQuery(id+"F0.wireOp",EDGE,"E2.23.0.2"),sQuery(id+"F0.wireOp",EDGE,"E2.24.0.2"),sQuery(id+"F0.wireOp",EDGE,"E2.25.0.2"),sQuery(id+"F0.wireOp",EDGE,"E2.26.0.2"),sQuery(id+"F0.wireOp",EDGE,"E2.27.0.2"),sQuery(id+"F0.wireOp",EDGE,"E2.28.0.2"),sQuery(id+"F0.wireOp",EDGE,"E2.29.0.2"),sQuery(id+"F0.wireOp",EDGE,"E9.5.30.0"),sQuery(id+"F0.wireOp",EDGE,"E9.5.31.0"),sQuery(id+"F0.wireOp",EDGE,"E9.5.32.0"),sQuery(id+"F0.wireOp",EDGE,"E9.5.33.0"),sQuery(id+"F0.wireOp",EDGE,"E9.5.34.0"),sQuery(id+"F0.wireOp",EDGE,"E9.5.35.0"),sQuery(id+"F0.wireOp",EDGE,"E9.5.36.0"),sQuery(id+"F0.wireOp",EDGE,"E9.5.37.0"),sQuery(id+"F0.wireOp",EDGE,"E9.5.38.0"),sQuery(id+"F0.wireOp",EDGE,"E9.5.39.0"),sQuery(id+"F0.wireOp",EDGE,"E9.5.40.0"),sQuery(id+"F0.wireOp",EDGE,"E9.5.41.0"),sQuery(id+"F0.wireOp",EDGE,"E9.5.42.0"),sQuery(id+"F0.wireOp",EDGE,"E9.5.43.0"),sQuery(id+"F0.wireOp",EDGE,"E9.5.44.0"),sQuery(id+"F0.wireOp",EDGE,"E9.5.45.0"),sQuery(id+"F0.wireOp",EDGE,"E9.5.46.0"),sQuery(id+"F0.wireOp",EDGE,"E19.rect.top"),sQuery(id+"F0.wireOp",EDGE,"E19.rect.left"),sQuery(id+"F0.wireOp",EDGE,"E19.rect.right"),sQuery(id+"F0.wireOp",EDGE,"E22")])]}),"instanceName":"1"}),"instanceName":"1"});
            transform(context, id + "F8", {"entities" : qUnion([Q0]), "transformType" : TransformType.TRANSLATION_3D, "dx" : 2.54 * mm, "dy" : 0 * mm, "dz" : 0 * mm, "makeCopy" : true});
        }
        {
            var Q0;
            Q0=makeQuery(id+"F8.opPattern","COPY",BODY,{"derivedFrom":makeQuery(id+"F7.opPattern","COPY",BODY,{"derivedFrom":makeQuery(id+"F5.opPattern","COPY",BODY,{"derivedFrom":makeQuery(id+"F2.opExtrude","SWEPT_BODY",BODY,{"disambiguationData":[OSD([sQuery(id+"F0.wireOp",EDGE,"E1.8.0.0"),sQuery(id+"F0.wireOp",EDGE,"E2.1.0.2"),sQuery(id+"F0.wireOp",EDGE,"E2.2.0.2"),sQuery(id+"F0.wireOp",EDGE,"E2.3.0.2"),sQuery(id+"F0.wireOp",EDGE,"E2.4.0.2"),sQuery(id+"F0.wireOp",EDGE,"E2.5.0.2"),sQuery(id+"F0.wireOp",EDGE,"E2.6.0.2"),sQuery(id+"F0.wireOp",EDGE,"E2.7.0.2"),sQuery(id+"F0.wireOp",EDGE,"E2.8.0.2"),sQuery(id+"F0.wireOp",EDGE,"E2.9.0.2"),sQuery(id+"F0.wireOp",EDGE,"E2.10.0.2"),sQuery(id+"F0.wireOp",EDGE,"E2.11.0.2"),sQuery(id+"F0.wireOp",EDGE,"E2.12.0.2"),sQuery(id+"F0.wireOp",EDGE,"E2.13.0.2"),sQuery(id+"F0.wireOp",EDGE,"E2.14.0.2"),sQuery(id+"F0.wireOp",EDGE,"E2.15.0.2"),sQuery(id+"F0.wireOp",EDGE,"E2.16.0.2"),sQuery(id+"F0.wireOp",EDGE,"E2.17.0.2"),sQuery(id+"F0.wireOp",EDGE,"E2.18.0.2"),sQuery(id+"F0.wireOp",EDGE,"E2.19.0.2"),sQuery(id+"F0.wireOp",EDGE,"E2.20.0.2"),sQuery(id+"F0.wireOp",EDGE,"E2.21.0.2"),sQuery(id+"F0.wireOp",EDGE,"E2.22.0.2"),sQuery(id+"F0.wireOp",EDGE,"E2.23.0.2"),sQuery(id+"F0.wireOp",EDGE,"E2.24.0.2"),sQuery(id+"F0.wireOp",EDGE,"E2.25.0.2"),sQuery(id+"F0.wireOp",EDGE,"E2.26.0.2"),sQuery(id+"F0.wireOp",EDGE,"E2.27.0.2"),sQuery(id+"F0.wireOp",EDGE,"E2.28.0.2"),sQuery(id+"F0.wireOp",EDGE,"E2.29.0.2"),sQuery(id+"F0.wireOp",EDGE,"E9.5.30.0"),sQuery(id+"F0.wireOp",EDGE,"E9.5.31.0"),sQuery(id+"F0.wireOp",EDGE,"E9.5.32.0"),sQuery(id+"F0.wireOp",EDGE,"E9.5.33.0"),sQuery(id+"F0.wireOp",EDGE,"E9.5.34.0"),sQuery(id+"F0.wireOp",EDGE,"E9.5.35.0"),sQuery(id+"F0.wireOp",EDGE,"E9.5.36.0"),sQuery(id+"F0.wireOp",EDGE,"E9.5.37.0"),sQuery(id+"F0.wireOp",EDGE,"E9.5.38.0"),sQuery(id+"F0.wireOp",EDGE,"E9.5.39.0"),sQuery(id+"F0.wireOp",EDGE,"E9.5.40.0"),sQuery(id+"F0.wireOp",EDGE,"E9.5.41.0"),sQuery(id+"F0.wireOp",EDGE,"E9.5.42.0"),sQuery(id+"F0.wireOp",EDGE,"E9.5.43.0"),sQuery(id+"F0.wireOp",EDGE,"E9.5.44.0"),sQuery(id+"F0.wireOp",EDGE,"E9.5.45.0"),sQuery(id+"F0.wireOp",EDGE,"E9.5.46.0"),sQuery(id+"F0.wireOp",EDGE,"E19.rect.top"),sQuery(id+"F0.wireOp",EDGE,"E19.rect.left"),sQuery(id+"F0.wireOp",EDGE,"E19.rect.right"),sQuery(id+"F0.wireOp",EDGE,"E22")])]}),"instanceName":"1"}),"instanceName":"1"}),"instanceName":"1"});
            transform(context, id + "F9", {"entities" : qUnion([Q0]), "transformType" : TransformType.TRANSLATION_3D, "dx" : 2.54 * mm, "dy" : 0 * mm, "dz" : 0 * mm, "makeCopy" : true});
        }
        {
            var Q0;
            Q0=makeQuery(id+"F9.opPattern","COPY",BODY,{"derivedFrom":makeQuery(id+"F8.opPattern","COPY",BODY,{"derivedFrom":makeQuery(id+"F7.opPattern","COPY",BODY,{"derivedFrom":makeQuery(id+"F5.opPattern","COPY",BODY,{"derivedFrom":makeQuery(id+"F2.opExtrude","SWEPT_BODY",BODY,{"disambiguationData":[OSD([sQuery(id+"F0.wireOp",EDGE,"E1.8.0.0"),sQuery(id+"F0.wireOp",EDGE,"E2.1.0.2"),sQuery(id+"F0.wireOp",EDGE,"E2.2.0.2"),sQuery(id+"F0.wireOp",EDGE,"E2.3.0.2"),sQuery(id+"F0.wireOp",EDGE,"E2.4.0.2"),sQuery(id+"F0.wireOp",EDGE,"E2.5.0.2"),sQuery(id+"F0.wireOp",EDGE,"E2.6.0.2"),sQuery(id+"F0.wireOp",EDGE,"E2.7.0.2"),sQuery(id+"F0.wireOp",EDGE,"E2.8.0.2"),sQuery(id+"F0.wireOp",EDGE,"E2.9.0.2"),sQuery(id+"F0.wireOp",EDGE,"E2.10.0.2"),sQuery(id+"F0.wireOp",EDGE,"E2.11.0.2"),sQuery(id+"F0.wireOp",EDGE,"E2.12.0.2"),sQuery(id+"F0.wireOp",EDGE,"E2.13.0.2"),sQuery(id+"F0.wireOp",EDGE,"E2.14.0.2"),sQuery(id+"F0.wireOp",EDGE,"E2.15.0.2"),sQuery(id+"F0.wireOp",EDGE,"E2.16.0.2"),sQuery(id+"F0.wireOp",EDGE,"E2.17.0.2"),sQuery(id+"F0.wireOp",EDGE,"E2.18.0.2"),sQuery(id+"F0.wireOp",EDGE,"E2.19.0.2"),sQuery(id+"F0.wireOp",EDGE,"E2.20.0.2"),sQuery(id+"F0.wireOp",EDGE,"E2.21.0.2"),sQuery(id+"F0.wireOp",EDGE,"E2.22.0.2"),sQuery(id+"F0.wireOp",EDGE,"E2.23.0.2"),sQuery(id+"F0.wireOp",EDGE,"E2.24.0.2"),sQuery(id+"F0.wireOp",EDGE,"E2.25.0.2"),sQuery(id+"F0.wireOp",EDGE,"E2.26.0.2"),sQuery(id+"F0.wireOp",EDGE,"E2.27.0.2"),sQuery(id+"F0.wireOp",EDGE,"E2.28.0.2"),sQuery(id+"F0.wireOp",EDGE,"E2.29.0.2"),sQuery(id+"F0.wireOp",EDGE,"E9.5.30.0"),sQuery(id+"F0.wireOp",EDGE,"E9.5.31.0"),sQuery(id+"F0.wireOp",EDGE,"E9.5.32.0"),sQuery(id+"F0.wireOp",EDGE,"E9.5.33.0"),sQuery(id+"F0.wireOp",EDGE,"E9.5.34.0"),sQuery(id+"F0.wireOp",EDGE,"E9.5.35.0"),sQuery(id+"F0.wireOp",EDGE,"E9.5.36.0"),sQuery(id+"F0.wireOp",EDGE,"E9.5.37.0"),sQuery(id+"F0.wireOp",EDGE,"E9.5.38.0"),sQuery(id+"F0.wireOp",EDGE,"E9.5.39.0"),sQuery(id+"F0.wireOp",EDGE,"E9.5.40.0"),sQuery(id+"F0.wireOp",EDGE,"E9.5.41.0"),sQuery(id+"F0.wireOp",EDGE,"E9.5.42.0"),sQuery(id+"F0.wireOp",EDGE,"E9.5.43.0"),sQuery(id+"F0.wireOp",EDGE,"E9.5.44.0"),sQuery(id+"F0.wireOp",EDGE,"E9.5.45.0"),sQuery(id+"F0.wireOp",EDGE,"E9.5.46.0"),sQuery(id+"F0.wireOp",EDGE,"E19.rect.top"),sQuery(id+"F0.wireOp",EDGE,"E19.rect.left"),sQuery(id+"F0.wireOp",EDGE,"E19.rect.right"),sQuery(id+"F0.wireOp",EDGE,"E22")])]}),"instanceName":"1"}),"instanceName":"1"}),"instanceName":"1"}),"instanceName":"1"});
            transform(context, id + "F10", {"entities" : qUnion([Q0]), "transformType" : TransformType.TRANSLATION_3D, "dx" : 2.54 * mm, "dy" : 0 * mm, "dz" : 0 * mm, "makeCopy" : true});
        }
        {
            var Q0;
            Q0=makeQuery(id+"F10.opPattern","COPY",BODY,{"derivedFrom":makeQuery(id+"F9.opPattern","COPY",BODY,{"derivedFrom":makeQuery(id+"F8.opPattern","COPY",BODY,{"derivedFrom":makeQuery(id+"F7.opPattern","COPY",BODY,{"derivedFrom":makeQuery(id+"F5.opPattern","COPY",BODY,{"derivedFrom":makeQuery(id+"F2.opExtrude","SWEPT_BODY",BODY,{"disambiguationData":[OSD([sQuery(id+"F0.wireOp",EDGE,"E1.8.0.0"),sQuery(id+"F0.wireOp",EDGE,"E2.1.0.2"),sQuery(id+"F0.wireOp",EDGE,"E2.2.0.2"),sQuery(id+"F0.wireOp",EDGE,"E2.3.0.2"),sQuery(id+"F0.wireOp",EDGE,"E2.4.0.2"),sQuery(id+"F0.wireOp",EDGE,"E2.5.0.2"),sQuery(id+"F0.wireOp",EDGE,"E2.6.0.2"),sQuery(id+"F0.wireOp",EDGE,"E2.7.0.2"),sQuery(id+"F0.wireOp",EDGE,"E2.8.0.2"),sQuery(id+"F0.wireOp",EDGE,"E2.9.0.2"),sQuery(id+"F0.wireOp",EDGE,"E2.10.0.2"),sQuery(id+"F0.wireOp",EDGE,"E2.11.0.2"),sQuery(id+"F0.wireOp",EDGE,"E2.12.0.2"),sQuery(id+"F0.wireOp",EDGE,"E2.13.0.2"),sQuery(id+"F0.wireOp",EDGE,"E2.14.0.2"),sQuery(id+"F0.wireOp",EDGE,"E2.15.0.2"),sQuery(id+"F0.wireOp",EDGE,"E2.16.0.2"),sQuery(id+"F0.wireOp",EDGE,"E2.17.0.2"),sQuery(id+"F0.wireOp",EDGE,"E2.18.0.2"),sQuery(id+"F0.wireOp",EDGE,"E2.19.0.2"),sQuery(id+"F0.wireOp",EDGE,"E2.20.0.2"),sQuery(id+"F0.wireOp",EDGE,"E2.21.0.2"),sQuery(id+"F0.wireOp",EDGE,"E2.22.0.2"),sQuery(id+"F0.wireOp",EDGE,"E2.23.0.2"),sQuery(id+"F0.wireOp",EDGE,"E2.24.0.2"),sQuery(id+"F0.wireOp",EDGE,"E2.25.0.2"),sQuery(id+"F0.wireOp",EDGE,"E2.26.0.2"),sQuery(id+"F0.wireOp",EDGE,"E2.27.0.2"),sQuery(id+"F0.wireOp",EDGE,"E2.28.0.2"),sQuery(id+"F0.wireOp",EDGE,"E2.29.0.2"),sQuery(id+"F0.wireOp",EDGE,"E9.5.30.0"),sQuery(id+"F0.wireOp",EDGE,"E9.5.31.0"),sQuery(id+"F0.wireOp",EDGE,"E9.5.32.0"),sQuery(id+"F0.wireOp",EDGE,"E9.5.33.0"),sQuery(id+"F0.wireOp",EDGE,"E9.5.34.0"),sQuery(id+"F0.wireOp",EDGE,"E9.5.35.0"),sQuery(id+"F0.wireOp",EDGE,"E9.5.36.0"),sQuery(id+"F0.wireOp",EDGE,"E9.5.37.0"),sQuery(id+"F0.wireOp",EDGE,"E9.5.38.0"),sQuery(id+"F0.wireOp",EDGE,"E9.5.39.0"),sQuery(id+"F0.wireOp",EDGE,"E9.5.40.0"),sQuery(id+"F0.wireOp",EDGE,"E9.5.41.0"),sQuery(id+"F0.wireOp",EDGE,"E9.5.42.0"),sQuery(id+"F0.wireOp",EDGE,"E9.5.43.0"),sQuery(id+"F0.wireOp",EDGE,"E9.5.44.0"),sQuery(id+"F0.wireOp",EDGE,"E9.5.45.0"),sQuery(id+"F0.wireOp",EDGE,"E9.5.46.0"),sQuery(id+"F0.wireOp",EDGE,"E19.rect.top"),sQuery(id+"F0.wireOp",EDGE,"E19.rect.left"),sQuery(id+"F0.wireOp",EDGE,"E19.rect.right"),sQuery(id+"F0.wireOp",EDGE,"E22")])]}),"instanceName":"1"}),"instanceName":"1"}),"instanceName":"1"}),"instanceName":"1"}),"instanceName":"1"});
            transform(context, id + "F11", {"entities" : qUnion([Q0]), "transformType" : TransformType.TRANSLATION_3D, "dx" : 2.54 * mm, "dy" : 0 * mm, "dz" : 0 * mm, "makeCopy" : true});
        }
        {
            var Q0;
            Q0=makeQuery(id+"F11.opPattern","COPY",BODY,{"derivedFrom":makeQuery(id+"F10.opPattern","COPY",BODY,{"derivedFrom":makeQuery(id+"F9.opPattern","COPY",BODY,{"derivedFrom":makeQuery(id+"F8.opPattern","COPY",BODY,{"derivedFrom":makeQuery(id+"F7.opPattern","COPY",BODY,{"derivedFrom":makeQuery(id+"F5.opPattern","COPY",BODY,{"derivedFrom":makeQuery(id+"F2.opExtrude","SWEPT_BODY",BODY,{"disambiguationData":[OSD([sQuery(id+"F0.wireOp",EDGE,"E1.8.0.0"),sQuery(id+"F0.wireOp",EDGE,"E2.1.0.2"),sQuery(id+"F0.wireOp",EDGE,"E2.2.0.2"),sQuery(id+"F0.wireOp",EDGE,"E2.3.0.2"),sQuery(id+"F0.wireOp",EDGE,"E2.4.0.2"),sQuery(id+"F0.wireOp",EDGE,"E2.5.0.2"),sQuery(id+"F0.wireOp",EDGE,"E2.6.0.2"),sQuery(id+"F0.wireOp",EDGE,"E2.7.0.2"),sQuery(id+"F0.wireOp",EDGE,"E2.8.0.2"),sQuery(id+"F0.wireOp",EDGE,"E2.9.0.2"),sQuery(id+"F0.wireOp",EDGE,"E2.10.0.2"),sQuery(id+"F0.wireOp",EDGE,"E2.11.0.2"),sQuery(id+"F0.wireOp",EDGE,"E2.12.0.2"),sQuery(id+"F0.wireOp",EDGE,"E2.13.0.2"),sQuery(id+"F0.wireOp",EDGE,"E2.14.0.2"),sQuery(id+"F0.wireOp",EDGE,"E2.15.0.2"),sQuery(id+"F0.wireOp",EDGE,"E2.16.0.2"),sQuery(id+"F0.wireOp",EDGE,"E2.17.0.2"),sQuery(id+"F0.wireOp",EDGE,"E2.18.0.2"),sQuery(id+"F0.wireOp",EDGE,"E2.19.0.2"),sQuery(id+"F0.wireOp",EDGE,"E2.20.0.2"),sQuery(id+"F0.wireOp",EDGE,"E2.21.0.2"),sQuery(id+"F0.wireOp",EDGE,"E2.22.0.2"),sQuery(id+"F0.wireOp",EDGE,"E2.23.0.2"),sQuery(id+"F0.wireOp",EDGE,"E2.24.0.2"),sQuery(id+"F0.wireOp",EDGE,"E2.25.0.2"),sQuery(id+"F0.wireOp",EDGE,"E2.26.0.2"),sQuery(id+"F0.wireOp",EDGE,"E2.27.0.2"),sQuery(id+"F0.wireOp",EDGE,"E2.28.0.2"),sQuery(id+"F0.wireOp",EDGE,"E2.29.0.2"),sQuery(id+"F0.wireOp",EDGE,"E9.5.30.0"),sQuery(id+"F0.wireOp",EDGE,"E9.5.31.0"),sQuery(id+"F0.wireOp",EDGE,"E9.5.32.0"),sQuery(id+"F0.wireOp",EDGE,"E9.5.33.0"),sQuery(id+"F0.wireOp",EDGE,"E9.5.34.0"),sQuery(id+"F0.wireOp",EDGE,"E9.5.35.0"),sQuery(id+"F0.wireOp",EDGE,"E9.5.36.0"),sQuery(id+"F0.wireOp",EDGE,"E9.5.37.0"),sQuery(id+"F0.wireOp",EDGE,"E9.5.38.0"),sQuery(id+"F0.wireOp",EDGE,"E9.5.39.0"),sQuery(id+"F0.wireOp",EDGE,"E9.5.40.0"),sQuery(id+"F0.wireOp",EDGE,"E9.5.41.0"),sQuery(id+"F0.wireOp",EDGE,"E9.5.42.0"),sQuery(id+"F0.wireOp",EDGE,"E9.5.43.0"),sQuery(id+"F0.wireOp",EDGE,"E9.5.44.0"),sQuery(id+"F0.wireOp",EDGE,"E9.5.45.0"),sQuery(id+"F0.wireOp",EDGE,"E9.5.46.0"),sQuery(id+"F0.wireOp",EDGE,"E19.rect.top"),sQuery(id+"F0.wireOp",EDGE,"E19.rect.left"),sQuery(id+"F0.wireOp",EDGE,"E19.rect.right"),sQuery(id+"F0.wireOp",EDGE,"E22")])]}),"instanceName":"1"}),"instanceName":"1"}),"instanceName":"1"}),"instanceName":"1"}),"instanceName":"1"}),"instanceName":"1"});
            transform(context, id + "F12", {"entities" : qUnion([Q0]), "transformType" : TransformType.TRANSLATION_3D, "dx" : 2.54 * mm, "dy" : 0 * mm, "dz" : 0 * mm, "makeCopy" : true});
        }
        {
            var Q0;
            Q0=makeQuery(id+"F12.opPattern","COPY",BODY,{"derivedFrom":makeQuery(id+"F11.opPattern","COPY",BODY,{"derivedFrom":makeQuery(id+"F10.opPattern","COPY",BODY,{"derivedFrom":makeQuery(id+"F9.opPattern","COPY",BODY,{"derivedFrom":makeQuery(id+"F8.opPattern","COPY",BODY,{"derivedFrom":makeQuery(id+"F7.opPattern","COPY",BODY,{"derivedFrom":makeQuery(id+"F5.opPattern","COPY",BODY,{"derivedFrom":makeQuery(id+"F2.opExtrude","SWEPT_BODY",BODY,{"disambiguationData":[OSD([sQuery(id+"F0.wireOp",EDGE,"E1.8.0.0"),sQuery(id+"F0.wireOp",EDGE,"E2.1.0.2"),sQuery(id+"F0.wireOp",EDGE,"E2.2.0.2"),sQuery(id+"F0.wireOp",EDGE,"E2.3.0.2"),sQuery(id+"F0.wireOp",EDGE,"E2.4.0.2"),sQuery(id+"F0.wireOp",EDGE,"E2.5.0.2"),sQuery(id+"F0.wireOp",EDGE,"E2.6.0.2"),sQuery(id+"F0.wireOp",EDGE,"E2.7.0.2"),sQuery(id+"F0.wireOp",EDGE,"E2.8.0.2"),sQuery(id+"F0.wireOp",EDGE,"E2.9.0.2"),sQuery(id+"F0.wireOp",EDGE,"E2.10.0.2"),sQuery(id+"F0.wireOp",EDGE,"E2.11.0.2"),sQuery(id+"F0.wireOp",EDGE,"E2.12.0.2"),sQuery(id+"F0.wireOp",EDGE,"E2.13.0.2"),sQuery(id+"F0.wireOp",EDGE,"E2.14.0.2"),sQuery(id+"F0.wireOp",EDGE,"E2.15.0.2"),sQuery(id+"F0.wireOp",EDGE,"E2.16.0.2"),sQuery(id+"F0.wireOp",EDGE,"E2.17.0.2"),sQuery(id+"F0.wireOp",EDGE,"E2.18.0.2"),sQuery(id+"F0.wireOp",EDGE,"E2.19.0.2"),sQuery(id+"F0.wireOp",EDGE,"E2.20.0.2"),sQuery(id+"F0.wireOp",EDGE,"E2.21.0.2"),sQuery(id+"F0.wireOp",EDGE,"E2.22.0.2"),sQuery(id+"F0.wireOp",EDGE,"E2.23.0.2"),sQuery(id+"F0.wireOp",EDGE,"E2.24.0.2"),sQuery(id+"F0.wireOp",EDGE,"E2.25.0.2"),sQuery(id+"F0.wireOp",EDGE,"E2.26.0.2"),sQuery(id+"F0.wireOp",EDGE,"E2.27.0.2"),sQuery(id+"F0.wireOp",EDGE,"E2.28.0.2"),sQuery(id+"F0.wireOp",EDGE,"E2.29.0.2"),sQuery(id+"F0.wireOp",EDGE,"E9.5.30.0"),sQuery(id+"F0.wireOp",EDGE,"E9.5.31.0"),sQuery(id+"F0.wireOp",EDGE,"E9.5.32.0"),sQuery(id+"F0.wireOp",EDGE,"E9.5.33.0"),sQuery(id+"F0.wireOp",EDGE,"E9.5.34.0"),sQuery(id+"F0.wireOp",EDGE,"E9.5.35.0"),sQuery(id+"F0.wireOp",EDGE,"E9.5.36.0"),sQuery(id+"F0.wireOp",EDGE,"E9.5.37.0"),sQuery(id+"F0.wireOp",EDGE,"E9.5.38.0"),sQuery(id+"F0.wireOp",EDGE,"E9.5.39.0"),sQuery(id+"F0.wireOp",EDGE,"E9.5.40.0"),sQuery(id+"F0.wireOp",EDGE,"E9.5.41.0"),sQuery(id+"F0.wireOp",EDGE,"E9.5.42.0"),sQuery(id+"F0.wireOp",EDGE,"E9.5.43.0"),sQuery(id+"F0.wireOp",EDGE,"E9.5.44.0"),sQuery(id+"F0.wireOp",EDGE,"E9.5.45.0"),sQuery(id+"F0.wireOp",EDGE,"E9.5.46.0"),sQuery(id+"F0.wireOp",EDGE,"E19.rect.top"),sQuery(id+"F0.wireOp",EDGE,"E19.rect.left"),sQuery(id+"F0.wireOp",EDGE,"E19.rect.right"),sQuery(id+"F0.wireOp",EDGE,"E22")])]}),"instanceName":"1"}),"instanceName":"1"}),"instanceName":"1"}),"instanceName":"1"}),"instanceName":"1"}),"instanceName":"1"}),"instanceName":"1"});
            transform(context, id + "F13", {"entities" : qUnion([Q0]), "transformType" : TransformType.TRANSLATION_3D, "dx" : 2.54 * mm, "dy" : 0 * mm, "dz" : 0 * mm, "makeCopy" : true});
        }
        {
            var Q0;
            Q0=makeQuery(id+"F13.opPattern","COPY",BODY,{"derivedFrom":makeQuery(id+"F12.opPattern","COPY",BODY,{"derivedFrom":makeQuery(id+"F11.opPattern","COPY",BODY,{"derivedFrom":makeQuery(id+"F10.opPattern","COPY",BODY,{"derivedFrom":makeQuery(id+"F9.opPattern","COPY",BODY,{"derivedFrom":makeQuery(id+"F8.opPattern","COPY",BODY,{"derivedFrom":makeQuery(id+"F7.opPattern","COPY",BODY,{"derivedFrom":makeQuery(id+"F5.opPattern","COPY",BODY,{"derivedFrom":makeQuery(id+"F2.opExtrude","SWEPT_BODY",BODY,{"disambiguationData":[OSD([sQuery(id+"F0.wireOp",EDGE,"E1.8.0.0"),sQuery(id+"F0.wireOp",EDGE,"E2.1.0.2"),sQuery(id+"F0.wireOp",EDGE,"E2.2.0.2"),sQuery(id+"F0.wireOp",EDGE,"E2.3.0.2"),sQuery(id+"F0.wireOp",EDGE,"E2.4.0.2"),sQuery(id+"F0.wireOp",EDGE,"E2.5.0.2"),sQuery(id+"F0.wireOp",EDGE,"E2.6.0.2"),sQuery(id+"F0.wireOp",EDGE,"E2.7.0.2"),sQuery(id+"F0.wireOp",EDGE,"E2.8.0.2"),sQuery(id+"F0.wireOp",EDGE,"E2.9.0.2"),sQuery(id+"F0.wireOp",EDGE,"E2.10.0.2"),sQuery(id+"F0.wireOp",EDGE,"E2.11.0.2"),sQuery(id+"F0.wireOp",EDGE,"E2.12.0.2"),sQuery(id+"F0.wireOp",EDGE,"E2.13.0.2"),sQuery(id+"F0.wireOp",EDGE,"E2.14.0.2"),sQuery(id+"F0.wireOp",EDGE,"E2.15.0.2"),sQuery(id+"F0.wireOp",EDGE,"E2.16.0.2"),sQuery(id+"F0.wireOp",EDGE,"E2.17.0.2"),sQuery(id+"F0.wireOp",EDGE,"E2.18.0.2"),sQuery(id+"F0.wireOp",EDGE,"E2.19.0.2"),sQuery(id+"F0.wireOp",EDGE,"E2.20.0.2"),sQuery(id+"F0.wireOp",EDGE,"E2.21.0.2"),sQuery(id+"F0.wireOp",EDGE,"E2.22.0.2"),sQuery(id+"F0.wireOp",EDGE,"E2.23.0.2"),sQuery(id+"F0.wireOp",EDGE,"E2.24.0.2"),sQuery(id+"F0.wireOp",EDGE,"E2.25.0.2"),sQuery(id+"F0.wireOp",EDGE,"E2.26.0.2"),sQuery(id+"F0.wireOp",EDGE,"E2.27.0.2"),sQuery(id+"F0.wireOp",EDGE,"E2.28.0.2"),sQuery(id+"F0.wireOp",EDGE,"E2.29.0.2"),sQuery(id+"F0.wireOp",EDGE,"E9.5.30.0"),sQuery(id+"F0.wireOp",EDGE,"E9.5.31.0"),sQuery(id+"F0.wireOp",EDGE,"E9.5.32.0"),sQuery(id+"F0.wireOp",EDGE,"E9.5.33.0"),sQuery(id+"F0.wireOp",EDGE,"E9.5.34.0"),sQuery(id+"F0.wireOp",EDGE,"E9.5.35.0"),sQuery(id+"F0.wireOp",EDGE,"E9.5.36.0"),sQuery(id+"F0.wireOp",EDGE,"E9.5.37.0"),sQuery(id+"F0.wireOp",EDGE,"E9.5.38.0"),sQuery(id+"F0.wireOp",EDGE,"E9.5.39.0"),sQuery(id+"F0.wireOp",EDGE,"E9.5.40.0"),sQuery(id+"F0.wireOp",EDGE,"E9.5.41.0"),sQuery(id+"F0.wireOp",EDGE,"E9.5.42.0"),sQuery(id+"F0.wireOp",EDGE,"E9.5.43.0"),sQuery(id+"F0.wireOp",EDGE,"E9.5.44.0"),sQuery(id+"F0.wireOp",EDGE,"E9.5.45.0"),sQuery(id+"F0.wireOp",EDGE,"E9.5.46.0"),sQuery(id+"F0.wireOp",EDGE,"E19.rect.top"),sQuery(id+"F0.wireOp",EDGE,"E19.rect.left"),sQuery(id+"F0.wireOp",EDGE,"E19.rect.right"),sQuery(id+"F0.wireOp",EDGE,"E22")])]}),"instanceName":"1"}),"instanceName":"1"}),"instanceName":"1"}),"instanceName":"1"}),"instanceName":"1"}),"instanceName":"1"}),"instanceName":"1"}),"instanceName":"1"});
            transform(context, id + "F14", {"entities" : qUnion([Q0]), "transformType" : TransformType.TRANSLATION_3D, "dx" : 2.54 * mm, "dy" : 0 * mm, "dz" : 0 * mm, "makeCopy" : true});
        }
        {
            var Q0;
            Q0=makeQuery(id+"F14.opPattern","COPY",BODY,{"derivedFrom":makeQuery(id+"F13.opPattern","COPY",BODY,{"derivedFrom":makeQuery(id+"F12.opPattern","COPY",BODY,{"derivedFrom":makeQuery(id+"F11.opPattern","COPY",BODY,{"derivedFrom":makeQuery(id+"F10.opPattern","COPY",BODY,{"derivedFrom":makeQuery(id+"F9.opPattern","COPY",BODY,{"derivedFrom":makeQuery(id+"F8.opPattern","COPY",BODY,{"derivedFrom":makeQuery(id+"F7.opPattern","COPY",BODY,{"derivedFrom":makeQuery(id+"F5.opPattern","COPY",BODY,{"derivedFrom":makeQuery(id+"F2.opExtrude","SWEPT_BODY",BODY,{"disambiguationData":[OSD([sQuery(id+"F0.wireOp",EDGE,"E1.8.0.0"),sQuery(id+"F0.wireOp",EDGE,"E2.1.0.2"),sQuery(id+"F0.wireOp",EDGE,"E2.2.0.2"),sQuery(id+"F0.wireOp",EDGE,"E2.3.0.2"),sQuery(id+"F0.wireOp",EDGE,"E2.4.0.2"),sQuery(id+"F0.wireOp",EDGE,"E2.5.0.2"),sQuery(id+"F0.wireOp",EDGE,"E2.6.0.2"),sQuery(id+"F0.wireOp",EDGE,"E2.7.0.2"),sQuery(id+"F0.wireOp",EDGE,"E2.8.0.2"),sQuery(id+"F0.wireOp",EDGE,"E2.9.0.2"),sQuery(id+"F0.wireOp",EDGE,"E2.10.0.2"),sQuery(id+"F0.wireOp",EDGE,"E2.11.0.2"),sQuery(id+"F0.wireOp",EDGE,"E2.12.0.2"),sQuery(id+"F0.wireOp",EDGE,"E2.13.0.2"),sQuery(id+"F0.wireOp",EDGE,"E2.14.0.2"),sQuery(id+"F0.wireOp",EDGE,"E2.15.0.2"),sQuery(id+"F0.wireOp",EDGE,"E2.16.0.2"),sQuery(id+"F0.wireOp",EDGE,"E2.17.0.2"),sQuery(id+"F0.wireOp",EDGE,"E2.18.0.2"),sQuery(id+"F0.wireOp",EDGE,"E2.19.0.2"),sQuery(id+"F0.wireOp",EDGE,"E2.20.0.2"),sQuery(id+"F0.wireOp",EDGE,"E2.21.0.2"),sQuery(id+"F0.wireOp",EDGE,"E2.22.0.2"),sQuery(id+"F0.wireOp",EDGE,"E2.23.0.2"),sQuery(id+"F0.wireOp",EDGE,"E2.24.0.2"),sQuery(id+"F0.wireOp",EDGE,"E2.25.0.2"),sQuery(id+"F0.wireOp",EDGE,"E2.26.0.2"),sQuery(id+"F0.wireOp",EDGE,"E2.27.0.2"),sQuery(id+"F0.wireOp",EDGE,"E2.28.0.2"),sQuery(id+"F0.wireOp",EDGE,"E2.29.0.2"),sQuery(id+"F0.wireOp",EDGE,"E9.5.30.0"),sQuery(id+"F0.wireOp",EDGE,"E9.5.31.0"),sQuery(id+"F0.wireOp",EDGE,"E9.5.32.0"),sQuery(id+"F0.wireOp",EDGE,"E9.5.33.0"),sQuery(id+"F0.wireOp",EDGE,"E9.5.34.0"),sQuery(id+"F0.wireOp",EDGE,"E9.5.35.0"),sQuery(id+"F0.wireOp",EDGE,"E9.5.36.0"),sQuery(id+"F0.wireOp",EDGE,"E9.5.37.0"),sQuery(id+"F0.wireOp",EDGE,"E9.5.38.0"),sQuery(id+"F0.wireOp",EDGE,"E9.5.39.0"),sQuery(id+"F0.wireOp",EDGE,"E9.5.40.0"),sQuery(id+"F0.wireOp",EDGE,"E9.5.41.0"),sQuery(id+"F0.wireOp",EDGE,"E9.5.42.0"),sQuery(id+"F0.wireOp",EDGE,"E9.5.43.0"),sQuery(id+"F0.wireOp",EDGE,"E9.5.44.0"),sQuery(id+"F0.wireOp",EDGE,"E9.5.45.0"),sQuery(id+"F0.wireOp",EDGE,"E9.5.46.0"),sQuery(id+"F0.wireOp",EDGE,"E19.rect.top"),sQuery(id+"F0.wireOp",EDGE,"E19.rect.left"),sQuery(id+"F0.wireOp",EDGE,"E19.rect.right"),sQuery(id+"F0.wireOp",EDGE,"E22")])]}),"instanceName":"1"}),"instanceName":"1"}),"instanceName":"1"}),"instanceName":"1"}),"instanceName":"1"}),"instanceName":"1"}),"instanceName":"1"}),"instanceName":"1"}),"instanceName":"1"});
            transform(context, id + "F15", {"entities" : qUnion([Q0]), "transformType" : TransformType.TRANSLATION_3D, "dx" : 2.54 * mm, "dy" : 0 * mm, "dz" : 0 * mm, "makeCopy" : true});
        }
        {
            var Q0;
            Q0=makeQuery(id+"F15.opPattern","COPY",BODY,{"derivedFrom":makeQuery(id+"F14.opPattern","COPY",BODY,{"derivedFrom":makeQuery(id+"F13.opPattern","COPY",BODY,{"derivedFrom":makeQuery(id+"F12.opPattern","COPY",BODY,{"derivedFrom":makeQuery(id+"F11.opPattern","COPY",BODY,{"derivedFrom":makeQuery(id+"F10.opPattern","COPY",BODY,{"derivedFrom":makeQuery(id+"F9.opPattern","COPY",BODY,{"derivedFrom":makeQuery(id+"F8.opPattern","COPY",BODY,{"derivedFrom":makeQuery(id+"F7.opPattern","COPY",BODY,{"derivedFrom":makeQuery(id+"F5.opPattern","COPY",BODY,{"derivedFrom":makeQuery(id+"F2.opExtrude","SWEPT_BODY",BODY,{"disambiguationData":[OSD([sQuery(id+"F0.wireOp",EDGE,"E1.8.0.0"),sQuery(id+"F0.wireOp",EDGE,"E2.1.0.2"),sQuery(id+"F0.wireOp",EDGE,"E2.2.0.2"),sQuery(id+"F0.wireOp",EDGE,"E2.3.0.2"),sQuery(id+"F0.wireOp",EDGE,"E2.4.0.2"),sQuery(id+"F0.wireOp",EDGE,"E2.5.0.2"),sQuery(id+"F0.wireOp",EDGE,"E2.6.0.2"),sQuery(id+"F0.wireOp",EDGE,"E2.7.0.2"),sQuery(id+"F0.wireOp",EDGE,"E2.8.0.2"),sQuery(id+"F0.wireOp",EDGE,"E2.9.0.2"),sQuery(id+"F0.wireOp",EDGE,"E2.10.0.2"),sQuery(id+"F0.wireOp",EDGE,"E2.11.0.2"),sQuery(id+"F0.wireOp",EDGE,"E2.12.0.2"),sQuery(id+"F0.wireOp",EDGE,"E2.13.0.2"),sQuery(id+"F0.wireOp",EDGE,"E2.14.0.2"),sQuery(id+"F0.wireOp",EDGE,"E2.15.0.2"),sQuery(id+"F0.wireOp",EDGE,"E2.16.0.2"),sQuery(id+"F0.wireOp",EDGE,"E2.17.0.2"),sQuery(id+"F0.wireOp",EDGE,"E2.18.0.2"),sQuery(id+"F0.wireOp",EDGE,"E2.19.0.2"),sQuery(id+"F0.wireOp",EDGE,"E2.20.0.2"),sQuery(id+"F0.wireOp",EDGE,"E2.21.0.2"),sQuery(id+"F0.wireOp",EDGE,"E2.22.0.2"),sQuery(id+"F0.wireOp",EDGE,"E2.23.0.2"),sQuery(id+"F0.wireOp",EDGE,"E2.24.0.2"),sQuery(id+"F0.wireOp",EDGE,"E2.25.0.2"),sQuery(id+"F0.wireOp",EDGE,"E2.26.0.2"),sQuery(id+"F0.wireOp",EDGE,"E2.27.0.2"),sQuery(id+"F0.wireOp",EDGE,"E2.28.0.2"),sQuery(id+"F0.wireOp",EDGE,"E2.29.0.2"),sQuery(id+"F0.wireOp",EDGE,"E9.5.30.0"),sQuery(id+"F0.wireOp",EDGE,"E9.5.31.0"),sQuery(id+"F0.wireOp",EDGE,"E9.5.32.0"),sQuery(id+"F0.wireOp",EDGE,"E9.5.33.0"),sQuery(id+"F0.wireOp",EDGE,"E9.5.34.0"),sQuery(id+"F0.wireOp",EDGE,"E9.5.35.0"),sQuery(id+"F0.wireOp",EDGE,"E9.5.36.0"),sQuery(id+"F0.wireOp",EDGE,"E9.5.37.0"),sQuery(id+"F0.wireOp",EDGE,"E9.5.38.0"),sQuery(id+"F0.wireOp",EDGE,"E9.5.39.0"),sQuery(id+"F0.wireOp",EDGE,"E9.5.40.0"),sQuery(id+"F0.wireOp",EDGE,"E9.5.41.0"),sQuery(id+"F0.wireOp",EDGE,"E9.5.42.0"),sQuery(id+"F0.wireOp",EDGE,"E9.5.43.0"),sQuery(id+"F0.wireOp",EDGE,"E9.5.44.0"),sQuery(id+"F0.wireOp",EDGE,"E9.5.45.0"),sQuery(id+"F0.wireOp",EDGE,"E9.5.46.0"),sQuery(id+"F0.wireOp",EDGE,"E19.rect.top"),sQuery(id+"F0.wireOp",EDGE,"E19.rect.left"),sQuery(id+"F0.wireOp",EDGE,"E19.rect.right"),sQuery(id+"F0.wireOp",EDGE,"E22")])]}),"instanceName":"1"}),"instanceName":"1"}),"instanceName":"1"}),"instanceName":"1"}),"instanceName":"1"}),"instanceName":"1"}),"instanceName":"1"}),"instanceName":"1"}),"instanceName":"1"}),"instanceName":"1"});
            transform(context, id + "F16", {"entities" : qUnion([Q0]), "transformType" : TransformType.TRANSLATION_3D, "dx" : 2.54 * mm, "dy" : 0 * mm, "dz" : 0 * mm, "makeCopy" : true});
        }
        {
            var Q0;
            Q0=makeQuery(id+"F16.opPattern","COPY",BODY,{"derivedFrom":makeQuery(id+"F15.opPattern","COPY",BODY,{"derivedFrom":makeQuery(id+"F14.opPattern","COPY",BODY,{"derivedFrom":makeQuery(id+"F13.opPattern","COPY",BODY,{"derivedFrom":makeQuery(id+"F12.opPattern","COPY",BODY,{"derivedFrom":makeQuery(id+"F11.opPattern","COPY",BODY,{"derivedFrom":makeQuery(id+"F10.opPattern","COPY",BODY,{"derivedFrom":makeQuery(id+"F9.opPattern","COPY",BODY,{"derivedFrom":makeQuery(id+"F8.opPattern","COPY",BODY,{"derivedFrom":makeQuery(id+"F7.opPattern","COPY",BODY,{"derivedFrom":makeQuery(id+"F5.opPattern","COPY",BODY,{"derivedFrom":makeQuery(id+"F2.opExtrude","SWEPT_BODY",BODY,{"disambiguationData":[OSD([sQuery(id+"F0.wireOp",EDGE,"E1.8.0.0"),sQuery(id+"F0.wireOp",EDGE,"E2.1.0.2"),sQuery(id+"F0.wireOp",EDGE,"E2.2.0.2"),sQuery(id+"F0.wireOp",EDGE,"E2.3.0.2"),sQuery(id+"F0.wireOp",EDGE,"E2.4.0.2"),sQuery(id+"F0.wireOp",EDGE,"E2.5.0.2"),sQuery(id+"F0.wireOp",EDGE,"E2.6.0.2"),sQuery(id+"F0.wireOp",EDGE,"E2.7.0.2"),sQuery(id+"F0.wireOp",EDGE,"E2.8.0.2"),sQuery(id+"F0.wireOp",EDGE,"E2.9.0.2"),sQuery(id+"F0.wireOp",EDGE,"E2.10.0.2"),sQuery(id+"F0.wireOp",EDGE,"E2.11.0.2"),sQuery(id+"F0.wireOp",EDGE,"E2.12.0.2"),sQuery(id+"F0.wireOp",EDGE,"E2.13.0.2"),sQuery(id+"F0.wireOp",EDGE,"E2.14.0.2"),sQuery(id+"F0.wireOp",EDGE,"E2.15.0.2"),sQuery(id+"F0.wireOp",EDGE,"E2.16.0.2"),sQuery(id+"F0.wireOp",EDGE,"E2.17.0.2"),sQuery(id+"F0.wireOp",EDGE,"E2.18.0.2"),sQuery(id+"F0.wireOp",EDGE,"E2.19.0.2"),sQuery(id+"F0.wireOp",EDGE,"E2.20.0.2"),sQuery(id+"F0.wireOp",EDGE,"E2.21.0.2"),sQuery(id+"F0.wireOp",EDGE,"E2.22.0.2"),sQuery(id+"F0.wireOp",EDGE,"E2.23.0.2"),sQuery(id+"F0.wireOp",EDGE,"E2.24.0.2"),sQuery(id+"F0.wireOp",EDGE,"E2.25.0.2"),sQuery(id+"F0.wireOp",EDGE,"E2.26.0.2"),sQuery(id+"F0.wireOp",EDGE,"E2.27.0.2"),sQuery(id+"F0.wireOp",EDGE,"E2.28.0.2"),sQuery(id+"F0.wireOp",EDGE,"E2.29.0.2"),sQuery(id+"F0.wireOp",EDGE,"E9.5.30.0"),sQuery(id+"F0.wireOp",EDGE,"E9.5.31.0"),sQuery(id+"F0.wireOp",EDGE,"E9.5.32.0"),sQuery(id+"F0.wireOp",EDGE,"E9.5.33.0"),sQuery(id+"F0.wireOp",EDGE,"E9.5.34.0"),sQuery(id+"F0.wireOp",EDGE,"E9.5.35.0"),sQuery(id+"F0.wireOp",EDGE,"E9.5.36.0"),sQuery(id+"F0.wireOp",EDGE,"E9.5.37.0"),sQuery(id+"F0.wireOp",EDGE,"E9.5.38.0"),sQuery(id+"F0.wireOp",EDGE,"E9.5.39.0"),sQuery(id+"F0.wireOp",EDGE,"E9.5.40.0"),sQuery(id+"F0.wireOp",EDGE,"E9.5.41.0"),sQuery(id+"F0.wireOp",EDGE,"E9.5.42.0"),sQuery(id+"F0.wireOp",EDGE,"E9.5.43.0"),sQuery(id+"F0.wireOp",EDGE,"E9.5.44.0"),sQuery(id+"F0.wireOp",EDGE,"E9.5.45.0"),sQuery(id+"F0.wireOp",EDGE,"E9.5.46.0"),sQuery(id+"F0.wireOp",EDGE,"E19.rect.top"),sQuery(id+"F0.wireOp",EDGE,"E19.rect.left"),sQuery(id+"F0.wireOp",EDGE,"E19.rect.right"),sQuery(id+"F0.wireOp",EDGE,"E22")])]}),"instanceName":"1"}),"instanceName":"1"}),"instanceName":"1"}),"instanceName":"1"}),"instanceName":"1"}),"instanceName":"1"}),"instanceName":"1"}),"instanceName":"1"}),"instanceName":"1"}),"instanceName":"1"}),"instanceName":"1"});
            transform(context, id + "F17", {"entities" : qUnion([Q0]), "transformType" : TransformType.TRANSLATION_3D, "dx" : 2.54 * mm, "dy" : 0 * mm, "dz" : 0 * mm, "makeCopy" : true});
        }
        {
            var Q0;
            Q0=makeQuery(id+"F17.opPattern","COPY",BODY,{"derivedFrom":makeQuery(id+"F16.opPattern","COPY",BODY,{"derivedFrom":makeQuery(id+"F15.opPattern","COPY",BODY,{"derivedFrom":makeQuery(id+"F14.opPattern","COPY",BODY,{"derivedFrom":makeQuery(id+"F13.opPattern","COPY",BODY,{"derivedFrom":makeQuery(id+"F12.opPattern","COPY",BODY,{"derivedFrom":makeQuery(id+"F11.opPattern","COPY",BODY,{"derivedFrom":makeQuery(id+"F10.opPattern","COPY",BODY,{"derivedFrom":makeQuery(id+"F9.opPattern","COPY",BODY,{"derivedFrom":makeQuery(id+"F8.opPattern","COPY",BODY,{"derivedFrom":makeQuery(id+"F7.opPattern","COPY",BODY,{"derivedFrom":makeQuery(id+"F5.opPattern","COPY",BODY,{"derivedFrom":makeQuery(id+"F2.opExtrude","SWEPT_BODY",BODY,{"disambiguationData":[OSD([sQuery(id+"F0.wireOp",EDGE,"E1.8.0.0"),sQuery(id+"F0.wireOp",EDGE,"E2.1.0.2"),sQuery(id+"F0.wireOp",EDGE,"E2.2.0.2"),sQuery(id+"F0.wireOp",EDGE,"E2.3.0.2"),sQuery(id+"F0.wireOp",EDGE,"E2.4.0.2"),sQuery(id+"F0.wireOp",EDGE,"E2.5.0.2"),sQuery(id+"F0.wireOp",EDGE,"E2.6.0.2"),sQuery(id+"F0.wireOp",EDGE,"E2.7.0.2"),sQuery(id+"F0.wireOp",EDGE,"E2.8.0.2"),sQuery(id+"F0.wireOp",EDGE,"E2.9.0.2"),sQuery(id+"F0.wireOp",EDGE,"E2.10.0.2"),sQuery(id+"F0.wireOp",EDGE,"E2.11.0.2"),sQuery(id+"F0.wireOp",EDGE,"E2.12.0.2"),sQuery(id+"F0.wireOp",EDGE,"E2.13.0.2"),sQuery(id+"F0.wireOp",EDGE,"E2.14.0.2"),sQuery(id+"F0.wireOp",EDGE,"E2.15.0.2"),sQuery(id+"F0.wireOp",EDGE,"E2.16.0.2"),sQuery(id+"F0.wireOp",EDGE,"E2.17.0.2"),sQuery(id+"F0.wireOp",EDGE,"E2.18.0.2"),sQuery(id+"F0.wireOp",EDGE,"E2.19.0.2"),sQuery(id+"F0.wireOp",EDGE,"E2.20.0.2"),sQuery(id+"F0.wireOp",EDGE,"E2.21.0.2"),sQuery(id+"F0.wireOp",EDGE,"E2.22.0.2"),sQuery(id+"F0.wireOp",EDGE,"E2.23.0.2"),sQuery(id+"F0.wireOp",EDGE,"E2.24.0.2"),sQuery(id+"F0.wireOp",EDGE,"E2.25.0.2"),sQuery(id+"F0.wireOp",EDGE,"E2.26.0.2"),sQuery(id+"F0.wireOp",EDGE,"E2.27.0.2"),sQuery(id+"F0.wireOp",EDGE,"E2.28.0.2"),sQuery(id+"F0.wireOp",EDGE,"E2.29.0.2"),sQuery(id+"F0.wireOp",EDGE,"E9.5.30.0"),sQuery(id+"F0.wireOp",EDGE,"E9.5.31.0"),sQuery(id+"F0.wireOp",EDGE,"E9.5.32.0"),sQuery(id+"F0.wireOp",EDGE,"E9.5.33.0"),sQuery(id+"F0.wireOp",EDGE,"E9.5.34.0"),sQuery(id+"F0.wireOp",EDGE,"E9.5.35.0"),sQuery(id+"F0.wireOp",EDGE,"E9.5.36.0"),sQuery(id+"F0.wireOp",EDGE,"E9.5.37.0"),sQuery(id+"F0.wireOp",EDGE,"E9.5.38.0"),sQuery(id+"F0.wireOp",EDGE,"E9.5.39.0"),sQuery(id+"F0.wireOp",EDGE,"E9.5.40.0"),sQuery(id+"F0.wireOp",EDGE,"E9.5.41.0"),sQuery(id+"F0.wireOp",EDGE,"E9.5.42.0"),sQuery(id+"F0.wireOp",EDGE,"E9.5.43.0"),sQuery(id+"F0.wireOp",EDGE,"E9.5.44.0"),sQuery(id+"F0.wireOp",EDGE,"E9.5.45.0"),sQuery(id+"F0.wireOp",EDGE,"E9.5.46.0"),sQuery(id+"F0.wireOp",EDGE,"E19.rect.top"),sQuery(id+"F0.wireOp",EDGE,"E19.rect.left"),sQuery(id+"F0.wireOp",EDGE,"E19.rect.right"),sQuery(id+"F0.wireOp",EDGE,"E22")])]}),"instanceName":"1"}),"instanceName":"1"}),"instanceName":"1"}),"instanceName":"1"}),"instanceName":"1"}),"instanceName":"1"}),"instanceName":"1"}),"instanceName":"1"}),"instanceName":"1"}),"instanceName":"1"}),"instanceName":"1"}),"instanceName":"1"});
            transform(context, id + "F18", {"entities" : qUnion([Q0]), "transformType" : TransformType.TRANSLATION_3D, "dx" : 2.44 * mm, "dy" : 0 * mm, "dz" : 0 * mm, "makeCopy" : true});
        }
        {
            var Q0;
            Q0=makeQuery(id+"F18.opPattern","COPY",BODY,{"derivedFrom":makeQuery(id+"F17.opPattern","COPY",BODY,{"derivedFrom":makeQuery(id+"F16.opPattern","COPY",BODY,{"derivedFrom":makeQuery(id+"F15.opPattern","COPY",BODY,{"derivedFrom":makeQuery(id+"F14.opPattern","COPY",BODY,{"derivedFrom":makeQuery(id+"F13.opPattern","COPY",BODY,{"derivedFrom":makeQuery(id+"F12.opPattern","COPY",BODY,{"derivedFrom":makeQuery(id+"F11.opPattern","COPY",BODY,{"derivedFrom":makeQuery(id+"F10.opPattern","COPY",BODY,{"derivedFrom":makeQuery(id+"F9.opPattern","COPY",BODY,{"derivedFrom":makeQuery(id+"F8.opPattern","COPY",BODY,{"derivedFrom":makeQuery(id+"F7.opPattern","COPY",BODY,{"derivedFrom":makeQuery(id+"F5.opPattern","COPY",BODY,{"derivedFrom":makeQuery(id+"F2.opExtrude","SWEPT_BODY",BODY,{"disambiguationData":[OSD([sQuery(id+"F0.wireOp",EDGE,"E1.8.0.0"),sQuery(id+"F0.wireOp",EDGE,"E2.1.0.2"),sQuery(id+"F0.wireOp",EDGE,"E2.2.0.2"),sQuery(id+"F0.wireOp",EDGE,"E2.3.0.2"),sQuery(id+"F0.wireOp",EDGE,"E2.4.0.2"),sQuery(id+"F0.wireOp",EDGE,"E2.5.0.2"),sQuery(id+"F0.wireOp",EDGE,"E2.6.0.2"),sQuery(id+"F0.wireOp",EDGE,"E2.7.0.2"),sQuery(id+"F0.wireOp",EDGE,"E2.8.0.2"),sQuery(id+"F0.wireOp",EDGE,"E2.9.0.2"),sQuery(id+"F0.wireOp",EDGE,"E2.10.0.2"),sQuery(id+"F0.wireOp",EDGE,"E2.11.0.2"),sQuery(id+"F0.wireOp",EDGE,"E2.12.0.2"),sQuery(id+"F0.wireOp",EDGE,"E2.13.0.2"),sQuery(id+"F0.wireOp",EDGE,"E2.14.0.2"),sQuery(id+"F0.wireOp",EDGE,"E2.15.0.2"),sQuery(id+"F0.wireOp",EDGE,"E2.16.0.2"),sQuery(id+"F0.wireOp",EDGE,"E2.17.0.2"),sQuery(id+"F0.wireOp",EDGE,"E2.18.0.2"),sQuery(id+"F0.wireOp",EDGE,"E2.19.0.2"),sQuery(id+"F0.wireOp",EDGE,"E2.20.0.2"),sQuery(id+"F0.wireOp",EDGE,"E2.21.0.2"),sQuery(id+"F0.wireOp",EDGE,"E2.22.0.2"),sQuery(id+"F0.wireOp",EDGE,"E2.23.0.2"),sQuery(id+"F0.wireOp",EDGE,"E2.24.0.2"),sQuery(id+"F0.wireOp",EDGE,"E2.25.0.2"),sQuery(id+"F0.wireOp",EDGE,"E2.26.0.2"),sQuery(id+"F0.wireOp",EDGE,"E2.27.0.2"),sQuery(id+"F0.wireOp",EDGE,"E2.28.0.2"),sQuery(id+"F0.wireOp",EDGE,"E2.29.0.2"),sQuery(id+"F0.wireOp",EDGE,"E9.5.30.0"),sQuery(id+"F0.wireOp",EDGE,"E9.5.31.0"),sQuery(id+"F0.wireOp",EDGE,"E9.5.32.0"),sQuery(id+"F0.wireOp",EDGE,"E9.5.33.0"),sQuery(id+"F0.wireOp",EDGE,"E9.5.34.0"),sQuery(id+"F0.wireOp",EDGE,"E9.5.35.0"),sQuery(id+"F0.wireOp",EDGE,"E9.5.36.0"),sQuery(id+"F0.wireOp",EDGE,"E9.5.37.0"),sQuery(id+"F0.wireOp",EDGE,"E9.5.38.0"),sQuery(id+"F0.wireOp",EDGE,"E9.5.39.0"),sQuery(id+"F0.wireOp",EDGE,"E9.5.40.0"),sQuery(id+"F0.wireOp",EDGE,"E9.5.41.0"),sQuery(id+"F0.wireOp",EDGE,"E9.5.42.0"),sQuery(id+"F0.wireOp",EDGE,"E9.5.43.0"),sQuery(id+"F0.wireOp",EDGE,"E9.5.44.0"),sQuery(id+"F0.wireOp",EDGE,"E9.5.45.0"),sQuery(id+"F0.wireOp",EDGE,"E9.5.46.0"),sQuery(id+"F0.wireOp",EDGE,"E19.rect.top"),sQuery(id+"F0.wireOp",EDGE,"E19.rect.left"),sQuery(id+"F0.wireOp",EDGE,"E19.rect.right"),sQuery(id+"F0.wireOp",EDGE,"E22")])]}),"instanceName":"1"}),"instanceName":"1"}),"instanceName":"1"}),"instanceName":"1"}),"instanceName":"1"}),"instanceName":"1"}),"instanceName":"1"}),"instanceName":"1"}),"instanceName":"1"}),"instanceName":"1"}),"instanceName":"1"}),"instanceName":"1"}),"instanceName":"1"});
            transform(context, id + "F19", {"entities" : qUnion([Q0]), "transformType" : TransformType.TRANSLATION_3D, "dx" : 2.54 * mm, "dy" : 0 * mm, "dz" : 0 * mm, "makeCopy" : true});
        }
        {
            var Q0;
            Q0=makeQuery(id+"F19.opPattern","COPY",BODY,{"derivedFrom":makeQuery(id+"F18.opPattern","COPY",BODY,{"derivedFrom":makeQuery(id+"F17.opPattern","COPY",BODY,{"derivedFrom":makeQuery(id+"F16.opPattern","COPY",BODY,{"derivedFrom":makeQuery(id+"F15.opPattern","COPY",BODY,{"derivedFrom":makeQuery(id+"F14.opPattern","COPY",BODY,{"derivedFrom":makeQuery(id+"F13.opPattern","COPY",BODY,{"derivedFrom":makeQuery(id+"F12.opPattern","COPY",BODY,{"derivedFrom":makeQuery(id+"F11.opPattern","COPY",BODY,{"derivedFrom":makeQuery(id+"F10.opPattern","COPY",BODY,{"derivedFrom":makeQuery(id+"F9.opPattern","COPY",BODY,{"derivedFrom":makeQuery(id+"F8.opPattern","COPY",BODY,{"derivedFrom":makeQuery(id+"F7.opPattern","COPY",BODY,{"derivedFrom":makeQuery(id+"F5.opPattern","COPY",BODY,{"derivedFrom":makeQuery(id+"F2.opExtrude","SWEPT_BODY",BODY,{"disambiguationData":[OSD([sQuery(id+"F0.wireOp",EDGE,"E1.8.0.0"),sQuery(id+"F0.wireOp",EDGE,"E2.1.0.2"),sQuery(id+"F0.wireOp",EDGE,"E2.2.0.2"),sQuery(id+"F0.wireOp",EDGE,"E2.3.0.2"),sQuery(id+"F0.wireOp",EDGE,"E2.4.0.2"),sQuery(id+"F0.wireOp",EDGE,"E2.5.0.2"),sQuery(id+"F0.wireOp",EDGE,"E2.6.0.2"),sQuery(id+"F0.wireOp",EDGE,"E2.7.0.2"),sQuery(id+"F0.wireOp",EDGE,"E2.8.0.2"),sQuery(id+"F0.wireOp",EDGE,"E2.9.0.2"),sQuery(id+"F0.wireOp",EDGE,"E2.10.0.2"),sQuery(id+"F0.wireOp",EDGE,"E2.11.0.2"),sQuery(id+"F0.wireOp",EDGE,"E2.12.0.2"),sQuery(id+"F0.wireOp",EDGE,"E2.13.0.2"),sQuery(id+"F0.wireOp",EDGE,"E2.14.0.2"),sQuery(id+"F0.wireOp",EDGE,"E2.15.0.2"),sQuery(id+"F0.wireOp",EDGE,"E2.16.0.2"),sQuery(id+"F0.wireOp",EDGE,"E2.17.0.2"),sQuery(id+"F0.wireOp",EDGE,"E2.18.0.2"),sQuery(id+"F0.wireOp",EDGE,"E2.19.0.2"),sQuery(id+"F0.wireOp",EDGE,"E2.20.0.2"),sQuery(id+"F0.wireOp",EDGE,"E2.21.0.2"),sQuery(id+"F0.wireOp",EDGE,"E2.22.0.2"),sQuery(id+"F0.wireOp",EDGE,"E2.23.0.2"),sQuery(id+"F0.wireOp",EDGE,"E2.24.0.2"),sQuery(id+"F0.wireOp",EDGE,"E2.25.0.2"),sQuery(id+"F0.wireOp",EDGE,"E2.26.0.2"),sQuery(id+"F0.wireOp",EDGE,"E2.27.0.2"),sQuery(id+"F0.wireOp",EDGE,"E2.28.0.2"),sQuery(id+"F0.wireOp",EDGE,"E2.29.0.2"),sQuery(id+"F0.wireOp",EDGE,"E9.5.30.0"),sQuery(id+"F0.wireOp",EDGE,"E9.5.31.0"),sQuery(id+"F0.wireOp",EDGE,"E9.5.32.0"),sQuery(id+"F0.wireOp",EDGE,"E9.5.33.0"),sQuery(id+"F0.wireOp",EDGE,"E9.5.34.0"),sQuery(id+"F0.wireOp",EDGE,"E9.5.35.0"),sQuery(id+"F0.wireOp",EDGE,"E9.5.36.0"),sQuery(id+"F0.wireOp",EDGE,"E9.5.37.0"),sQuery(id+"F0.wireOp",EDGE,"E9.5.38.0"),sQuery(id+"F0.wireOp",EDGE,"E9.5.39.0"),sQuery(id+"F0.wireOp",EDGE,"E9.5.40.0"),sQuery(id+"F0.wireOp",EDGE,"E9.5.41.0"),sQuery(id+"F0.wireOp",EDGE,"E9.5.42.0"),sQuery(id+"F0.wireOp",EDGE,"E9.5.43.0"),sQuery(id+"F0.wireOp",EDGE,"E9.5.44.0"),sQuery(id+"F0.wireOp",EDGE,"E9.5.45.0"),sQuery(id+"F0.wireOp",EDGE,"E9.5.46.0"),sQuery(id+"F0.wireOp",EDGE,"E19.rect.top"),sQuery(id+"F0.wireOp",EDGE,"E19.rect.left"),sQuery(id+"F0.wireOp",EDGE,"E19.rect.right"),sQuery(id+"F0.wireOp",EDGE,"E22")])]}),"instanceName":"1"}),"instanceName":"1"}),"instanceName":"1"}),"instanceName":"1"}),"instanceName":"1"}),"instanceName":"1"}),"instanceName":"1"}),"instanceName":"1"}),"instanceName":"1"}),"instanceName":"1"}),"instanceName":"1"}),"instanceName":"1"}),"instanceName":"1"}),"instanceName":"1"});
            transform(context, id + "F20", {"entities" : qUnion([Q0]), "transformType" : TransformType.TRANSLATION_3D, "dx" : 2.54 * mm, "dy" : 0 * mm, "dz" : 0 * mm, "makeCopy" : true});
        }
        {
            var Q0;
            Q0=makeQuery(id+"F20.opPattern","COPY",BODY,{"derivedFrom":makeQuery(id+"F19.opPattern","COPY",BODY,{"derivedFrom":makeQuery(id+"F18.opPattern","COPY",BODY,{"derivedFrom":makeQuery(id+"F17.opPattern","COPY",BODY,{"derivedFrom":makeQuery(id+"F16.opPattern","COPY",BODY,{"derivedFrom":makeQuery(id+"F15.opPattern","COPY",BODY,{"derivedFrom":makeQuery(id+"F14.opPattern","COPY",BODY,{"derivedFrom":makeQuery(id+"F13.opPattern","COPY",BODY,{"derivedFrom":makeQuery(id+"F12.opPattern","COPY",BODY,{"derivedFrom":makeQuery(id+"F11.opPattern","COPY",BODY,{"derivedFrom":makeQuery(id+"F10.opPattern","COPY",BODY,{"derivedFrom":makeQuery(id+"F9.opPattern","COPY",BODY,{"derivedFrom":makeQuery(id+"F8.opPattern","COPY",BODY,{"derivedFrom":makeQuery(id+"F7.opPattern","COPY",BODY,{"derivedFrom":makeQuery(id+"F5.opPattern","COPY",BODY,{"derivedFrom":makeQuery(id+"F2.opExtrude","SWEPT_BODY",BODY,{"disambiguationData":[OSD([sQuery(id+"F0.wireOp",EDGE,"E1.8.0.0"),sQuery(id+"F0.wireOp",EDGE,"E2.1.0.2"),sQuery(id+"F0.wireOp",EDGE,"E2.2.0.2"),sQuery(id+"F0.wireOp",EDGE,"E2.3.0.2"),sQuery(id+"F0.wireOp",EDGE,"E2.4.0.2"),sQuery(id+"F0.wireOp",EDGE,"E2.5.0.2"),sQuery(id+"F0.wireOp",EDGE,"E2.6.0.2"),sQuery(id+"F0.wireOp",EDGE,"E2.7.0.2"),sQuery(id+"F0.wireOp",EDGE,"E2.8.0.2"),sQuery(id+"F0.wireOp",EDGE,"E2.9.0.2"),sQuery(id+"F0.wireOp",EDGE,"E2.10.0.2"),sQuery(id+"F0.wireOp",EDGE,"E2.11.0.2"),sQuery(id+"F0.wireOp",EDGE,"E2.12.0.2"),sQuery(id+"F0.wireOp",EDGE,"E2.13.0.2"),sQuery(id+"F0.wireOp",EDGE,"E2.14.0.2"),sQuery(id+"F0.wireOp",EDGE,"E2.15.0.2"),sQuery(id+"F0.wireOp",EDGE,"E2.16.0.2"),sQuery(id+"F0.wireOp",EDGE,"E2.17.0.2"),sQuery(id+"F0.wireOp",EDGE,"E2.18.0.2"),sQuery(id+"F0.wireOp",EDGE,"E2.19.0.2"),sQuery(id+"F0.wireOp",EDGE,"E2.20.0.2"),sQuery(id+"F0.wireOp",EDGE,"E2.21.0.2"),sQuery(id+"F0.wireOp",EDGE,"E2.22.0.2"),sQuery(id+"F0.wireOp",EDGE,"E2.23.0.2"),sQuery(id+"F0.wireOp",EDGE,"E2.24.0.2"),sQuery(id+"F0.wireOp",EDGE,"E2.25.0.2"),sQuery(id+"F0.wireOp",EDGE,"E2.26.0.2"),sQuery(id+"F0.wireOp",EDGE,"E2.27.0.2"),sQuery(id+"F0.wireOp",EDGE,"E2.28.0.2"),sQuery(id+"F0.wireOp",EDGE,"E2.29.0.2"),sQuery(id+"F0.wireOp",EDGE,"E9.5.30.0"),sQuery(id+"F0.wireOp",EDGE,"E9.5.31.0"),sQuery(id+"F0.wireOp",EDGE,"E9.5.32.0"),sQuery(id+"F0.wireOp",EDGE,"E9.5.33.0"),sQuery(id+"F0.wireOp",EDGE,"E9.5.34.0"),sQuery(id+"F0.wireOp",EDGE,"E9.5.35.0"),sQuery(id+"F0.wireOp",EDGE,"E9.5.36.0"),sQuery(id+"F0.wireOp",EDGE,"E9.5.37.0"),sQuery(id+"F0.wireOp",EDGE,"E9.5.38.0"),sQuery(id+"F0.wireOp",EDGE,"E9.5.39.0"),sQuery(id+"F0.wireOp",EDGE,"E9.5.40.0"),sQuery(id+"F0.wireOp",EDGE,"E9.5.41.0"),sQuery(id+"F0.wireOp",EDGE,"E9.5.42.0"),sQuery(id+"F0.wireOp",EDGE,"E9.5.43.0"),sQuery(id+"F0.wireOp",EDGE,"E9.5.44.0"),sQuery(id+"F0.wireOp",EDGE,"E9.5.45.0"),sQuery(id+"F0.wireOp",EDGE,"E9.5.46.0"),sQuery(id+"F0.wireOp",EDGE,"E19.rect.top"),sQuery(id+"F0.wireOp",EDGE,"E19.rect.left"),sQuery(id+"F0.wireOp",EDGE,"E19.rect.right"),sQuery(id+"F0.wireOp",EDGE,"E22")])]}),"instanceName":"1"}),"instanceName":"1"}),"instanceName":"1"}),"instanceName":"1"}),"instanceName":"1"}),"instanceName":"1"}),"instanceName":"1"}),"instanceName":"1"}),"instanceName":"1"}),"instanceName":"1"}),"instanceName":"1"}),"instanceName":"1"}),"instanceName":"1"}),"instanceName":"1"}),"instanceName":"1"});
            transform(context, id + "F21", {"entities" : qUnion([Q0]), "transformType" : TransformType.TRANSLATION_3D, "dx" : 2.54 * mm, "dy" : 0 * mm, "dz" : 0 * mm, "makeCopy" : true});
        }
        {
            var Q0;
            Q0=makeQuery(id+"F21.opPattern","COPY",BODY,{"derivedFrom":makeQuery(id+"F20.opPattern","COPY",BODY,{"derivedFrom":makeQuery(id+"F19.opPattern","COPY",BODY,{"derivedFrom":makeQuery(id+"F18.opPattern","COPY",BODY,{"derivedFrom":makeQuery(id+"F17.opPattern","COPY",BODY,{"derivedFrom":makeQuery(id+"F16.opPattern","COPY",BODY,{"derivedFrom":makeQuery(id+"F15.opPattern","COPY",BODY,{"derivedFrom":makeQuery(id+"F14.opPattern","COPY",BODY,{"derivedFrom":makeQuery(id+"F13.opPattern","COPY",BODY,{"derivedFrom":makeQuery(id+"F12.opPattern","COPY",BODY,{"derivedFrom":makeQuery(id+"F11.opPattern","COPY",BODY,{"derivedFrom":makeQuery(id+"F10.opPattern","COPY",BODY,{"derivedFrom":makeQuery(id+"F9.opPattern","COPY",BODY,{"derivedFrom":makeQuery(id+"F8.opPattern","COPY",BODY,{"derivedFrom":makeQuery(id+"F7.opPattern","COPY",BODY,{"derivedFrom":makeQuery(id+"F5.opPattern","COPY",BODY,{"derivedFrom":makeQuery(id+"F2.opExtrude","SWEPT_BODY",BODY,{"disambiguationData":[OSD([sQuery(id+"F0.wireOp",EDGE,"E1.8.0.0"),sQuery(id+"F0.wireOp",EDGE,"E2.1.0.2"),sQuery(id+"F0.wireOp",EDGE,"E2.2.0.2"),sQuery(id+"F0.wireOp",EDGE,"E2.3.0.2"),sQuery(id+"F0.wireOp",EDGE,"E2.4.0.2"),sQuery(id+"F0.wireOp",EDGE,"E2.5.0.2"),sQuery(id+"F0.wireOp",EDGE,"E2.6.0.2"),sQuery(id+"F0.wireOp",EDGE,"E2.7.0.2"),sQuery(id+"F0.wireOp",EDGE,"E2.8.0.2"),sQuery(id+"F0.wireOp",EDGE,"E2.9.0.2"),sQuery(id+"F0.wireOp",EDGE,"E2.10.0.2"),sQuery(id+"F0.wireOp",EDGE,"E2.11.0.2"),sQuery(id+"F0.wireOp",EDGE,"E2.12.0.2"),sQuery(id+"F0.wireOp",EDGE,"E2.13.0.2"),sQuery(id+"F0.wireOp",EDGE,"E2.14.0.2"),sQuery(id+"F0.wireOp",EDGE,"E2.15.0.2"),sQuery(id+"F0.wireOp",EDGE,"E2.16.0.2"),sQuery(id+"F0.wireOp",EDGE,"E2.17.0.2"),sQuery(id+"F0.wireOp",EDGE,"E2.18.0.2"),sQuery(id+"F0.wireOp",EDGE,"E2.19.0.2"),sQuery(id+"F0.wireOp",EDGE,"E2.20.0.2"),sQuery(id+"F0.wireOp",EDGE,"E2.21.0.2"),sQuery(id+"F0.wireOp",EDGE,"E2.22.0.2"),sQuery(id+"F0.wireOp",EDGE,"E2.23.0.2"),sQuery(id+"F0.wireOp",EDGE,"E2.24.0.2"),sQuery(id+"F0.wireOp",EDGE,"E2.25.0.2"),sQuery(id+"F0.wireOp",EDGE,"E2.26.0.2"),sQuery(id+"F0.wireOp",EDGE,"E2.27.0.2"),sQuery(id+"F0.wireOp",EDGE,"E2.28.0.2"),sQuery(id+"F0.wireOp",EDGE,"E2.29.0.2"),sQuery(id+"F0.wireOp",EDGE,"E9.5.30.0"),sQuery(id+"F0.wireOp",EDGE,"E9.5.31.0"),sQuery(id+"F0.wireOp",EDGE,"E9.5.32.0"),sQuery(id+"F0.wireOp",EDGE,"E9.5.33.0"),sQuery(id+"F0.wireOp",EDGE,"E9.5.34.0"),sQuery(id+"F0.wireOp",EDGE,"E9.5.35.0"),sQuery(id+"F0.wireOp",EDGE,"E9.5.36.0"),sQuery(id+"F0.wireOp",EDGE,"E9.5.37.0"),sQuery(id+"F0.wireOp",EDGE,"E9.5.38.0"),sQuery(id+"F0.wireOp",EDGE,"E9.5.39.0"),sQuery(id+"F0.wireOp",EDGE,"E9.5.40.0"),sQuery(id+"F0.wireOp",EDGE,"E9.5.41.0"),sQuery(id+"F0.wireOp",EDGE,"E9.5.42.0"),sQuery(id+"F0.wireOp",EDGE,"E9.5.43.0"),sQuery(id+"F0.wireOp",EDGE,"E9.5.44.0"),sQuery(id+"F0.wireOp",EDGE,"E9.5.45.0"),sQuery(id+"F0.wireOp",EDGE,"E9.5.46.0"),sQuery(id+"F0.wireOp",EDGE,"E19.rect.top"),sQuery(id+"F0.wireOp",EDGE,"E19.rect.left"),sQuery(id+"F0.wireOp",EDGE,"E19.rect.right"),sQuery(id+"F0.wireOp",EDGE,"E22")])]}),"instanceName":"1"}),"instanceName":"1"}),"instanceName":"1"}),"instanceName":"1"}),"instanceName":"1"}),"instanceName":"1"}),"instanceName":"1"}),"instanceName":"1"}),"instanceName":"1"}),"instanceName":"1"}),"instanceName":"1"}),"instanceName":"1"}),"instanceName":"1"}),"instanceName":"1"}),"instanceName":"1"}),"instanceName":"1"});
            transform(context, id + "F22", {"entities" : qUnion([Q0]), "transformType" : TransformType.TRANSLATION_3D, "dx" : 2.54 * mm, "dy" : 0 * mm, "dz" : 0 * mm, "makeCopy" : true});
        }
        {
            var Q0;
            Q0=makeQuery(id+"F22.opPattern","COPY",BODY,{"derivedFrom":makeQuery(id+"F21.opPattern","COPY",BODY,{"derivedFrom":makeQuery(id+"F20.opPattern","COPY",BODY,{"derivedFrom":makeQuery(id+"F19.opPattern","COPY",BODY,{"derivedFrom":makeQuery(id+"F18.opPattern","COPY",BODY,{"derivedFrom":makeQuery(id+"F17.opPattern","COPY",BODY,{"derivedFrom":makeQuery(id+"F16.opPattern","COPY",BODY,{"derivedFrom":makeQuery(id+"F15.opPattern","COPY",BODY,{"derivedFrom":makeQuery(id+"F14.opPattern","COPY",BODY,{"derivedFrom":makeQuery(id+"F13.opPattern","COPY",BODY,{"derivedFrom":makeQuery(id+"F12.opPattern","COPY",BODY,{"derivedFrom":makeQuery(id+"F11.opPattern","COPY",BODY,{"derivedFrom":makeQuery(id+"F10.opPattern","COPY",BODY,{"derivedFrom":makeQuery(id+"F9.opPattern","COPY",BODY,{"derivedFrom":makeQuery(id+"F8.opPattern","COPY",BODY,{"derivedFrom":makeQuery(id+"F7.opPattern","COPY",BODY,{"derivedFrom":makeQuery(id+"F5.opPattern","COPY",BODY,{"derivedFrom":makeQuery(id+"F2.opExtrude","SWEPT_BODY",BODY,{"disambiguationData":[OSD([sQuery(id+"F0.wireOp",EDGE,"E1.8.0.0"),sQuery(id+"F0.wireOp",EDGE,"E2.1.0.2"),sQuery(id+"F0.wireOp",EDGE,"E2.2.0.2"),sQuery(id+"F0.wireOp",EDGE,"E2.3.0.2"),sQuery(id+"F0.wireOp",EDGE,"E2.4.0.2"),sQuery(id+"F0.wireOp",EDGE,"E2.5.0.2"),sQuery(id+"F0.wireOp",EDGE,"E2.6.0.2"),sQuery(id+"F0.wireOp",EDGE,"E2.7.0.2"),sQuery(id+"F0.wireOp",EDGE,"E2.8.0.2"),sQuery(id+"F0.wireOp",EDGE,"E2.9.0.2"),sQuery(id+"F0.wireOp",EDGE,"E2.10.0.2"),sQuery(id+"F0.wireOp",EDGE,"E2.11.0.2"),sQuery(id+"F0.wireOp",EDGE,"E2.12.0.2"),sQuery(id+"F0.wireOp",EDGE,"E2.13.0.2"),sQuery(id+"F0.wireOp",EDGE,"E2.14.0.2"),sQuery(id+"F0.wireOp",EDGE,"E2.15.0.2"),sQuery(id+"F0.wireOp",EDGE,"E2.16.0.2"),sQuery(id+"F0.wireOp",EDGE,"E2.17.0.2"),sQuery(id+"F0.wireOp",EDGE,"E2.18.0.2"),sQuery(id+"F0.wireOp",EDGE,"E2.19.0.2"),sQuery(id+"F0.wireOp",EDGE,"E2.20.0.2"),sQuery(id+"F0.wireOp",EDGE,"E2.21.0.2"),sQuery(id+"F0.wireOp",EDGE,"E2.22.0.2"),sQuery(id+"F0.wireOp",EDGE,"E2.23.0.2"),sQuery(id+"F0.wireOp",EDGE,"E2.24.0.2"),sQuery(id+"F0.wireOp",EDGE,"E2.25.0.2"),sQuery(id+"F0.wireOp",EDGE,"E2.26.0.2"),sQuery(id+"F0.wireOp",EDGE,"E2.27.0.2"),sQuery(id+"F0.wireOp",EDGE,"E2.28.0.2"),sQuery(id+"F0.wireOp",EDGE,"E2.29.0.2"),sQuery(id+"F0.wireOp",EDGE,"E9.5.30.0"),sQuery(id+"F0.wireOp",EDGE,"E9.5.31.0"),sQuery(id+"F0.wireOp",EDGE,"E9.5.32.0"),sQuery(id+"F0.wireOp",EDGE,"E9.5.33.0"),sQuery(id+"F0.wireOp",EDGE,"E9.5.34.0"),sQuery(id+"F0.wireOp",EDGE,"E9.5.35.0"),sQuery(id+"F0.wireOp",EDGE,"E9.5.36.0"),sQuery(id+"F0.wireOp",EDGE,"E9.5.37.0"),sQuery(id+"F0.wireOp",EDGE,"E9.5.38.0"),sQuery(id+"F0.wireOp",EDGE,"E9.5.39.0"),sQuery(id+"F0.wireOp",EDGE,"E9.5.40.0"),sQuery(id+"F0.wireOp",EDGE,"E9.5.41.0"),sQuery(id+"F0.wireOp",EDGE,"E9.5.42.0"),sQuery(id+"F0.wireOp",EDGE,"E9.5.43.0"),sQuery(id+"F0.wireOp",EDGE,"E9.5.44.0"),sQuery(id+"F0.wireOp",EDGE,"E9.5.45.0"),sQuery(id+"F0.wireOp",EDGE,"E9.5.46.0"),sQuery(id+"F0.wireOp",EDGE,"E19.rect.top"),sQuery(id+"F0.wireOp",EDGE,"E19.rect.left"),sQuery(id+"F0.wireOp",EDGE,"E19.rect.right"),sQuery(id+"F0.wireOp",EDGE,"E22")])]}),"instanceName":"1"}),"instanceName":"1"}),"instanceName":"1"}),"instanceName":"1"}),"instanceName":"1"}),"instanceName":"1"}),"instanceName":"1"}),"instanceName":"1"}),"instanceName":"1"}),"instanceName":"1"}),"instanceName":"1"}),"instanceName":"1"}),"instanceName":"1"}),"instanceName":"1"}),"instanceName":"1"}),"instanceName":"1"}),"instanceName":"1"});
            transform(context, id + "F23", {"entities" : qUnion([Q0]), "transformType" : TransformType.TRANSLATION_3D, "dx" : 2.54 * mm, "dy" : 0 * mm, "dz" : 0 * mm, "makeCopy" : true});
        }
        {
            var Q0;
            Q0=makeQuery(id+"F23.opPattern","COPY",BODY,{"derivedFrom":makeQuery(id+"F22.opPattern","COPY",BODY,{"derivedFrom":makeQuery(id+"F21.opPattern","COPY",BODY,{"derivedFrom":makeQuery(id+"F20.opPattern","COPY",BODY,{"derivedFrom":makeQuery(id+"F19.opPattern","COPY",BODY,{"derivedFrom":makeQuery(id+"F18.opPattern","COPY",BODY,{"derivedFrom":makeQuery(id+"F17.opPattern","COPY",BODY,{"derivedFrom":makeQuery(id+"F16.opPattern","COPY",BODY,{"derivedFrom":makeQuery(id+"F15.opPattern","COPY",BODY,{"derivedFrom":makeQuery(id+"F14.opPattern","COPY",BODY,{"derivedFrom":makeQuery(id+"F13.opPattern","COPY",BODY,{"derivedFrom":makeQuery(id+"F12.opPattern","COPY",BODY,{"derivedFrom":makeQuery(id+"F11.opPattern","COPY",BODY,{"derivedFrom":makeQuery(id+"F10.opPattern","COPY",BODY,{"derivedFrom":makeQuery(id+"F9.opPattern","COPY",BODY,{"derivedFrom":makeQuery(id+"F8.opPattern","COPY",BODY,{"derivedFrom":makeQuery(id+"F7.opPattern","COPY",BODY,{"derivedFrom":makeQuery(id+"F5.opPattern","COPY",BODY,{"derivedFrom":makeQuery(id+"F2.opExtrude","SWEPT_BODY",BODY,{"disambiguationData":[OSD([sQuery(id+"F0.wireOp",EDGE,"E1.8.0.0"),sQuery(id+"F0.wireOp",EDGE,"E2.1.0.2"),sQuery(id+"F0.wireOp",EDGE,"E2.2.0.2"),sQuery(id+"F0.wireOp",EDGE,"E2.3.0.2"),sQuery(id+"F0.wireOp",EDGE,"E2.4.0.2"),sQuery(id+"F0.wireOp",EDGE,"E2.5.0.2"),sQuery(id+"F0.wireOp",EDGE,"E2.6.0.2"),sQuery(id+"F0.wireOp",EDGE,"E2.7.0.2"),sQuery(id+"F0.wireOp",EDGE,"E2.8.0.2"),sQuery(id+"F0.wireOp",EDGE,"E2.9.0.2"),sQuery(id+"F0.wireOp",EDGE,"E2.10.0.2"),sQuery(id+"F0.wireOp",EDGE,"E2.11.0.2"),sQuery(id+"F0.wireOp",EDGE,"E2.12.0.2"),sQuery(id+"F0.wireOp",EDGE,"E2.13.0.2"),sQuery(id+"F0.wireOp",EDGE,"E2.14.0.2"),sQuery(id+"F0.wireOp",EDGE,"E2.15.0.2"),sQuery(id+"F0.wireOp",EDGE,"E2.16.0.2"),sQuery(id+"F0.wireOp",EDGE,"E2.17.0.2"),sQuery(id+"F0.wireOp",EDGE,"E2.18.0.2"),sQuery(id+"F0.wireOp",EDGE,"E2.19.0.2"),sQuery(id+"F0.wireOp",EDGE,"E2.20.0.2"),sQuery(id+"F0.wireOp",EDGE,"E2.21.0.2"),sQuery(id+"F0.wireOp",EDGE,"E2.22.0.2"),sQuery(id+"F0.wireOp",EDGE,"E2.23.0.2"),sQuery(id+"F0.wireOp",EDGE,"E2.24.0.2"),sQuery(id+"F0.wireOp",EDGE,"E2.25.0.2"),sQuery(id+"F0.wireOp",EDGE,"E2.26.0.2"),sQuery(id+"F0.wireOp",EDGE,"E2.27.0.2"),sQuery(id+"F0.wireOp",EDGE,"E2.28.0.2"),sQuery(id+"F0.wireOp",EDGE,"E2.29.0.2"),sQuery(id+"F0.wireOp",EDGE,"E9.5.30.0"),sQuery(id+"F0.wireOp",EDGE,"E9.5.31.0"),sQuery(id+"F0.wireOp",EDGE,"E9.5.32.0"),sQuery(id+"F0.wireOp",EDGE,"E9.5.33.0"),sQuery(id+"F0.wireOp",EDGE,"E9.5.34.0"),sQuery(id+"F0.wireOp",EDGE,"E9.5.35.0"),sQuery(id+"F0.wireOp",EDGE,"E9.5.36.0"),sQuery(id+"F0.wireOp",EDGE,"E9.5.37.0"),sQuery(id+"F0.wireOp",EDGE,"E9.5.38.0"),sQuery(id+"F0.wireOp",EDGE,"E9.5.39.0"),sQuery(id+"F0.wireOp",EDGE,"E9.5.40.0"),sQuery(id+"F0.wireOp",EDGE,"E9.5.41.0"),sQuery(id+"F0.wireOp",EDGE,"E9.5.42.0"),sQuery(id+"F0.wireOp",EDGE,"E9.5.43.0"),sQuery(id+"F0.wireOp",EDGE,"E9.5.44.0"),sQuery(id+"F0.wireOp",EDGE,"E9.5.45.0"),sQuery(id+"F0.wireOp",EDGE,"E9.5.46.0"),sQuery(id+"F0.wireOp",EDGE,"E19.rect.top"),sQuery(id+"F0.wireOp",EDGE,"E19.rect.left"),sQuery(id+"F0.wireOp",EDGE,"E19.rect.right"),sQuery(id+"F0.wireOp",EDGE,"E22")])]}),"instanceName":"1"}),"instanceName":"1"}),"instanceName":"1"}),"instanceName":"1"}),"instanceName":"1"}),"instanceName":"1"}),"instanceName":"1"}),"instanceName":"1"}),"instanceName":"1"}),"instanceName":"1"}),"instanceName":"1"}),"instanceName":"1"}),"instanceName":"1"}),"instanceName":"1"}),"instanceName":"1"}),"instanceName":"1"}),"instanceName":"1"}),"instanceName":"1"});
            transform(context, id + "F24", {"entities" : qUnion([Q0]), "transformType" : TransformType.TRANSLATION_3D, "dx" : 2.54 * mm, "dy" : 0 * mm, "dz" : 0 * mm, "makeCopy" : true});
        }
        {
            var Q0;
            Q0=makeQuery(id+"F24.opPattern","COPY",BODY,{"derivedFrom":makeQuery(id+"F23.opPattern","COPY",BODY,{"derivedFrom":makeQuery(id+"F22.opPattern","COPY",BODY,{"derivedFrom":makeQuery(id+"F21.opPattern","COPY",BODY,{"derivedFrom":makeQuery(id+"F20.opPattern","COPY",BODY,{"derivedFrom":makeQuery(id+"F19.opPattern","COPY",BODY,{"derivedFrom":makeQuery(id+"F18.opPattern","COPY",BODY,{"derivedFrom":makeQuery(id+"F17.opPattern","COPY",BODY,{"derivedFrom":makeQuery(id+"F16.opPattern","COPY",BODY,{"derivedFrom":makeQuery(id+"F15.opPattern","COPY",BODY,{"derivedFrom":makeQuery(id+"F14.opPattern","COPY",BODY,{"derivedFrom":makeQuery(id+"F13.opPattern","COPY",BODY,{"derivedFrom":makeQuery(id+"F12.opPattern","COPY",BODY,{"derivedFrom":makeQuery(id+"F11.opPattern","COPY",BODY,{"derivedFrom":makeQuery(id+"F10.opPattern","COPY",BODY,{"derivedFrom":makeQuery(id+"F9.opPattern","COPY",BODY,{"derivedFrom":makeQuery(id+"F8.opPattern","COPY",BODY,{"derivedFrom":makeQuery(id+"F7.opPattern","COPY",BODY,{"derivedFrom":makeQuery(id+"F5.opPattern","COPY",BODY,{"derivedFrom":makeQuery(id+"F2.opExtrude","SWEPT_BODY",BODY,{"disambiguationData":[OSD([sQuery(id+"F0.wireOp",EDGE,"E1.8.0.0"),sQuery(id+"F0.wireOp",EDGE,"E2.1.0.2"),sQuery(id+"F0.wireOp",EDGE,"E2.2.0.2"),sQuery(id+"F0.wireOp",EDGE,"E2.3.0.2"),sQuery(id+"F0.wireOp",EDGE,"E2.4.0.2"),sQuery(id+"F0.wireOp",EDGE,"E2.5.0.2"),sQuery(id+"F0.wireOp",EDGE,"E2.6.0.2"),sQuery(id+"F0.wireOp",EDGE,"E2.7.0.2"),sQuery(id+"F0.wireOp",EDGE,"E2.8.0.2"),sQuery(id+"F0.wireOp",EDGE,"E2.9.0.2"),sQuery(id+"F0.wireOp",EDGE,"E2.10.0.2"),sQuery(id+"F0.wireOp",EDGE,"E2.11.0.2"),sQuery(id+"F0.wireOp",EDGE,"E2.12.0.2"),sQuery(id+"F0.wireOp",EDGE,"E2.13.0.2"),sQuery(id+"F0.wireOp",EDGE,"E2.14.0.2"),sQuery(id+"F0.wireOp",EDGE,"E2.15.0.2"),sQuery(id+"F0.wireOp",EDGE,"E2.16.0.2"),sQuery(id+"F0.wireOp",EDGE,"E2.17.0.2"),sQuery(id+"F0.wireOp",EDGE,"E2.18.0.2"),sQuery(id+"F0.wireOp",EDGE,"E2.19.0.2"),sQuery(id+"F0.wireOp",EDGE,"E2.20.0.2"),sQuery(id+"F0.wireOp",EDGE,"E2.21.0.2"),sQuery(id+"F0.wireOp",EDGE,"E2.22.0.2"),sQuery(id+"F0.wireOp",EDGE,"E2.23.0.2"),sQuery(id+"F0.wireOp",EDGE,"E2.24.0.2"),sQuery(id+"F0.wireOp",EDGE,"E2.25.0.2"),sQuery(id+"F0.wireOp",EDGE,"E2.26.0.2"),sQuery(id+"F0.wireOp",EDGE,"E2.27.0.2"),sQuery(id+"F0.wireOp",EDGE,"E2.28.0.2"),sQuery(id+"F0.wireOp",EDGE,"E2.29.0.2"),sQuery(id+"F0.wireOp",EDGE,"E9.5.30.0"),sQuery(id+"F0.wireOp",EDGE,"E9.5.31.0"),sQuery(id+"F0.wireOp",EDGE,"E9.5.32.0"),sQuery(id+"F0.wireOp",EDGE,"E9.5.33.0"),sQuery(id+"F0.wireOp",EDGE,"E9.5.34.0"),sQuery(id+"F0.wireOp",EDGE,"E9.5.35.0"),sQuery(id+"F0.wireOp",EDGE,"E9.5.36.0"),sQuery(id+"F0.wireOp",EDGE,"E9.5.37.0"),sQuery(id+"F0.wireOp",EDGE,"E9.5.38.0"),sQuery(id+"F0.wireOp",EDGE,"E9.5.39.0"),sQuery(id+"F0.wireOp",EDGE,"E9.5.40.0"),sQuery(id+"F0.wireOp",EDGE,"E9.5.41.0"),sQuery(id+"F0.wireOp",EDGE,"E9.5.42.0"),sQuery(id+"F0.wireOp",EDGE,"E9.5.43.0"),sQuery(id+"F0.wireOp",EDGE,"E9.5.44.0"),sQuery(id+"F0.wireOp",EDGE,"E9.5.45.0"),sQuery(id+"F0.wireOp",EDGE,"E9.5.46.0"),sQuery(id+"F0.wireOp",EDGE,"E19.rect.top"),sQuery(id+"F0.wireOp",EDGE,"E19.rect.left"),sQuery(id+"F0.wireOp",EDGE,"E19.rect.right"),sQuery(id+"F0.wireOp",EDGE,"E22")])]}),"instanceName":"1"}),"instanceName":"1"}),"instanceName":"1"}),"instanceName":"1"}),"instanceName":"1"}),"instanceName":"1"}),"instanceName":"1"}),"instanceName":"1"}),"instanceName":"1"}),"instanceName":"1"}),"instanceName":"1"}),"instanceName":"1"}),"instanceName":"1"}),"instanceName":"1"}),"instanceName":"1"}),"instanceName":"1"}),"instanceName":"1"}),"instanceName":"1"}),"instanceName":"1"});
            transform(context, id + "F25", {"entities" : qUnion([Q0]), "transformType" : TransformType.TRANSLATION_3D, "dx" : 2.54 * mm, "dy" : 0 * mm, "dz" : 0 * mm, "makeCopy" : true});
        }
        {
            var Q0;
            Q0=makeQuery(id+"F25.opPattern","COPY",BODY,{"derivedFrom":makeQuery(id+"F24.opPattern","COPY",BODY,{"derivedFrom":makeQuery(id+"F23.opPattern","COPY",BODY,{"derivedFrom":makeQuery(id+"F22.opPattern","COPY",BODY,{"derivedFrom":makeQuery(id+"F21.opPattern","COPY",BODY,{"derivedFrom":makeQuery(id+"F20.opPattern","COPY",BODY,{"derivedFrom":makeQuery(id+"F19.opPattern","COPY",BODY,{"derivedFrom":makeQuery(id+"F18.opPattern","COPY",BODY,{"derivedFrom":makeQuery(id+"F17.opPattern","COPY",BODY,{"derivedFrom":makeQuery(id+"F16.opPattern","COPY",BODY,{"derivedFrom":makeQuery(id+"F15.opPattern","COPY",BODY,{"derivedFrom":makeQuery(id+"F14.opPattern","COPY",BODY,{"derivedFrom":makeQuery(id+"F13.opPattern","COPY",BODY,{"derivedFrom":makeQuery(id+"F12.opPattern","COPY",BODY,{"derivedFrom":makeQuery(id+"F11.opPattern","COPY",BODY,{"derivedFrom":makeQuery(id+"F10.opPattern","COPY",BODY,{"derivedFrom":makeQuery(id+"F9.opPattern","COPY",BODY,{"derivedFrom":makeQuery(id+"F8.opPattern","COPY",BODY,{"derivedFrom":makeQuery(id+"F7.opPattern","COPY",BODY,{"derivedFrom":makeQuery(id+"F5.opPattern","COPY",BODY,{"derivedFrom":makeQuery(id+"F2.opExtrude","SWEPT_BODY",BODY,{"disambiguationData":[OSD([sQuery(id+"F0.wireOp",EDGE,"E1.8.0.0"),sQuery(id+"F0.wireOp",EDGE,"E2.1.0.2"),sQuery(id+"F0.wireOp",EDGE,"E2.2.0.2"),sQuery(id+"F0.wireOp",EDGE,"E2.3.0.2"),sQuery(id+"F0.wireOp",EDGE,"E2.4.0.2"),sQuery(id+"F0.wireOp",EDGE,"E2.5.0.2"),sQuery(id+"F0.wireOp",EDGE,"E2.6.0.2"),sQuery(id+"F0.wireOp",EDGE,"E2.7.0.2"),sQuery(id+"F0.wireOp",EDGE,"E2.8.0.2"),sQuery(id+"F0.wireOp",EDGE,"E2.9.0.2"),sQuery(id+"F0.wireOp",EDGE,"E2.10.0.2"),sQuery(id+"F0.wireOp",EDGE,"E2.11.0.2"),sQuery(id+"F0.wireOp",EDGE,"E2.12.0.2"),sQuery(id+"F0.wireOp",EDGE,"E2.13.0.2"),sQuery(id+"F0.wireOp",EDGE,"E2.14.0.2"),sQuery(id+"F0.wireOp",EDGE,"E2.15.0.2"),sQuery(id+"F0.wireOp",EDGE,"E2.16.0.2"),sQuery(id+"F0.wireOp",EDGE,"E2.17.0.2"),sQuery(id+"F0.wireOp",EDGE,"E2.18.0.2"),sQuery(id+"F0.wireOp",EDGE,"E2.19.0.2"),sQuery(id+"F0.wireOp",EDGE,"E2.20.0.2"),sQuery(id+"F0.wireOp",EDGE,"E2.21.0.2"),sQuery(id+"F0.wireOp",EDGE,"E2.22.0.2"),sQuery(id+"F0.wireOp",EDGE,"E2.23.0.2"),sQuery(id+"F0.wireOp",EDGE,"E2.24.0.2"),sQuery(id+"F0.wireOp",EDGE,"E2.25.0.2"),sQuery(id+"F0.wireOp",EDGE,"E2.26.0.2"),sQuery(id+"F0.wireOp",EDGE,"E2.27.0.2"),sQuery(id+"F0.wireOp",EDGE,"E2.28.0.2"),sQuery(id+"F0.wireOp",EDGE,"E2.29.0.2"),sQuery(id+"F0.wireOp",EDGE,"E9.5.30.0"),sQuery(id+"F0.wireOp",EDGE,"E9.5.31.0"),sQuery(id+"F0.wireOp",EDGE,"E9.5.32.0"),sQuery(id+"F0.wireOp",EDGE,"E9.5.33.0"),sQuery(id+"F0.wireOp",EDGE,"E9.5.34.0"),sQuery(id+"F0.wireOp",EDGE,"E9.5.35.0"),sQuery(id+"F0.wireOp",EDGE,"E9.5.36.0"),sQuery(id+"F0.wireOp",EDGE,"E9.5.37.0"),sQuery(id+"F0.wireOp",EDGE,"E9.5.38.0"),sQuery(id+"F0.wireOp",EDGE,"E9.5.39.0"),sQuery(id+"F0.wireOp",EDGE,"E9.5.40.0"),sQuery(id+"F0.wireOp",EDGE,"E9.5.41.0"),sQuery(id+"F0.wireOp",EDGE,"E9.5.42.0"),sQuery(id+"F0.wireOp",EDGE,"E9.5.43.0"),sQuery(id+"F0.wireOp",EDGE,"E9.5.44.0"),sQuery(id+"F0.wireOp",EDGE,"E9.5.45.0"),sQuery(id+"F0.wireOp",EDGE,"E9.5.46.0"),sQuery(id+"F0.wireOp",EDGE,"E19.rect.top"),sQuery(id+"F0.wireOp",EDGE,"E19.rect.left"),sQuery(id+"F0.wireOp",EDGE,"E19.rect.right"),sQuery(id+"F0.wireOp",EDGE,"E22")])]}),"instanceName":"1"}),"instanceName":"1"}),"instanceName":"1"}),"instanceName":"1"}),"instanceName":"1"}),"instanceName":"1"}),"instanceName":"1"}),"instanceName":"1"}),"instanceName":"1"}),"instanceName":"1"}),"instanceName":"1"}),"instanceName":"1"}),"instanceName":"1"}),"instanceName":"1"}),"instanceName":"1"}),"instanceName":"1"}),"instanceName":"1"}),"instanceName":"1"}),"instanceName":"1"}),"instanceName":"1"});
            transform(context, id + "F26", {"entities" : qUnion([Q0]), "transformType" : TransformType.TRANSLATION_3D, "dx" : 2.54 * mm, "dy" : 0 * mm, "dz" : 0 * mm, "makeCopy" : true});
        }
        {
            var Q0;
            Q0=makeQuery(id+"F26.opPattern","COPY",BODY,{"derivedFrom":makeQuery(id+"F25.opPattern","COPY",BODY,{"derivedFrom":makeQuery(id+"F24.opPattern","COPY",BODY,{"derivedFrom":makeQuery(id+"F23.opPattern","COPY",BODY,{"derivedFrom":makeQuery(id+"F22.opPattern","COPY",BODY,{"derivedFrom":makeQuery(id+"F21.opPattern","COPY",BODY,{"derivedFrom":makeQuery(id+"F20.opPattern","COPY",BODY,{"derivedFrom":makeQuery(id+"F19.opPattern","COPY",BODY,{"derivedFrom":makeQuery(id+"F18.opPattern","COPY",BODY,{"derivedFrom":makeQuery(id+"F17.opPattern","COPY",BODY,{"derivedFrom":makeQuery(id+"F16.opPattern","COPY",BODY,{"derivedFrom":makeQuery(id+"F15.opPattern","COPY",BODY,{"derivedFrom":makeQuery(id+"F14.opPattern","COPY",BODY,{"derivedFrom":makeQuery(id+"F13.opPattern","COPY",BODY,{"derivedFrom":makeQuery(id+"F12.opPattern","COPY",BODY,{"derivedFrom":makeQuery(id+"F11.opPattern","COPY",BODY,{"derivedFrom":makeQuery(id+"F10.opPattern","COPY",BODY,{"derivedFrom":makeQuery(id+"F9.opPattern","COPY",BODY,{"derivedFrom":makeQuery(id+"F8.opPattern","COPY",BODY,{"derivedFrom":makeQuery(id+"F7.opPattern","COPY",BODY,{"derivedFrom":makeQuery(id+"F5.opPattern","COPY",BODY,{"derivedFrom":makeQuery(id+"F2.opExtrude","SWEPT_BODY",BODY,{"disambiguationData":[OSD([sQuery(id+"F0.wireOp",EDGE,"E1.8.0.0"),sQuery(id+"F0.wireOp",EDGE,"E2.1.0.2"),sQuery(id+"F0.wireOp",EDGE,"E2.2.0.2"),sQuery(id+"F0.wireOp",EDGE,"E2.3.0.2"),sQuery(id+"F0.wireOp",EDGE,"E2.4.0.2"),sQuery(id+"F0.wireOp",EDGE,"E2.5.0.2"),sQuery(id+"F0.wireOp",EDGE,"E2.6.0.2"),sQuery(id+"F0.wireOp",EDGE,"E2.7.0.2"),sQuery(id+"F0.wireOp",EDGE,"E2.8.0.2"),sQuery(id+"F0.wireOp",EDGE,"E2.9.0.2"),sQuery(id+"F0.wireOp",EDGE,"E2.10.0.2"),sQuery(id+"F0.wireOp",EDGE,"E2.11.0.2"),sQuery(id+"F0.wireOp",EDGE,"E2.12.0.2"),sQuery(id+"F0.wireOp",EDGE,"E2.13.0.2"),sQuery(id+"F0.wireOp",EDGE,"E2.14.0.2"),sQuery(id+"F0.wireOp",EDGE,"E2.15.0.2"),sQuery(id+"F0.wireOp",EDGE,"E2.16.0.2"),sQuery(id+"F0.wireOp",EDGE,"E2.17.0.2"),sQuery(id+"F0.wireOp",EDGE,"E2.18.0.2"),sQuery(id+"F0.wireOp",EDGE,"E2.19.0.2"),sQuery(id+"F0.wireOp",EDGE,"E2.20.0.2"),sQuery(id+"F0.wireOp",EDGE,"E2.21.0.2"),sQuery(id+"F0.wireOp",EDGE,"E2.22.0.2"),sQuery(id+"F0.wireOp",EDGE,"E2.23.0.2"),sQuery(id+"F0.wireOp",EDGE,"E2.24.0.2"),sQuery(id+"F0.wireOp",EDGE,"E2.25.0.2"),sQuery(id+"F0.wireOp",EDGE,"E2.26.0.2"),sQuery(id+"F0.wireOp",EDGE,"E2.27.0.2"),sQuery(id+"F0.wireOp",EDGE,"E2.28.0.2"),sQuery(id+"F0.wireOp",EDGE,"E2.29.0.2"),sQuery(id+"F0.wireOp",EDGE,"E9.5.30.0"),sQuery(id+"F0.wireOp",EDGE,"E9.5.31.0"),sQuery(id+"F0.wireOp",EDGE,"E9.5.32.0"),sQuery(id+"F0.wireOp",EDGE,"E9.5.33.0"),sQuery(id+"F0.wireOp",EDGE,"E9.5.34.0"),sQuery(id+"F0.wireOp",EDGE,"E9.5.35.0"),sQuery(id+"F0.wireOp",EDGE,"E9.5.36.0"),sQuery(id+"F0.wireOp",EDGE,"E9.5.37.0"),sQuery(id+"F0.wireOp",EDGE,"E9.5.38.0"),sQuery(id+"F0.wireOp",EDGE,"E9.5.39.0"),sQuery(id+"F0.wireOp",EDGE,"E9.5.40.0"),sQuery(id+"F0.wireOp",EDGE,"E9.5.41.0"),sQuery(id+"F0.wireOp",EDGE,"E9.5.42.0"),sQuery(id+"F0.wireOp",EDGE,"E9.5.43.0"),sQuery(id+"F0.wireOp",EDGE,"E9.5.44.0"),sQuery(id+"F0.wireOp",EDGE,"E9.5.45.0"),sQuery(id+"F0.wireOp",EDGE,"E9.5.46.0"),sQuery(id+"F0.wireOp",EDGE,"E19.rect.top"),sQuery(id+"F0.wireOp",EDGE,"E19.rect.left"),sQuery(id+"F0.wireOp",EDGE,"E19.rect.right"),sQuery(id+"F0.wireOp",EDGE,"E22")])]}),"instanceName":"1"}),"instanceName":"1"}),"instanceName":"1"}),"instanceName":"1"}),"instanceName":"1"}),"instanceName":"1"}),"instanceName":"1"}),"instanceName":"1"}),"instanceName":"1"}),"instanceName":"1"}),"instanceName":"1"}),"instanceName":"1"}),"instanceName":"1"}),"instanceName":"1"}),"instanceName":"1"}),"instanceName":"1"}),"instanceName":"1"}),"instanceName":"1"}),"instanceName":"1"}),"instanceName":"1"}),"instanceName":"1"});
            transform(context, id + "F27", {"entities" : qUnion([Q0]), "transformType" : TransformType.TRANSLATION_3D, "dx" : 2.54 * mm, "dy" : 0 * mm, "dz" : 0 * mm, "makeCopy" : true});
        }
        {
            var Q0;
            Q0=makeQuery(id+"F27.opPattern","COPY",BODY,{"derivedFrom":makeQuery(id+"F26.opPattern","COPY",BODY,{"derivedFrom":makeQuery(id+"F25.opPattern","COPY",BODY,{"derivedFrom":makeQuery(id+"F24.opPattern","COPY",BODY,{"derivedFrom":makeQuery(id+"F23.opPattern","COPY",BODY,{"derivedFrom":makeQuery(id+"F22.opPattern","COPY",BODY,{"derivedFrom":makeQuery(id+"F21.opPattern","COPY",BODY,{"derivedFrom":makeQuery(id+"F20.opPattern","COPY",BODY,{"derivedFrom":makeQuery(id+"F19.opPattern","COPY",BODY,{"derivedFrom":makeQuery(id+"F18.opPattern","COPY",BODY,{"derivedFrom":makeQuery(id+"F17.opPattern","COPY",BODY,{"derivedFrom":makeQuery(id+"F16.opPattern","COPY",BODY,{"derivedFrom":makeQuery(id+"F15.opPattern","COPY",BODY,{"derivedFrom":makeQuery(id+"F14.opPattern","COPY",BODY,{"derivedFrom":makeQuery(id+"F13.opPattern","COPY",BODY,{"derivedFrom":makeQuery(id+"F12.opPattern","COPY",BODY,{"derivedFrom":makeQuery(id+"F11.opPattern","COPY",BODY,{"derivedFrom":makeQuery(id+"F10.opPattern","COPY",BODY,{"derivedFrom":makeQuery(id+"F9.opPattern","COPY",BODY,{"derivedFrom":makeQuery(id+"F8.opPattern","COPY",BODY,{"derivedFrom":makeQuery(id+"F7.opPattern","COPY",BODY,{"derivedFrom":makeQuery(id+"F5.opPattern","COPY",BODY,{"derivedFrom":makeQuery(id+"F2.opExtrude","SWEPT_BODY",BODY,{"disambiguationData":[OSD([sQuery(id+"F0.wireOp",EDGE,"E1.8.0.0"),sQuery(id+"F0.wireOp",EDGE,"E2.1.0.2"),sQuery(id+"F0.wireOp",EDGE,"E2.2.0.2"),sQuery(id+"F0.wireOp",EDGE,"E2.3.0.2"),sQuery(id+"F0.wireOp",EDGE,"E2.4.0.2"),sQuery(id+"F0.wireOp",EDGE,"E2.5.0.2"),sQuery(id+"F0.wireOp",EDGE,"E2.6.0.2"),sQuery(id+"F0.wireOp",EDGE,"E2.7.0.2"),sQuery(id+"F0.wireOp",EDGE,"E2.8.0.2"),sQuery(id+"F0.wireOp",EDGE,"E2.9.0.2"),sQuery(id+"F0.wireOp",EDGE,"E2.10.0.2"),sQuery(id+"F0.wireOp",EDGE,"E2.11.0.2"),sQuery(id+"F0.wireOp",EDGE,"E2.12.0.2"),sQuery(id+"F0.wireOp",EDGE,"E2.13.0.2"),sQuery(id+"F0.wireOp",EDGE,"E2.14.0.2"),sQuery(id+"F0.wireOp",EDGE,"E2.15.0.2"),sQuery(id+"F0.wireOp",EDGE,"E2.16.0.2"),sQuery(id+"F0.wireOp",EDGE,"E2.17.0.2"),sQuery(id+"F0.wireOp",EDGE,"E2.18.0.2"),sQuery(id+"F0.wireOp",EDGE,"E2.19.0.2"),sQuery(id+"F0.wireOp",EDGE,"E2.20.0.2"),sQuery(id+"F0.wireOp",EDGE,"E2.21.0.2"),sQuery(id+"F0.wireOp",EDGE,"E2.22.0.2"),sQuery(id+"F0.wireOp",EDGE,"E2.23.0.2"),sQuery(id+"F0.wireOp",EDGE,"E2.24.0.2"),sQuery(id+"F0.wireOp",EDGE,"E2.25.0.2"),sQuery(id+"F0.wireOp",EDGE,"E2.26.0.2"),sQuery(id+"F0.wireOp",EDGE,"E2.27.0.2"),sQuery(id+"F0.wireOp",EDGE,"E2.28.0.2"),sQuery(id+"F0.wireOp",EDGE,"E2.29.0.2"),sQuery(id+"F0.wireOp",EDGE,"E9.5.30.0"),sQuery(id+"F0.wireOp",EDGE,"E9.5.31.0"),sQuery(id+"F0.wireOp",EDGE,"E9.5.32.0"),sQuery(id+"F0.wireOp",EDGE,"E9.5.33.0"),sQuery(id+"F0.wireOp",EDGE,"E9.5.34.0"),sQuery(id+"F0.wireOp",EDGE,"E9.5.35.0"),sQuery(id+"F0.wireOp",EDGE,"E9.5.36.0"),sQuery(id+"F0.wireOp",EDGE,"E9.5.37.0"),sQuery(id+"F0.wireOp",EDGE,"E9.5.38.0"),sQuery(id+"F0.wireOp",EDGE,"E9.5.39.0"),sQuery(id+"F0.wireOp",EDGE,"E9.5.40.0"),sQuery(id+"F0.wireOp",EDGE,"E9.5.41.0"),sQuery(id+"F0.wireOp",EDGE,"E9.5.42.0"),sQuery(id+"F0.wireOp",EDGE,"E9.5.43.0"),sQuery(id+"F0.wireOp",EDGE,"E9.5.44.0"),sQuery(id+"F0.wireOp",EDGE,"E9.5.45.0"),sQuery(id+"F0.wireOp",EDGE,"E9.5.46.0"),sQuery(id+"F0.wireOp",EDGE,"E19.rect.top"),sQuery(id+"F0.wireOp",EDGE,"E19.rect.left"),sQuery(id+"F0.wireOp",EDGE,"E19.rect.right"),sQuery(id+"F0.wireOp",EDGE,"E22")])]}),"instanceName":"1"}),"instanceName":"1"}),"instanceName":"1"}),"instanceName":"1"}),"instanceName":"1"}),"instanceName":"1"}),"instanceName":"1"}),"instanceName":"1"}),"instanceName":"1"}),"instanceName":"1"}),"instanceName":"1"}),"instanceName":"1"}),"instanceName":"1"}),"instanceName":"1"}),"instanceName":"1"}),"instanceName":"1"}),"instanceName":"1"}),"instanceName":"1"}),"instanceName":"1"}),"instanceName":"1"}),"instanceName":"1"}),"instanceName":"1"});
            transform(context, id + "F28", {"entities" : qUnion([Q0]), "transformType" : TransformType.TRANSLATION_3D, "dx" : 2.54 * mm, "dy" : 0 * mm, "dz" : 0 * mm, "makeCopy" : true});
        }
        {
            var Q0;
            Q0=makeQuery(id+"F28.opPattern","COPY",BODY,{"derivedFrom":makeQuery(id+"F27.opPattern","COPY",BODY,{"derivedFrom":makeQuery(id+"F26.opPattern","COPY",BODY,{"derivedFrom":makeQuery(id+"F25.opPattern","COPY",BODY,{"derivedFrom":makeQuery(id+"F24.opPattern","COPY",BODY,{"derivedFrom":makeQuery(id+"F23.opPattern","COPY",BODY,{"derivedFrom":makeQuery(id+"F22.opPattern","COPY",BODY,{"derivedFrom":makeQuery(id+"F21.opPattern","COPY",BODY,{"derivedFrom":makeQuery(id+"F20.opPattern","COPY",BODY,{"derivedFrom":makeQuery(id+"F19.opPattern","COPY",BODY,{"derivedFrom":makeQuery(id+"F18.opPattern","COPY",BODY,{"derivedFrom":makeQuery(id+"F17.opPattern","COPY",BODY,{"derivedFrom":makeQuery(id+"F16.opPattern","COPY",BODY,{"derivedFrom":makeQuery(id+"F15.opPattern","COPY",BODY,{"derivedFrom":makeQuery(id+"F14.opPattern","COPY",BODY,{"derivedFrom":makeQuery(id+"F13.opPattern","COPY",BODY,{"derivedFrom":makeQuery(id+"F12.opPattern","COPY",BODY,{"derivedFrom":makeQuery(id+"F11.opPattern","COPY",BODY,{"derivedFrom":makeQuery(id+"F10.opPattern","COPY",BODY,{"derivedFrom":makeQuery(id+"F9.opPattern","COPY",BODY,{"derivedFrom":makeQuery(id+"F8.opPattern","COPY",BODY,{"derivedFrom":makeQuery(id+"F7.opPattern","COPY",BODY,{"derivedFrom":makeQuery(id+"F5.opPattern","COPY",BODY,{"derivedFrom":makeQuery(id+"F2.opExtrude","SWEPT_BODY",BODY,{"disambiguationData":[OSD([sQuery(id+"F0.wireOp",EDGE,"E1.8.0.0"),sQuery(id+"F0.wireOp",EDGE,"E2.1.0.2"),sQuery(id+"F0.wireOp",EDGE,"E2.2.0.2"),sQuery(id+"F0.wireOp",EDGE,"E2.3.0.2"),sQuery(id+"F0.wireOp",EDGE,"E2.4.0.2"),sQuery(id+"F0.wireOp",EDGE,"E2.5.0.2"),sQuery(id+"F0.wireOp",EDGE,"E2.6.0.2"),sQuery(id+"F0.wireOp",EDGE,"E2.7.0.2"),sQuery(id+"F0.wireOp",EDGE,"E2.8.0.2"),sQuery(id+"F0.wireOp",EDGE,"E2.9.0.2"),sQuery(id+"F0.wireOp",EDGE,"E2.10.0.2"),sQuery(id+"F0.wireOp",EDGE,"E2.11.0.2"),sQuery(id+"F0.wireOp",EDGE,"E2.12.0.2"),sQuery(id+"F0.wireOp",EDGE,"E2.13.0.2"),sQuery(id+"F0.wireOp",EDGE,"E2.14.0.2"),sQuery(id+"F0.wireOp",EDGE,"E2.15.0.2"),sQuery(id+"F0.wireOp",EDGE,"E2.16.0.2"),sQuery(id+"F0.wireOp",EDGE,"E2.17.0.2"),sQuery(id+"F0.wireOp",EDGE,"E2.18.0.2"),sQuery(id+"F0.wireOp",EDGE,"E2.19.0.2"),sQuery(id+"F0.wireOp",EDGE,"E2.20.0.2"),sQuery(id+"F0.wireOp",EDGE,"E2.21.0.2"),sQuery(id+"F0.wireOp",EDGE,"E2.22.0.2"),sQuery(id+"F0.wireOp",EDGE,"E2.23.0.2"),sQuery(id+"F0.wireOp",EDGE,"E2.24.0.2"),sQuery(id+"F0.wireOp",EDGE,"E2.25.0.2"),sQuery(id+"F0.wireOp",EDGE,"E2.26.0.2"),sQuery(id+"F0.wireOp",EDGE,"E2.27.0.2"),sQuery(id+"F0.wireOp",EDGE,"E2.28.0.2"),sQuery(id+"F0.wireOp",EDGE,"E2.29.0.2"),sQuery(id+"F0.wireOp",EDGE,"E9.5.30.0"),sQuery(id+"F0.wireOp",EDGE,"E9.5.31.0"),sQuery(id+"F0.wireOp",EDGE,"E9.5.32.0"),sQuery(id+"F0.wireOp",EDGE,"E9.5.33.0"),sQuery(id+"F0.wireOp",EDGE,"E9.5.34.0"),sQuery(id+"F0.wireOp",EDGE,"E9.5.35.0"),sQuery(id+"F0.wireOp",EDGE,"E9.5.36.0"),sQuery(id+"F0.wireOp",EDGE,"E9.5.37.0"),sQuery(id+"F0.wireOp",EDGE,"E9.5.38.0"),sQuery(id+"F0.wireOp",EDGE,"E9.5.39.0"),sQuery(id+"F0.wireOp",EDGE,"E9.5.40.0"),sQuery(id+"F0.wireOp",EDGE,"E9.5.41.0"),sQuery(id+"F0.wireOp",EDGE,"E9.5.42.0"),sQuery(id+"F0.wireOp",EDGE,"E9.5.43.0"),sQuery(id+"F0.wireOp",EDGE,"E9.5.44.0"),sQuery(id+"F0.wireOp",EDGE,"E9.5.45.0"),sQuery(id+"F0.wireOp",EDGE,"E9.5.46.0"),sQuery(id+"F0.wireOp",EDGE,"E19.rect.top"),sQuery(id+"F0.wireOp",EDGE,"E19.rect.left"),sQuery(id+"F0.wireOp",EDGE,"E19.rect.right"),sQuery(id+"F0.wireOp",EDGE,"E22")])]}),"instanceName":"1"}),"instanceName":"1"}),"instanceName":"1"}),"instanceName":"1"}),"instanceName":"1"}),"instanceName":"1"}),"instanceName":"1"}),"instanceName":"1"}),"instanceName":"1"}),"instanceName":"1"}),"instanceName":"1"}),"instanceName":"1"}),"instanceName":"1"}),"instanceName":"1"}),"instanceName":"1"}),"instanceName":"1"}),"instanceName":"1"}),"instanceName":"1"}),"instanceName":"1"}),"instanceName":"1"}),"instanceName":"1"}),"instanceName":"1"}),"instanceName":"1"});
            transform(context, id + "F29", {"entities" : qUnion([Q0]), "transformType" : TransformType.TRANSLATION_3D, "dx" : 2.54 * mm, "dy" : 0 * mm, "dz" : 0 * mm, "makeCopy" : true});
        }
        {
            var Q0;
            Q0=makeQuery(id+"F29.opPattern","COPY",BODY,{"derivedFrom":makeQuery(id+"F28.opPattern","COPY",BODY,{"derivedFrom":makeQuery(id+"F27.opPattern","COPY",BODY,{"derivedFrom":makeQuery(id+"F26.opPattern","COPY",BODY,{"derivedFrom":makeQuery(id+"F25.opPattern","COPY",BODY,{"derivedFrom":makeQuery(id+"F24.opPattern","COPY",BODY,{"derivedFrom":makeQuery(id+"F23.opPattern","COPY",BODY,{"derivedFrom":makeQuery(id+"F22.opPattern","COPY",BODY,{"derivedFrom":makeQuery(id+"F21.opPattern","COPY",BODY,{"derivedFrom":makeQuery(id+"F20.opPattern","COPY",BODY,{"derivedFrom":makeQuery(id+"F19.opPattern","COPY",BODY,{"derivedFrom":makeQuery(id+"F18.opPattern","COPY",BODY,{"derivedFrom":makeQuery(id+"F17.opPattern","COPY",BODY,{"derivedFrom":makeQuery(id+"F16.opPattern","COPY",BODY,{"derivedFrom":makeQuery(id+"F15.opPattern","COPY",BODY,{"derivedFrom":makeQuery(id+"F14.opPattern","COPY",BODY,{"derivedFrom":makeQuery(id+"F13.opPattern","COPY",BODY,{"derivedFrom":makeQuery(id+"F12.opPattern","COPY",BODY,{"derivedFrom":makeQuery(id+"F11.opPattern","COPY",BODY,{"derivedFrom":makeQuery(id+"F10.opPattern","COPY",BODY,{"derivedFrom":makeQuery(id+"F9.opPattern","COPY",BODY,{"derivedFrom":makeQuery(id+"F8.opPattern","COPY",BODY,{"derivedFrom":makeQuery(id+"F7.opPattern","COPY",BODY,{"derivedFrom":makeQuery(id+"F5.opPattern","COPY",BODY,{"derivedFrom":makeQuery(id+"F2.opExtrude","SWEPT_BODY",BODY,{"disambiguationData":[OSD([sQuery(id+"F0.wireOp",EDGE,"E1.8.0.0"),sQuery(id+"F0.wireOp",EDGE,"E2.1.0.2"),sQuery(id+"F0.wireOp",EDGE,"E2.2.0.2"),sQuery(id+"F0.wireOp",EDGE,"E2.3.0.2"),sQuery(id+"F0.wireOp",EDGE,"E2.4.0.2"),sQuery(id+"F0.wireOp",EDGE,"E2.5.0.2"),sQuery(id+"F0.wireOp",EDGE,"E2.6.0.2"),sQuery(id+"F0.wireOp",EDGE,"E2.7.0.2"),sQuery(id+"F0.wireOp",EDGE,"E2.8.0.2"),sQuery(id+"F0.wireOp",EDGE,"E2.9.0.2"),sQuery(id+"F0.wireOp",EDGE,"E2.10.0.2"),sQuery(id+"F0.wireOp",EDGE,"E2.11.0.2"),sQuery(id+"F0.wireOp",EDGE,"E2.12.0.2"),sQuery(id+"F0.wireOp",EDGE,"E2.13.0.2"),sQuery(id+"F0.wireOp",EDGE,"E2.14.0.2"),sQuery(id+"F0.wireOp",EDGE,"E2.15.0.2"),sQuery(id+"F0.wireOp",EDGE,"E2.16.0.2"),sQuery(id+"F0.wireOp",EDGE,"E2.17.0.2"),sQuery(id+"F0.wireOp",EDGE,"E2.18.0.2"),sQuery(id+"F0.wireOp",EDGE,"E2.19.0.2"),sQuery(id+"F0.wireOp",EDGE,"E2.20.0.2"),sQuery(id+"F0.wireOp",EDGE,"E2.21.0.2"),sQuery(id+"F0.wireOp",EDGE,"E2.22.0.2"),sQuery(id+"F0.wireOp",EDGE,"E2.23.0.2"),sQuery(id+"F0.wireOp",EDGE,"E2.24.0.2"),sQuery(id+"F0.wireOp",EDGE,"E2.25.0.2"),sQuery(id+"F0.wireOp",EDGE,"E2.26.0.2"),sQuery(id+"F0.wireOp",EDGE,"E2.27.0.2"),sQuery(id+"F0.wireOp",EDGE,"E2.28.0.2"),sQuery(id+"F0.wireOp",EDGE,"E2.29.0.2"),sQuery(id+"F0.wireOp",EDGE,"E9.5.30.0"),sQuery(id+"F0.wireOp",EDGE,"E9.5.31.0"),sQuery(id+"F0.wireOp",EDGE,"E9.5.32.0"),sQuery(id+"F0.wireOp",EDGE,"E9.5.33.0"),sQuery(id+"F0.wireOp",EDGE,"E9.5.34.0"),sQuery(id+"F0.wireOp",EDGE,"E9.5.35.0"),sQuery(id+"F0.wireOp",EDGE,"E9.5.36.0"),sQuery(id+"F0.wireOp",EDGE,"E9.5.37.0"),sQuery(id+"F0.wireOp",EDGE,"E9.5.38.0"),sQuery(id+"F0.wireOp",EDGE,"E9.5.39.0"),sQuery(id+"F0.wireOp",EDGE,"E9.5.40.0"),sQuery(id+"F0.wireOp",EDGE,"E9.5.41.0"),sQuery(id+"F0.wireOp",EDGE,"E9.5.42.0"),sQuery(id+"F0.wireOp",EDGE,"E9.5.43.0"),sQuery(id+"F0.wireOp",EDGE,"E9.5.44.0"),sQuery(id+"F0.wireOp",EDGE,"E9.5.45.0"),sQuery(id+"F0.wireOp",EDGE,"E9.5.46.0"),sQuery(id+"F0.wireOp",EDGE,"E19.rect.top"),sQuery(id+"F0.wireOp",EDGE,"E19.rect.left"),sQuery(id+"F0.wireOp",EDGE,"E19.rect.right"),sQuery(id+"F0.wireOp",EDGE,"E22")])]}),"instanceName":"1"}),"instanceName":"1"}),"instanceName":"1"}),"instanceName":"1"}),"instanceName":"1"}),"instanceName":"1"}),"instanceName":"1"}),"instanceName":"1"}),"instanceName":"1"}),"instanceName":"1"}),"instanceName":"1"}),"instanceName":"1"}),"instanceName":"1"}),"instanceName":"1"}),"instanceName":"1"}),"instanceName":"1"}),"instanceName":"1"}),"instanceName":"1"}),"instanceName":"1"}),"instanceName":"1"}),"instanceName":"1"}),"instanceName":"1"}),"instanceName":"1"}),"instanceName":"1"});
            transform(context, id + "F30", {"entities" : qUnion([Q0]), "transformType" : TransformType.TRANSLATION_3D, "dx" : 2.54 * mm, "dy" : 0 * mm, "dz" : 0 * mm, "makeCopy" : true});
        }
        {
            var Q0;
            Q0=makeQuery(id+"F30.opPattern","COPY",BODY,{"derivedFrom":makeQuery(id+"F29.opPattern","COPY",BODY,{"derivedFrom":makeQuery(id+"F28.opPattern","COPY",BODY,{"derivedFrom":makeQuery(id+"F27.opPattern","COPY",BODY,{"derivedFrom":makeQuery(id+"F26.opPattern","COPY",BODY,{"derivedFrom":makeQuery(id+"F25.opPattern","COPY",BODY,{"derivedFrom":makeQuery(id+"F24.opPattern","COPY",BODY,{"derivedFrom":makeQuery(id+"F23.opPattern","COPY",BODY,{"derivedFrom":makeQuery(id+"F22.opPattern","COPY",BODY,{"derivedFrom":makeQuery(id+"F21.opPattern","COPY",BODY,{"derivedFrom":makeQuery(id+"F20.opPattern","COPY",BODY,{"derivedFrom":makeQuery(id+"F19.opPattern","COPY",BODY,{"derivedFrom":makeQuery(id+"F18.opPattern","COPY",BODY,{"derivedFrom":makeQuery(id+"F17.opPattern","COPY",BODY,{"derivedFrom":makeQuery(id+"F16.opPattern","COPY",BODY,{"derivedFrom":makeQuery(id+"F15.opPattern","COPY",BODY,{"derivedFrom":makeQuery(id+"F14.opPattern","COPY",BODY,{"derivedFrom":makeQuery(id+"F13.opPattern","COPY",BODY,{"derivedFrom":makeQuery(id+"F12.opPattern","COPY",BODY,{"derivedFrom":makeQuery(id+"F11.opPattern","COPY",BODY,{"derivedFrom":makeQuery(id+"F10.opPattern","COPY",BODY,{"derivedFrom":makeQuery(id+"F9.opPattern","COPY",BODY,{"derivedFrom":makeQuery(id+"F8.opPattern","COPY",BODY,{"derivedFrom":makeQuery(id+"F7.opPattern","COPY",BODY,{"derivedFrom":makeQuery(id+"F5.opPattern","COPY",BODY,{"derivedFrom":makeQuery(id+"F2.opExtrude","SWEPT_BODY",BODY,{"disambiguationData":[OSD([sQuery(id+"F0.wireOp",EDGE,"E1.8.0.0"),sQuery(id+"F0.wireOp",EDGE,"E2.1.0.2"),sQuery(id+"F0.wireOp",EDGE,"E2.2.0.2"),sQuery(id+"F0.wireOp",EDGE,"E2.3.0.2"),sQuery(id+"F0.wireOp",EDGE,"E2.4.0.2"),sQuery(id+"F0.wireOp",EDGE,"E2.5.0.2"),sQuery(id+"F0.wireOp",EDGE,"E2.6.0.2"),sQuery(id+"F0.wireOp",EDGE,"E2.7.0.2"),sQuery(id+"F0.wireOp",EDGE,"E2.8.0.2"),sQuery(id+"F0.wireOp",EDGE,"E2.9.0.2"),sQuery(id+"F0.wireOp",EDGE,"E2.10.0.2"),sQuery(id+"F0.wireOp",EDGE,"E2.11.0.2"),sQuery(id+"F0.wireOp",EDGE,"E2.12.0.2"),sQuery(id+"F0.wireOp",EDGE,"E2.13.0.2"),sQuery(id+"F0.wireOp",EDGE,"E2.14.0.2"),sQuery(id+"F0.wireOp",EDGE,"E2.15.0.2"),sQuery(id+"F0.wireOp",EDGE,"E2.16.0.2"),sQuery(id+"F0.wireOp",EDGE,"E2.17.0.2"),sQuery(id+"F0.wireOp",EDGE,"E2.18.0.2"),sQuery(id+"F0.wireOp",EDGE,"E2.19.0.2"),sQuery(id+"F0.wireOp",EDGE,"E2.20.0.2"),sQuery(id+"F0.wireOp",EDGE,"E2.21.0.2"),sQuery(id+"F0.wireOp",EDGE,"E2.22.0.2"),sQuery(id+"F0.wireOp",EDGE,"E2.23.0.2"),sQuery(id+"F0.wireOp",EDGE,"E2.24.0.2"),sQuery(id+"F0.wireOp",EDGE,"E2.25.0.2"),sQuery(id+"F0.wireOp",EDGE,"E2.26.0.2"),sQuery(id+"F0.wireOp",EDGE,"E2.27.0.2"),sQuery(id+"F0.wireOp",EDGE,"E2.28.0.2"),sQuery(id+"F0.wireOp",EDGE,"E2.29.0.2"),sQuery(id+"F0.wireOp",EDGE,"E9.5.30.0"),sQuery(id+"F0.wireOp",EDGE,"E9.5.31.0"),sQuery(id+"F0.wireOp",EDGE,"E9.5.32.0"),sQuery(id+"F0.wireOp",EDGE,"E9.5.33.0"),sQuery(id+"F0.wireOp",EDGE,"E9.5.34.0"),sQuery(id+"F0.wireOp",EDGE,"E9.5.35.0"),sQuery(id+"F0.wireOp",EDGE,"E9.5.36.0"),sQuery(id+"F0.wireOp",EDGE,"E9.5.37.0"),sQuery(id+"F0.wireOp",EDGE,"E9.5.38.0"),sQuery(id+"F0.wireOp",EDGE,"E9.5.39.0"),sQuery(id+"F0.wireOp",EDGE,"E9.5.40.0"),sQuery(id+"F0.wireOp",EDGE,"E9.5.41.0"),sQuery(id+"F0.wireOp",EDGE,"E9.5.42.0"),sQuery(id+"F0.wireOp",EDGE,"E9.5.43.0"),sQuery(id+"F0.wireOp",EDGE,"E9.5.44.0"),sQuery(id+"F0.wireOp",EDGE,"E9.5.45.0"),sQuery(id+"F0.wireOp",EDGE,"E9.5.46.0"),sQuery(id+"F0.wireOp",EDGE,"E19.rect.top"),sQuery(id+"F0.wireOp",EDGE,"E19.rect.left"),sQuery(id+"F0.wireOp",EDGE,"E19.rect.right"),sQuery(id+"F0.wireOp",EDGE,"E22")])]}),"instanceName":"1"}),"instanceName":"1"}),"instanceName":"1"}),"instanceName":"1"}),"instanceName":"1"}),"instanceName":"1"}),"instanceName":"1"}),"instanceName":"1"}),"instanceName":"1"}),"instanceName":"1"}),"instanceName":"1"}),"instanceName":"1"}),"instanceName":"1"}),"instanceName":"1"}),"instanceName":"1"}),"instanceName":"1"}),"instanceName":"1"}),"instanceName":"1"}),"instanceName":"1"}),"instanceName":"1"}),"instanceName":"1"}),"instanceName":"1"}),"instanceName":"1"}),"instanceName":"1"}),"instanceName":"1"});
            transform(context, id + "F31", {"entities" : qUnion([Q0]), "transformType" : TransformType.TRANSLATION_3D, "dx" : 2.54 * mm, "dy" : 0 * mm, "dz" : 0 * mm, "makeCopy" : true});
        }
        {
            var Q0;
            Q0=makeQuery(id+"F31.opPattern","COPY",BODY,{"derivedFrom":makeQuery(id+"F30.opPattern","COPY",BODY,{"derivedFrom":makeQuery(id+"F29.opPattern","COPY",BODY,{"derivedFrom":makeQuery(id+"F28.opPattern","COPY",BODY,{"derivedFrom":makeQuery(id+"F27.opPattern","COPY",BODY,{"derivedFrom":makeQuery(id+"F26.opPattern","COPY",BODY,{"derivedFrom":makeQuery(id+"F25.opPattern","COPY",BODY,{"derivedFrom":makeQuery(id+"F24.opPattern","COPY",BODY,{"derivedFrom":makeQuery(id+"F23.opPattern","COPY",BODY,{"derivedFrom":makeQuery(id+"F22.opPattern","COPY",BODY,{"derivedFrom":makeQuery(id+"F21.opPattern","COPY",BODY,{"derivedFrom":makeQuery(id+"F20.opPattern","COPY",BODY,{"derivedFrom":makeQuery(id+"F19.opPattern","COPY",BODY,{"derivedFrom":makeQuery(id+"F18.opPattern","COPY",BODY,{"derivedFrom":makeQuery(id+"F17.opPattern","COPY",BODY,{"derivedFrom":makeQuery(id+"F16.opPattern","COPY",BODY,{"derivedFrom":makeQuery(id+"F15.opPattern","COPY",BODY,{"derivedFrom":makeQuery(id+"F14.opPattern","COPY",BODY,{"derivedFrom":makeQuery(id+"F13.opPattern","COPY",BODY,{"derivedFrom":makeQuery(id+"F12.opPattern","COPY",BODY,{"derivedFrom":makeQuery(id+"F11.opPattern","COPY",BODY,{"derivedFrom":makeQuery(id+"F10.opPattern","COPY",BODY,{"derivedFrom":makeQuery(id+"F9.opPattern","COPY",BODY,{"derivedFrom":makeQuery(id+"F8.opPattern","COPY",BODY,{"derivedFrom":makeQuery(id+"F7.opPattern","COPY",BODY,{"derivedFrom":makeQuery(id+"F5.opPattern","COPY",BODY,{"derivedFrom":makeQuery(id+"F2.opExtrude","SWEPT_BODY",BODY,{"disambiguationData":[OSD([sQuery(id+"F0.wireOp",EDGE,"E1.8.0.0"),sQuery(id+"F0.wireOp",EDGE,"E2.1.0.2"),sQuery(id+"F0.wireOp",EDGE,"E2.2.0.2"),sQuery(id+"F0.wireOp",EDGE,"E2.3.0.2"),sQuery(id+"F0.wireOp",EDGE,"E2.4.0.2"),sQuery(id+"F0.wireOp",EDGE,"E2.5.0.2"),sQuery(id+"F0.wireOp",EDGE,"E2.6.0.2"),sQuery(id+"F0.wireOp",EDGE,"E2.7.0.2"),sQuery(id+"F0.wireOp",EDGE,"E2.8.0.2"),sQuery(id+"F0.wireOp",EDGE,"E2.9.0.2"),sQuery(id+"F0.wireOp",EDGE,"E2.10.0.2"),sQuery(id+"F0.wireOp",EDGE,"E2.11.0.2"),sQuery(id+"F0.wireOp",EDGE,"E2.12.0.2"),sQuery(id+"F0.wireOp",EDGE,"E2.13.0.2"),sQuery(id+"F0.wireOp",EDGE,"E2.14.0.2"),sQuery(id+"F0.wireOp",EDGE,"E2.15.0.2"),sQuery(id+"F0.wireOp",EDGE,"E2.16.0.2"),sQuery(id+"F0.wireOp",EDGE,"E2.17.0.2"),sQuery(id+"F0.wireOp",EDGE,"E2.18.0.2"),sQuery(id+"F0.wireOp",EDGE,"E2.19.0.2"),sQuery(id+"F0.wireOp",EDGE,"E2.20.0.2"),sQuery(id+"F0.wireOp",EDGE,"E2.21.0.2"),sQuery(id+"F0.wireOp",EDGE,"E2.22.0.2"),sQuery(id+"F0.wireOp",EDGE,"E2.23.0.2"),sQuery(id+"F0.wireOp",EDGE,"E2.24.0.2"),sQuery(id+"F0.wireOp",EDGE,"E2.25.0.2"),sQuery(id+"F0.wireOp",EDGE,"E2.26.0.2"),sQuery(id+"F0.wireOp",EDGE,"E2.27.0.2"),sQuery(id+"F0.wireOp",EDGE,"E2.28.0.2"),sQuery(id+"F0.wireOp",EDGE,"E2.29.0.2"),sQuery(id+"F0.wireOp",EDGE,"E9.5.30.0"),sQuery(id+"F0.wireOp",EDGE,"E9.5.31.0"),sQuery(id+"F0.wireOp",EDGE,"E9.5.32.0"),sQuery(id+"F0.wireOp",EDGE,"E9.5.33.0"),sQuery(id+"F0.wireOp",EDGE,"E9.5.34.0"),sQuery(id+"F0.wireOp",EDGE,"E9.5.35.0"),sQuery(id+"F0.wireOp",EDGE,"E9.5.36.0"),sQuery(id+"F0.wireOp",EDGE,"E9.5.37.0"),sQuery(id+"F0.wireOp",EDGE,"E9.5.38.0"),sQuery(id+"F0.wireOp",EDGE,"E9.5.39.0"),sQuery(id+"F0.wireOp",EDGE,"E9.5.40.0"),sQuery(id+"F0.wireOp",EDGE,"E9.5.41.0"),sQuery(id+"F0.wireOp",EDGE,"E9.5.42.0"),sQuery(id+"F0.wireOp",EDGE,"E9.5.43.0"),sQuery(id+"F0.wireOp",EDGE,"E9.5.44.0"),sQuery(id+"F0.wireOp",EDGE,"E9.5.45.0"),sQuery(id+"F0.wireOp",EDGE,"E9.5.46.0"),sQuery(id+"F0.wireOp",EDGE,"E19.rect.top"),sQuery(id+"F0.wireOp",EDGE,"E19.rect.left"),sQuery(id+"F0.wireOp",EDGE,"E19.rect.right"),sQuery(id+"F0.wireOp",EDGE,"E22")])]}),"instanceName":"1"}),"instanceName":"1"}),"instanceName":"1"}),"instanceName":"1"}),"instanceName":"1"}),"instanceName":"1"}),"instanceName":"1"}),"instanceName":"1"}),"instanceName":"1"}),"instanceName":"1"}),"instanceName":"1"}),"instanceName":"1"}),"instanceName":"1"}),"instanceName":"1"}),"instanceName":"1"}),"instanceName":"1"}),"instanceName":"1"}),"instanceName":"1"}),"instanceName":"1"}),"instanceName":"1"}),"instanceName":"1"}),"instanceName":"1"}),"instanceName":"1"}),"instanceName":"1"}),"instanceName":"1"}),"instanceName":"1"});
            transform(context, id + "F32", {"entities" : qUnion([Q0]), "transformType" : TransformType.TRANSLATION_3D, "dx" : 2.54 * mm, "dy" : 0 * mm, "dz" : 0 * mm, "makeCopy" : true});
        }
    });
